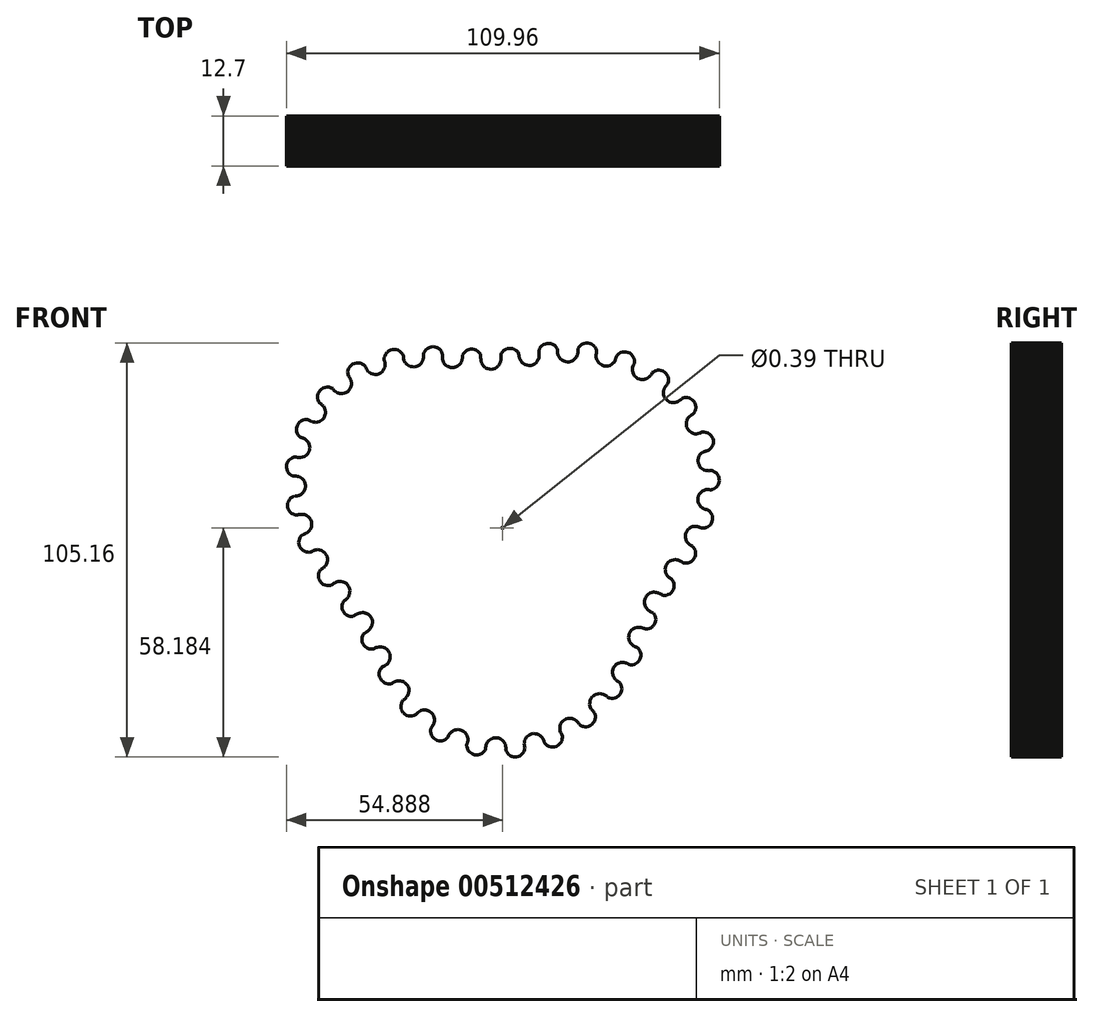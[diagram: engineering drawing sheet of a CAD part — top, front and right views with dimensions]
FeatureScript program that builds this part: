
annotation { "Feature Type Name" : "Feature", "Feature Type Description" : "" }
export const myFeature = defineFeature(function(context is Context, id is Id, definition is map)
    precondition{}
    {
        {
            var Q0;
            Q0=qCreatedBy(makeId("Front.planeOp"),FACE);
            var sketch = newSketch(context, id + "F0", { "sketchPlane" : qUnion([Q0])});
            skCircle(sketch, "E0", {"center": v(-0.1, 5.6) * mm, "radius": 0.2 * mm});
            skLineSegment(sketch, "E1", {"start": v(-7.26, -52) * mm, "end": v(-6.77, -52.07) * mm});
            skLineSegment(sketch, "E2", {"start": v(-6.77, -52.07) * mm, "end": v(-6.32, -52.04) * mm});
            skLineSegment(sketch, "E3", {"start": v(-6.32, -52.04) * mm, "end": v(-6.3, -52.04) * mm});
            skLineSegment(sketch, "E4", {"start": v(-6.3, -52.04) * mm, "end": v(-6.26, -52.04) * mm});
            skLineSegment(sketch, "E5", {"start": v(-6.26, -52.04) * mm, "end": v(-5.96, -51.96) * mm});
            skLineSegment(sketch, "E6", {"start": v(-5.96, -51.96) * mm, "end": v(-5.73, -51.88) * mm});
            skLineSegment(sketch, "E7", {"start": v(-5.73, -51.88) * mm, "end": v(-5.6, -51.82) * mm});
            skLineSegment(sketch, "E8", {"start": v(-5.6, -51.82) * mm, "end": v(-5.26, -51.62) * mm});
            skLineSegment(sketch, "E9", {"start": v(-5.26, -51.62) * mm, "end": v(-4.89, -51.3) * mm});
            skLineSegment(sketch, "E10", {"start": v(-4.89, -51.3) * mm, "end": v(-4.58, -50.9) * mm});
            skLineSegment(sketch, "E11", {"start": v(-4.58, -50.9) * mm, "end": v(-4.45, -50.63) * mm});
            skLineSegment(sketch, "E12", {"start": v(-4.45, -50.63) * mm, "end": v(-4.38, -50.48) * mm});
            skLineSegment(sketch, "E13", {"start": v(-4.38, -50.48) * mm, "end": v(-4.38, -50.3) * mm});
            skLineSegment(sketch, "E14", {"start": v(-4.38, -50.3) * mm, "end": v(-4.36, -50.15) * mm});
            skLineSegment(sketch, "E15", {"start": v(-4.36, -50.15) * mm, "end": v(-4.34, -49.93) * mm});
            skLineSegment(sketch, "E16", {"start": v(-4.34, -49.93) * mm, "end": v(-4.29, -49.71) * mm});
            skLineSegment(sketch, "E17", {"start": v(-4.29, -49.71) * mm, "end": v(-4.28, -49.67) * mm});
            skLineSegment(sketch, "E18", {"start": v(-4.28, -49.67) * mm, "end": v(-4.26, -49.6) * mm});
            skLineSegment(sketch, "E19", {"start": v(-4.26, -49.6) * mm, "end": v(-4.24, -49.52) * mm});
            skLineSegment(sketch, "E20", {"start": v(-4.24, -49.52) * mm, "end": v(-4.22, -49.45) * mm});
            skLineSegment(sketch, "E21", {"start": v(-4.22, -49.45) * mm, "end": v(-4.2, -49.4) * mm});
            skLineSegment(sketch, "E22", {"start": v(-4.2, -49.4) * mm, "end": v(-4.15, -49.25) * mm});
            skLineSegment(sketch, "E23", {"start": v(-4.15, -49.25) * mm, "end": v(-4.13, -49.2) * mm});
            skLineSegment(sketch, "E24", {"start": v(-4.13, -49.2) * mm, "end": v(-3.9, -48.77) * mm});
            skLineSegment(sketch, "E25", {"start": v(-3.9, -48.77) * mm, "end": v(-3.57, -48.4) * mm});
            skLineSegment(sketch, "E26", {"start": v(-3.57, -48.4) * mm, "end": v(-3.18, -48.1) * mm});
            skLineSegment(sketch, "E27", {"start": v(-3.18, -48.1) * mm, "end": v(-2.74, -47.87) * mm});
            skLineSegment(sketch, "E28", {"start": v(-2.74, -47.87) * mm, "end": v(-2.58, -47.82) * mm});
            skLineSegment(sketch, "E29", {"start": v(-2.58, -47.82) * mm, "end": v(-2.56, -47.81) * mm});
            skLineSegment(sketch, "E30", {"start": v(-2.56, -47.81) * mm, "end": v(-2.52, -47.8) * mm});
            skLineSegment(sketch, "E31", {"start": v(-2.52, -47.8) * mm, "end": v(-2.27, -47.73) * mm});
            skLineSegment(sketch, "E32", {"start": v(-2.27, -47.73) * mm, "end": v(-2.15, -47.72) * mm});
            skLineSegment(sketch, "E33", {"start": v(-2.15, -47.72) * mm, "end": v(-2.08, -47.7) * mm});
            skLineSegment(sketch, "E34", {"start": v(-2.08, -47.7) * mm, "end": v(-1.93, -47.7) * mm});
            skLineSegment(sketch, "E35", {"start": v(-1.93, -47.7) * mm, "end": v(-1.8, -47.7) * mm});
            skLineSegment(sketch, "E36", {"start": v(-1.8, -47.7) * mm, "end": v(-1.78, -47.7) * mm});
            skLineSegment(sketch, "E37", {"start": v(-1.78, -47.7) * mm, "end": v(-1.78, -47.7) * mm});
            skLineSegment(sketch, "E38", {"start": v(-1.78, -47.7) * mm, "end": v(-1.7, -47.7) * mm});
            skLineSegment(sketch, "E39", {"start": v(-1.7, -47.7) * mm, "end": v(-1.6, -47.7) * mm});
            skLineSegment(sketch, "E40", {"start": v(-1.6, -47.7) * mm, "end": v(-1.59, -47.7) * mm});
            skLineSegment(sketch, "E41", {"start": v(-1.59, -47.7) * mm, "end": v(-1.59, -47.7) * mm});
            skLineSegment(sketch, "E42", {"start": v(-1.59, -47.7) * mm, "end": v(-1.34, -47.74) * mm});
            skLineSegment(sketch, "E43", {"start": v(-1.34, -47.74) * mm, "end": v(-1.29, -47.75) * mm});
            skLineSegment(sketch, "E44", {"start": v(-1.29, -47.75) * mm, "end": v(-1.26, -47.76) * mm});
            skLineSegment(sketch, "E45", {"start": v(-1.26, -47.76) * mm, "end": v(-1.1, -47.79) * mm});
            skLineSegment(sketch, "E46", {"start": v(-1.1, -47.79) * mm, "end": v(-0.64, -47.97) * mm});
            skLineSegment(sketch, "E47", {"start": v(-0.64, -47.97) * mm, "end": v(-0.23, -48.24) * mm});
            skLineSegment(sketch, "E48", {"start": v(-0.23, -48.24) * mm, "end": v(0.13, -48.58) * mm});
            skLineSegment(sketch, "E49", {"start": v(0.13, -48.58) * mm, "end": v(0.41, -48.99) * mm});
            skLineSegment(sketch, "E50", {"start": v(0.41, -48.99) * mm, "end": v(0.6, -49.44) * mm});
            skLineSegment(sketch, "E51", {"start": v(0.6, -49.44) * mm, "end": v(0.64, -49.61) * mm});
            skLineSegment(sketch, "E52", {"start": v(0.64, -49.61) * mm, "end": v(0.67, -49.7) * mm});
            skLineSegment(sketch, "E53", {"start": v(0.67, -49.7) * mm, "end": v(0.7, -49.86) * mm});
            skLineSegment(sketch, "E54", {"start": v(0.7, -49.86) * mm, "end": v(0.71, -49.92) * mm});
            skLineSegment(sketch, "E55", {"start": v(0.71, -49.92) * mm, "end": v(0.71, -49.95) * mm});
            skLineSegment(sketch, "E56", {"start": v(0.71, -49.95) * mm, "end": v(0.75, -50.18) * mm});
            skLineSegment(sketch, "E57", {"start": v(0.75, -50.18) * mm, "end": v(0.74, -50.4) * mm});
            skLineSegment(sketch, "E58", {"start": v(0.74, -50.4) * mm, "end": v(0.75, -50.54) * mm});
            skLineSegment(sketch, "E59", {"start": v(0.75, -50.54) * mm, "end": v(0.74, -50.58) * mm});
            skLineSegment(sketch, "E60", {"start": v(0.74, -50.58) * mm, "end": v(0.73, -50.74) * mm});
            skLineSegment(sketch, "E61", {"start": v(0.73, -50.74) * mm, "end": v(0.76, -50.84) * mm});
            skLineSegment(sketch, "E62", {"start": v(0.76, -50.84) * mm, "end": v(0.78, -50.93) * mm});
            skLineSegment(sketch, "E63", {"start": v(0.78, -50.93) * mm, "end": v(0.88, -51.2) * mm});
            skLineSegment(sketch, "E64", {"start": v(0.88, -51.2) * mm, "end": v(1.14, -51.61) * mm});
            skLineSegment(sketch, "E65", {"start": v(1.14, -51.61) * mm, "end": v(1.48, -51.97) * mm});
            skLineSegment(sketch, "E66", {"start": v(1.48, -51.97) * mm, "end": v(1.86, -52.24) * mm});
            skLineSegment(sketch, "E67", {"start": v(1.86, -52.24) * mm, "end": v(1.9, -52.27) * mm});
            skLineSegment(sketch, "E68", {"start": v(1.9, -52.27) * mm, "end": v(2.2, -52.4) * mm});
            skLineSegment(sketch, "E69", {"start": v(2.2, -52.4) * mm, "end": v(2.4, -52.48) * mm});
            skLineSegment(sketch, "E70", {"start": v(2.4, -52.48) * mm, "end": v(2.57, -52.52) * mm});
            skLineSegment(sketch, "E71", {"start": v(2.57, -52.52) * mm, "end": v(2.68, -52.54) * mm});
            skLineSegment(sketch, "E72", {"start": v(2.68, -52.54) * mm, "end": v(2.93, -52.58) * mm});
            skLineSegment(sketch, "E73", {"start": v(2.93, -52.58) * mm, "end": v(2.94, -52.58) * mm});
            skLineSegment(sketch, "E74", {"start": v(2.94, -52.58) * mm, "end": v(2.94, -52.58) * mm});
            skLineSegment(sketch, "E75", {"start": v(2.94, -52.58) * mm, "end": v(3.43, -52.57) * mm});
            skLineSegment(sketch, "E76", {"start": v(3.43, -52.57) * mm, "end": v(3.43, -52.57) * mm});
            skLineSegment(sketch, "E77", {"start": v(3.43, -52.57) * mm, "end": v(3.91, -52.46) * mm});
            skLineSegment(sketch, "E78", {"start": v(3.91, -52.46) * mm, "end": v(4.36, -52.25) * mm});
            skLineSegment(sketch, "E79", {"start": v(4.36, -52.25) * mm, "end": v(4.76, -51.97) * mm});
            skLineSegment(sketch, "E80", {"start": v(4.76, -51.97) * mm, "end": v(5.1, -51.6) * mm});
            skLineSegment(sketch, "E81", {"start": v(5.1, -51.6) * mm, "end": v(5.36, -51.19) * mm});
            skLineSegment(sketch, "E82", {"start": v(5.36, -51.19) * mm, "end": v(5.52, -50.76) * mm});
            skLineSegment(sketch, "E83", {"start": v(5.52, -50.76) * mm, "end": v(5.54, -50.7) * mm});
            skLineSegment(sketch, "E84", {"start": v(5.54, -50.7) * mm, "end": v(5.54, -50.7) * mm});
            skLineSegment(sketch, "E85", {"start": v(5.54, -50.7) * mm, "end": v(5.56, -50.56) * mm});
            skLineSegment(sketch, "E86", {"start": v(5.56, -50.56) * mm, "end": v(5.6, -50.23) * mm});
            skLineSegment(sketch, "E87", {"start": v(5.6, -50.23) * mm, "end": v(5.5, -49.94) * mm});
            skLineSegment(sketch, "E88", {"start": v(5.5, -49.94) * mm, "end": v(5.49, -49.76) * mm});
            skLineSegment(sketch, "E89", {"start": v(5.49, -49.76) * mm, "end": v(5.45, -49.6) * mm});
            skLineSegment(sketch, "E90", {"start": v(5.45, -49.6) * mm, "end": v(5.43, -49.1) * mm});
            skLineSegment(sketch, "E91", {"start": v(5.43, -49.1) * mm, "end": v(5.45, -48.97) * mm});
            skLineSegment(sketch, "E92", {"start": v(5.45, -48.97) * mm, "end": v(5.45, -48.87) * mm});
            skLineSegment(sketch, "E93", {"start": v(5.45, -48.87) * mm, "end": v(5.5, -48.68) * mm});
            skLineSegment(sketch, "E94", {"start": v(5.5, -48.68) * mm, "end": v(5.5, -48.62) * mm});
            skLineSegment(sketch, "E95", {"start": v(5.5, -48.62) * mm, "end": v(5.51, -48.6) * mm});
            skLineSegment(sketch, "E96", {"start": v(5.51, -48.6) * mm, "end": v(5.56, -48.39) * mm});
            skLineSegment(sketch, "E97", {"start": v(5.56, -48.39) * mm, "end": v(5.76, -47.94) * mm});
            skLineSegment(sketch, "E98", {"start": v(5.76, -47.94) * mm, "end": v(6.04, -47.53) * mm});
            skLineSegment(sketch, "E99", {"start": v(6.04, -47.53) * mm, "end": v(6.4, -47.19) * mm});
            skLineSegment(sketch, "E100", {"start": v(6.4, -47.19) * mm, "end": v(6.81, -46.92) * mm});
            skLineSegment(sketch, "E101", {"start": v(6.81, -46.92) * mm, "end": v(7.27, -46.74) * mm});
            skLineSegment(sketch, "E102", {"start": v(7.27, -46.74) * mm, "end": v(7.27, -46.74) * mm});
            skLineSegment(sketch, "E103", {"start": v(7.27, -46.74) * mm, "end": v(7.76, -46.66) * mm});
            skLineSegment(sketch, "E104", {"start": v(7.76, -46.66) * mm, "end": v(8.25, -46.67) * mm});
            skLineSegment(sketch, "E105", {"start": v(8.25, -46.67) * mm, "end": v(8.73, -46.77) * mm});
            skLineSegment(sketch, "E106", {"start": v(8.73, -46.77) * mm, "end": v(8.87, -46.83) * mm});
            skLineSegment(sketch, "E107", {"start": v(8.87, -46.83) * mm, "end": v(8.92, -46.85) * mm});
            skLineSegment(sketch, "E108", {"start": v(8.92, -46.85) * mm, "end": v(9.03, -46.9) * mm});
            skLineSegment(sketch, "E109", {"start": v(9.03, -46.9) * mm, "end": v(9.19, -46.97) * mm});
            skLineSegment(sketch, "E110", {"start": v(9.19, -46.97) * mm, "end": v(9.25, -47.02) * mm});
            skLineSegment(sketch, "E111", {"start": v(9.25, -47.02) * mm, "end": v(9.36, -47.07) * mm});
            skLineSegment(sketch, "E112", {"start": v(9.36, -47.07) * mm, "end": v(9.56, -47.23) * mm});
            skLineSegment(sketch, "E113", {"start": v(9.56, -47.23) * mm, "end": v(9.6, -47.25) * mm});
            skLineSegment(sketch, "E114", {"start": v(9.6, -47.25) * mm, "end": v(9.6, -47.27) * mm});
            skLineSegment(sketch, "E115", {"start": v(9.6, -47.27) * mm, "end": v(9.75, -47.38) * mm});
            skLineSegment(sketch, "E116", {"start": v(9.75, -47.38) * mm, "end": v(10.07, -47.76) * mm});
            skLineSegment(sketch, "E117", {"start": v(10.07, -47.76) * mm, "end": v(10.12, -47.86) * mm});
            skLineSegment(sketch, "E118", {"start": v(10.12, -47.86) * mm, "end": v(10.2, -48) * mm});
            skLineSegment(sketch, "E119", {"start": v(10.2, -48) * mm, "end": v(10.2, -48.02) * mm});
            skLineSegment(sketch, "E120", {"start": v(10.2, -48.02) * mm, "end": v(10.22, -48.03) * mm});
            skLineSegment(sketch, "E121", {"start": v(10.22, -48.03) * mm, "end": v(10.3, -48.2) * mm});
            skLineSegment(sketch, "E122", {"start": v(10.3, -48.2) * mm, "end": v(10.33, -48.26) * mm});
            skLineSegment(sketch, "E123", {"start": v(10.33, -48.26) * mm, "end": v(10.33, -48.27) * mm});
            skLineSegment(sketch, "E124", {"start": v(10.33, -48.27) * mm, "end": v(10.42, -48.46) * mm});
            skLineSegment(sketch, "E125", {"start": v(10.42, -48.46) * mm, "end": v(10.49, -48.72) * mm});
            skLineSegment(sketch, "E126", {"start": v(10.49, -48.72) * mm, "end": v(10.53, -48.84) * mm});
            skLineSegment(sketch, "E127", {"start": v(10.53, -48.84) * mm, "end": v(10.55, -48.94) * mm});
            skLineSegment(sketch, "E128", {"start": v(10.55, -48.94) * mm, "end": v(10.58, -48.98) * mm});
            skLineSegment(sketch, "E129", {"start": v(10.58, -48.98) * mm, "end": v(10.8, -49.28) * mm});
            skLineSegment(sketch, "E130", {"start": v(10.8, -49.28) * mm, "end": v(11.16, -49.6) * mm});
            skLineSegment(sketch, "E131", {"start": v(11.16, -49.6) * mm, "end": v(11.18, -49.6) * mm});
            skLineSegment(sketch, "E132", {"start": v(11.18, -49.6) * mm, "end": v(11.45, -49.77) * mm});
            skLineSegment(sketch, "E133", {"start": v(11.45, -49.77) * mm, "end": v(11.68, -49.88) * mm});
            skLineSegment(sketch, "E134", {"start": v(11.68, -49.88) * mm, "end": v(11.76, -49.9) * mm});
            skLineSegment(sketch, "E135", {"start": v(11.76, -49.9) * mm, "end": v(12.18, -50.02) * mm});
            skLineSegment(sketch, "E136", {"start": v(12.18, -50.02) * mm, "end": v(12.67, -50.06) * mm});
            skLineSegment(sketch, "E137", {"start": v(12.67, -50.06) * mm, "end": v(13.16, -50) * mm});
            skLineSegment(sketch, "E138", {"start": v(13.16, -50) * mm, "end": v(13.63, -49.84) * mm});
            skLineSegment(sketch, "E139", {"start": v(13.63, -49.84) * mm, "end": v(13.63, -49.84) * mm});
            skLineSegment(sketch, "E140", {"start": v(13.63, -49.84) * mm, "end": v(14.06, -49.6) * mm});
            skLineSegment(sketch, "E141", {"start": v(14.06, -49.6) * mm, "end": v(14.43, -49.28) * mm});
            skLineSegment(sketch, "E142", {"start": v(14.43, -49.28) * mm, "end": v(14.74, -48.89) * mm});
            skLineSegment(sketch, "E143", {"start": v(14.74, -48.89) * mm, "end": v(14.96, -48.45) * mm});
            skLineSegment(sketch, "E144", {"start": v(14.96, -48.45) * mm, "end": v(15.09, -47.97) * mm});
            skLineSegment(sketch, "E145", {"start": v(15.09, -47.97) * mm, "end": v(15.1, -47.67) * mm});
            skLineSegment(sketch, "E146", {"start": v(15.1, -47.67) * mm, "end": v(15.11, -47.4) * mm});
            skLineSegment(sketch, "E147", {"start": v(15.11, -47.4) * mm, "end": v(15.03, -46.98) * mm});
            skLineSegment(sketch, "E148", {"start": v(15.03, -46.98) * mm, "end": v(14.85, -46.71) * mm});
            skLineSegment(sketch, "E149", {"start": v(14.85, -46.71) * mm, "end": v(14.78, -46.53) * mm});
            skLineSegment(sketch, "E150", {"start": v(14.78, -46.53) * mm, "end": v(14.7, -46.4) * mm});
            skLineSegment(sketch, "E151", {"start": v(14.7, -46.4) * mm, "end": v(14.53, -45.92) * mm});
            skLineSegment(sketch, "E152", {"start": v(14.53, -45.92) * mm, "end": v(14.5, -45.76) * mm});
            skLineSegment(sketch, "E153", {"start": v(14.5, -45.76) * mm, "end": v(14.49, -45.68) * mm});
            skLineSegment(sketch, "E154", {"start": v(14.49, -45.68) * mm, "end": v(14.48, -45.54) * mm});
            skLineSegment(sketch, "E155", {"start": v(14.48, -45.54) * mm, "end": v(14.46, -45.44) * mm});
            skLineSegment(sketch, "E156", {"start": v(14.46, -45.44) * mm, "end": v(14.47, -45.38) * mm});
            skLineSegment(sketch, "E157", {"start": v(14.47, -45.38) * mm, "end": v(14.45, -45.2) * mm});
            skLineSegment(sketch, "E158", {"start": v(14.45, -45.2) * mm, "end": v(14.52, -44.7) * mm});
            skLineSegment(sketch, "E159", {"start": v(14.52, -44.7) * mm, "end": v(14.67, -44.23) * mm});
            skLineSegment(sketch, "E160", {"start": v(14.67, -44.23) * mm, "end": v(14.92, -43.8) * mm});
            skLineSegment(sketch, "E161", {"start": v(14.92, -43.8) * mm, "end": v(15.24, -43.43) * mm});
            skLineSegment(sketch, "E162", {"start": v(15.24, -43.43) * mm, "end": v(15.63, -43.13) * mm});
            skLineSegment(sketch, "E163", {"start": v(15.63, -43.13) * mm, "end": v(15.63, -43.13) * mm});
            skLineSegment(sketch, "E164", {"start": v(15.63, -43.13) * mm, "end": v(16.07, -42.9) * mm});
            skLineSegment(sketch, "E165", {"start": v(16.07, -42.9) * mm, "end": v(16.55, -42.78) * mm});
            skLineSegment(sketch, "E166", {"start": v(16.55, -42.78) * mm, "end": v(17.04, -42.74) * mm});
            skLineSegment(sketch, "E167", {"start": v(17.04, -42.74) * mm, "end": v(17.53, -42.8) * mm});
            skLineSegment(sketch, "E168", {"start": v(17.53, -42.8) * mm, "end": v(17.67, -42.85) * mm});
            skLineSegment(sketch, "E169", {"start": v(17.67, -42.85) * mm, "end": v(17.74, -42.86) * mm});
            skLineSegment(sketch, "E170", {"start": v(17.74, -42.86) * mm, "end": v(17.88, -42.92) * mm});
            skLineSegment(sketch, "E171", {"start": v(17.88, -42.92) * mm, "end": v(18, -42.96) * mm});
            skLineSegment(sketch, "E172", {"start": v(18, -42.96) * mm, "end": v(18.05, -42.99) * mm});
            skLineSegment(sketch, "E173", {"start": v(18.05, -42.99) * mm, "end": v(18.2, -43.05) * mm});
            skLineSegment(sketch, "E174", {"start": v(18.2, -43.05) * mm, "end": v(18.6, -43.32) * mm});
            skLineSegment(sketch, "E175", {"start": v(18.6, -43.32) * mm, "end": v(18.96, -43.67) * mm});
            skLineSegment(sketch, "E176", {"start": v(18.96, -43.67) * mm, "end": v(19.02, -43.76) * mm});
            skLineSegment(sketch, "E177", {"start": v(19.02, -43.76) * mm, "end": v(19.16, -43.91) * mm});
            skLineSegment(sketch, "E178", {"start": v(19.16, -43.91) * mm, "end": v(19.31, -44.17) * mm});
            skLineSegment(sketch, "E179", {"start": v(19.31, -44.17) * mm, "end": v(19.39, -44.27) * mm});
            skLineSegment(sketch, "E180", {"start": v(19.39, -44.27) * mm, "end": v(19.4, -44.3) * mm});
            skLineSegment(sketch, "E181", {"start": v(19.4, -44.3) * mm, "end": v(19.45, -44.34) * mm});
            skLineSegment(sketch, "E182", {"start": v(19.45, -44.34) * mm, "end": v(19.73, -44.55) * mm});
            skLineSegment(sketch, "E183", {"start": v(19.73, -44.55) * mm, "end": v(20.18, -44.76) * mm});
            skLineSegment(sketch, "E184", {"start": v(20.18, -44.76) * mm, "end": v(20.32, -44.8) * mm});
            skLineSegment(sketch, "E185", {"start": v(20.32, -44.8) * mm, "end": v(20.6, -44.87) * mm});
            skLineSegment(sketch, "E186", {"start": v(20.6, -44.87) * mm, "end": v(20.69, -44.88) * mm});
            skLineSegment(sketch, "E187", {"start": v(20.69, -44.88) * mm, "end": v(20.9, -44.9) * mm});
            skLineSegment(sketch, "E188", {"start": v(20.9, -44.9) * mm, "end": v(20.95, -44.9) * mm});
            skLineSegment(sketch, "E189", {"start": v(20.95, -44.9) * mm, "end": v(21.1, -44.9) * mm});
            skLineSegment(sketch, "E190", {"start": v(21.1, -44.9) * mm, "end": v(21.25, -44.9) * mm});
            skLineSegment(sketch, "E191", {"start": v(21.25, -44.9) * mm, "end": v(21.28, -44.89) * mm});
            skLineSegment(sketch, "E192", {"start": v(21.28, -44.89) * mm, "end": v(21.3, -44.88) * mm});
            skLineSegment(sketch, "E193", {"start": v(21.3, -44.88) * mm, "end": v(21.75, -44.79) * mm});
            skLineSegment(sketch, "E194", {"start": v(21.75, -44.79) * mm, "end": v(22.2, -44.59) * mm});
            skLineSegment(sketch, "E195", {"start": v(22.2, -44.59) * mm, "end": v(22.6, -44.3) * mm});
            skLineSegment(sketch, "E196", {"start": v(22.6, -44.3) * mm, "end": v(22.6, -44.3) * mm});
            skLineSegment(sketch, "E197", {"start": v(22.6, -44.3) * mm, "end": v(22.95, -43.95) * mm});
            skLineSegment(sketch, "E198", {"start": v(22.95, -43.95) * mm, "end": v(23.22, -43.54) * mm});
            skLineSegment(sketch, "E199", {"start": v(23.22, -43.54) * mm, "end": v(23.4, -43.08) * mm});
            skLineSegment(sketch, "E200", {"start": v(23.4, -43.08) * mm, "end": v(23.49, -42.6) * mm});
            skLineSegment(sketch, "E201", {"start": v(23.49, -42.6) * mm, "end": v(23.48, -42.1) * mm});
            skLineSegment(sketch, "E202", {"start": v(23.48, -42.1) * mm, "end": v(23.4, -41.7) * mm});
            skLineSegment(sketch, "E203", {"start": v(23.4, -41.7) * mm, "end": v(23.35, -41.57) * mm});
            skLineSegment(sketch, "E204", {"start": v(23.35, -41.57) * mm, "end": v(23.32, -41.5) * mm});
            skLineSegment(sketch, "E205", {"start": v(23.32, -41.5) * mm, "end": v(23.26, -41.4) * mm});
            skLineSegment(sketch, "E206", {"start": v(23.26, -41.4) * mm, "end": v(23.17, -41.2) * mm});
            skLineSegment(sketch, "E207", {"start": v(23.17, -41.2) * mm, "end": v(22.96, -41.04) * mm});
            skLineSegment(sketch, "E208", {"start": v(22.96, -41.04) * mm, "end": v(22.87, -40.92) * mm});
            skLineSegment(sketch, "E209", {"start": v(22.87, -40.92) * mm, "end": v(22.75, -40.8) * mm});
            skLineSegment(sketch, "E210", {"start": v(22.75, -40.8) * mm, "end": v(22.58, -40.58) * mm});
            skLineSegment(sketch, "E211", {"start": v(22.58, -40.58) * mm, "end": v(22.57, -40.56) * mm});
            skLineSegment(sketch, "E212", {"start": v(22.57, -40.56) * mm, "end": v(22.54, -40.52) * mm});
            skLineSegment(sketch, "E213", {"start": v(22.54, -40.52) * mm, "end": v(22.46, -40.4) * mm});
            skLineSegment(sketch, "E214", {"start": v(22.46, -40.4) * mm, "end": v(22.43, -40.33) * mm});
            skLineSegment(sketch, "E215", {"start": v(22.43, -40.33) * mm, "end": v(22.3, -40.14) * mm});
            skLineSegment(sketch, "E216", {"start": v(22.3, -40.14) * mm, "end": v(22.13, -39.68) * mm});
            skLineSegment(sketch, "E217", {"start": v(22.13, -39.68) * mm, "end": v(22.05, -39.2) * mm});
            skLineSegment(sketch, "E218", {"start": v(22.05, -39.2) * mm, "end": v(22.07, -38.7) * mm});
            skLineSegment(sketch, "E219", {"start": v(22.07, -38.7) * mm, "end": v(22.18, -38.22) * mm});
            skLineSegment(sketch, "E220", {"start": v(22.18, -38.22) * mm, "end": v(22.39, -37.77) * mm});
            skLineSegment(sketch, "E221", {"start": v(22.39, -37.77) * mm, "end": v(22.68, -37.37) * mm});
            skLineSegment(sketch, "E222", {"start": v(22.68, -37.37) * mm, "end": v(22.68, -37.37) * mm});
            skLineSegment(sketch, "E223", {"start": v(22.68, -37.37) * mm, "end": v(22.79, -37.26) * mm});
            skLineSegment(sketch, "E224", {"start": v(22.79, -37.26) * mm, "end": v(22.83, -37.22) * mm});
            skLineSegment(sketch, "E225", {"start": v(22.83, -37.22) * mm, "end": v(22.83, -37.22) * mm});
            skLineSegment(sketch, "E226", {"start": v(22.83, -37.22) * mm, "end": v(22.9, -37.15) * mm});
            skLineSegment(sketch, "E227", {"start": v(22.9, -37.15) * mm, "end": v(23.04, -37.03) * mm});
            skLineSegment(sketch, "E228", {"start": v(23.04, -37.03) * mm, "end": v(23.12, -36.98) * mm});
            skLineSegment(sketch, "E229", {"start": v(23.12, -36.98) * mm, "end": v(23.2, -36.9) * mm});
            skLineSegment(sketch, "E230", {"start": v(23.2, -36.9) * mm, "end": v(23.4, -36.8) * mm});
            skLineSegment(sketch, "E231", {"start": v(23.4, -36.8) * mm, "end": v(23.46, -36.77) * mm});
            skLineSegment(sketch, "E232", {"start": v(23.46, -36.77) * mm, "end": v(23.49, -36.76) * mm});
            skLineSegment(sketch, "E233", {"start": v(23.49, -36.76) * mm, "end": v(23.65, -36.68) * mm});
            skLineSegment(sketch, "E234", {"start": v(23.65, -36.68) * mm, "end": v(24.12, -36.54) * mm});
            skLineSegment(sketch, "E235", {"start": v(24.12, -36.54) * mm, "end": v(24.6, -36.5) * mm});
            skLineSegment(sketch, "E236", {"start": v(24.6, -36.5) * mm, "end": v(25.1, -36.54) * mm});
            skLineSegment(sketch, "E237", {"start": v(25.1, -36.54) * mm, "end": v(25.57, -36.69) * mm});
            skLineSegment(sketch, "E238", {"start": v(25.57, -36.69) * mm, "end": v(25.8, -36.8) * mm});
            skLineSegment(sketch, "E239", {"start": v(25.8, -36.8) * mm, "end": v(25.84, -36.83) * mm});
            skLineSegment(sketch, "E240", {"start": v(25.84, -36.83) * mm, "end": v(25.92, -36.88) * mm});
            skLineSegment(sketch, "E241", {"start": v(25.92, -36.88) * mm, "end": v(26, -36.92) * mm});
            skLineSegment(sketch, "E242", {"start": v(26, -36.92) * mm, "end": v(26.02, -36.93) * mm});
            skLineSegment(sketch, "E243", {"start": v(26.02, -36.93) * mm, "end": v(26.04, -36.95) * mm});
            skLineSegment(sketch, "E244", {"start": v(26.04, -36.95) * mm, "end": v(26.26, -37.1) * mm});
            skLineSegment(sketch, "E245", {"start": v(26.26, -37.1) * mm, "end": v(26.4, -37.21) * mm});
            skLineSegment(sketch, "E246", {"start": v(26.4, -37.21) * mm, "end": v(26.45, -37.27) * mm});
            skLineSegment(sketch, "E247", {"start": v(26.45, -37.27) * mm, "end": v(26.58, -37.37) * mm});
            skLineSegment(sketch, "E248", {"start": v(26.58, -37.37) * mm, "end": v(26.65, -37.45) * mm});
            skLineSegment(sketch, "E249", {"start": v(26.65, -37.45) * mm, "end": v(26.68, -37.48) * mm});
            skLineSegment(sketch, "E250", {"start": v(26.68, -37.48) * mm, "end": v(26.9, -37.57) * mm});
            skLineSegment(sketch, "E251", {"start": v(26.9, -37.57) * mm, "end": v(27.06, -37.63) * mm});
            skLineSegment(sketch, "E252", {"start": v(27.06, -37.63) * mm, "end": v(27.54, -37.72) * mm});
            skLineSegment(sketch, "E253", {"start": v(27.54, -37.72) * mm, "end": v(28.04, -37.7) * mm});
            skLineSegment(sketch, "E254", {"start": v(28.04, -37.7) * mm, "end": v(28.52, -37.6) * mm});
            skLineSegment(sketch, "E255", {"start": v(28.52, -37.6) * mm, "end": v(28.9, -37.43) * mm});
            skLineSegment(sketch, "E256", {"start": v(28.9, -37.43) * mm, "end": v(29, -37.38) * mm});
            skLineSegment(sketch, "E257", {"start": v(29, -37.38) * mm, "end": v(29.16, -37.26) * mm});
            skLineSegment(sketch, "E258", {"start": v(29.16, -37.26) * mm, "end": v(29.2, -37.22) * mm});
            skLineSegment(sketch, "E259", {"start": v(29.2, -37.22) * mm, "end": v(29.42, -37.06) * mm});
            skLineSegment(sketch, "E260", {"start": v(29.42, -37.06) * mm, "end": v(29.5, -36.98) * mm});
            skLineSegment(sketch, "E261", {"start": v(29.5, -36.98) * mm, "end": v(29.76, -36.66) * mm});
            skLineSegment(sketch, "E262", {"start": v(29.76, -36.66) * mm, "end": v(29.76, -36.66) * mm});
            skLineSegment(sketch, "E263", {"start": v(29.76, -36.66) * mm, "end": v(30, -36.23) * mm});
            skLineSegment(sketch, "E264", {"start": v(30, -36.23) * mm, "end": v(30.16, -35.76) * mm});
            skLineSegment(sketch, "E265", {"start": v(30.16, -35.76) * mm, "end": v(30.21, -35.27) * mm});
            skLineSegment(sketch, "E266", {"start": v(30.21, -35.27) * mm, "end": v(30.17, -34.78) * mm});
            skLineSegment(sketch, "E267", {"start": v(30.17, -34.78) * mm, "end": v(30.04, -34.3) * mm});
            skLineSegment(sketch, "E268", {"start": v(30.04, -34.3) * mm, "end": v(29.88, -34) * mm});
            skLineSegment(sketch, "E269", {"start": v(29.88, -34) * mm, "end": v(29.78, -33.82) * mm});
            skLineSegment(sketch, "E270", {"start": v(29.78, -33.82) * mm, "end": v(29.77, -33.81) * mm});
            skLineSegment(sketch, "E271", {"start": v(29.77, -33.81) * mm, "end": v(29.56, -33.57) * mm});
            skLineSegment(sketch, "E272", {"start": v(29.56, -33.57) * mm, "end": v(29.35, -33.47) * mm});
            skLineSegment(sketch, "E273", {"start": v(29.35, -33.47) * mm, "end": v(29.22, -33.37) * mm});
            skLineSegment(sketch, "E274", {"start": v(29.22, -33.37) * mm, "end": v(29.05, -33.28) * mm});
            skLineSegment(sketch, "E275", {"start": v(29.05, -33.28) * mm, "end": v(28.89, -33.14) * mm});
            skLineSegment(sketch, "E276", {"start": v(28.89, -33.14) * mm, "end": v(28.84, -33.11) * mm});
            skLineSegment(sketch, "E277", {"start": v(28.84, -33.11) * mm, "end": v(28.74, -33.02) * mm});
            skLineSegment(sketch, "E278", {"start": v(28.74, -33.02) * mm, "end": v(28.67, -32.96) * mm});
            skLineSegment(sketch, "E279", {"start": v(28.67, -32.96) * mm, "end": v(28.65, -32.94) * mm});
            skLineSegment(sketch, "E280", {"start": v(28.65, -32.94) * mm, "end": v(28.48, -32.78) * mm});
            skLineSegment(sketch, "E281", {"start": v(28.48, -32.78) * mm, "end": v(28.19, -32.38) * mm});
            skLineSegment(sketch, "E282", {"start": v(28.19, -32.38) * mm, "end": v(28.13, -32.25) * mm});
            skLineSegment(sketch, "E283", {"start": v(28.13, -32.25) * mm, "end": v(28.1, -32.2) * mm});
            skLineSegment(sketch, "E284", {"start": v(28.1, -32.2) * mm, "end": v(28.06, -32.08) * mm});
            skLineSegment(sketch, "E285", {"start": v(28.06, -32.08) * mm, "end": v(27.98, -31.93) * mm});
            skLineSegment(sketch, "E286", {"start": v(27.98, -31.93) * mm, "end": v(27.97, -31.86) * mm});
            skLineSegment(sketch, "E287", {"start": v(27.97, -31.86) * mm, "end": v(27.92, -31.75) * mm});
            skLineSegment(sketch, "E288", {"start": v(27.92, -31.75) * mm, "end": v(27.84, -31.26) * mm});
            skLineSegment(sketch, "E289", {"start": v(27.84, -31.26) * mm, "end": v(27.85, -30.77) * mm});
            skLineSegment(sketch, "E290", {"start": v(27.85, -30.77) * mm, "end": v(27.95, -30.29) * mm});
            skLineSegment(sketch, "E291", {"start": v(27.95, -30.29) * mm, "end": v(28.15, -29.83) * mm});
            skLineSegment(sketch, "E292", {"start": v(28.15, -29.83) * mm, "end": v(28.15, -29.83) * mm});
            skLineSegment(sketch, "E293", {"start": v(28.15, -29.83) * mm, "end": v(28.43, -29.43) * mm});
            skLineSegment(sketch, "E294", {"start": v(28.43, -29.43) * mm, "end": v(28.79, -29.09) * mm});
            skLineSegment(sketch, "E295", {"start": v(28.79, -29.09) * mm, "end": v(29.2, -28.82) * mm});
            skLineSegment(sketch, "E296", {"start": v(29.2, -28.82) * mm, "end": v(29.67, -28.64) * mm});
            skLineSegment(sketch, "E297", {"start": v(29.67, -28.64) * mm, "end": v(29.82, -28.61) * mm});
            skLineSegment(sketch, "E298", {"start": v(29.82, -28.61) * mm, "end": v(29.85, -28.6) * mm});
            skLineSegment(sketch, "E299", {"start": v(29.85, -28.6) * mm, "end": v(29.96, -28.59) * mm});
            skLineSegment(sketch, "E300", {"start": v(29.96, -28.59) * mm, "end": v(30.15, -28.55) * mm});
            skLineSegment(sketch, "E301", {"start": v(30.15, -28.55) * mm, "end": v(30.23, -28.55) * mm});
            skLineSegment(sketch, "E302", {"start": v(30.23, -28.55) * mm, "end": v(30.34, -28.54) * mm});
            skLineSegment(sketch, "E303", {"start": v(30.34, -28.54) * mm, "end": v(30.64, -28.56) * mm});
            skLineSegment(sketch, "E304", {"start": v(30.64, -28.56) * mm, "end": v(30.64, -28.56) * mm});
            skLineSegment(sketch, "E305", {"start": v(30.64, -28.56) * mm, "end": v(30.65, -28.56) * mm});
            skLineSegment(sketch, "E306", {"start": v(30.65, -28.56) * mm, "end": v(30.84, -28.58) * mm});
            skLineSegment(sketch, "E307", {"start": v(30.84, -28.58) * mm, "end": v(31.07, -28.64) * mm});
            skLineSegment(sketch, "E308", {"start": v(31.07, -28.64) * mm, "end": v(31.1, -28.65) * mm});
            skLineSegment(sketch, "E309", {"start": v(31.1, -28.65) * mm, "end": v(31.14, -28.66) * mm});
            skLineSegment(sketch, "E310", {"start": v(31.14, -28.66) * mm, "end": v(31.31, -28.7) * mm});
            skLineSegment(sketch, "E311", {"start": v(31.31, -28.7) * mm, "end": v(31.37, -28.74) * mm});
            skLineSegment(sketch, "E312", {"start": v(31.37, -28.74) * mm, "end": v(31.56, -28.8) * mm});
            skLineSegment(sketch, "E313", {"start": v(31.56, -28.8) * mm, "end": v(31.64, -28.85) * mm});
            skLineSegment(sketch, "E314", {"start": v(31.64, -28.85) * mm, "end": v(31.73, -28.9) * mm});
            skLineSegment(sketch, "E315", {"start": v(31.73, -28.9) * mm, "end": v(31.86, -28.95) * mm});
            skLineSegment(sketch, "E316", {"start": v(31.86, -28.95) * mm, "end": v(32.1, -29.1) * mm});
            skLineSegment(sketch, "E317", {"start": v(32.1, -29.1) * mm, "end": v(32.38, -29.16) * mm});
            skLineSegment(sketch, "E318", {"start": v(32.38, -29.16) * mm, "end": v(32.6, -29.16) * mm});
            skLineSegment(sketch, "E319", {"start": v(32.6, -29.16) * mm, "end": v(32.94, -29.15) * mm});
            skLineSegment(sketch, "E320", {"start": v(32.94, -29.15) * mm, "end": v(33.42, -29.02) * mm});
            skLineSegment(sketch, "E321", {"start": v(33.42, -29.02) * mm, "end": v(33.86, -28.81) * mm});
            skLineSegment(sketch, "E322", {"start": v(33.86, -28.81) * mm, "end": v(34.26, -28.52) * mm});
            skLineSegment(sketch, "E323", {"start": v(34.26, -28.52) * mm, "end": v(34.59, -28.15) * mm});
            skLineSegment(sketch, "E324", {"start": v(34.59, -28.15) * mm, "end": v(34.84, -27.73) * mm});
            skLineSegment(sketch, "E325", {"start": v(34.84, -27.73) * mm, "end": v(34.84, -27.73) * mm});
            skLineSegment(sketch, "E326", {"start": v(34.84, -27.73) * mm, "end": v(35, -27.26) * mm});
            skLineSegment(sketch, "E327", {"start": v(35, -27.26) * mm, "end": v(35.06, -26.86) * mm});
            skLineSegment(sketch, "E328", {"start": v(35.06, -26.86) * mm, "end": v(35.07, -26.73) * mm});
            skLineSegment(sketch, "E329", {"start": v(35.07, -26.73) * mm, "end": v(35.06, -26.5) * mm});
            skLineSegment(sketch, "E330", {"start": v(35.06, -26.5) * mm, "end": v(35.03, -26.2) * mm});
            skLineSegment(sketch, "E331", {"start": v(35.03, -26.2) * mm, "end": v(35.01, -26.14) * mm});
            skLineSegment(sketch, "E332", {"start": v(35.01, -26.14) * mm, "end": v(34.87, -25.7) * mm});
            skLineSegment(sketch, "E333", {"start": v(34.87, -25.7) * mm, "end": v(34.64, -25.27) * mm});
            skLineSegment(sketch, "E334", {"start": v(34.64, -25.27) * mm, "end": v(34.32, -24.9) * mm});
            skLineSegment(sketch, "E335", {"start": v(34.32, -24.9) * mm, "end": v(34.23, -24.82) * mm});
            skLineSegment(sketch, "E336", {"start": v(34.23, -24.82) * mm, "end": v(34.08, -24.78) * mm});
            skLineSegment(sketch, "E337", {"start": v(34.08, -24.78) * mm, "end": v(33.84, -24.66) * mm});
            skLineSegment(sketch, "E338", {"start": v(33.84, -24.66) * mm, "end": v(33.67, -24.6) * mm});
            skLineSegment(sketch, "E339", {"start": v(33.67, -24.6) * mm, "end": v(33.47, -24.49) * mm});
            skLineSegment(sketch, "E340", {"start": v(33.47, -24.49) * mm, "end": v(33.37, -24.45) * mm});
            skLineSegment(sketch, "E341", {"start": v(33.37, -24.45) * mm, "end": v(32.96, -24.18) * mm});
            skLineSegment(sketch, "E342", {"start": v(32.96, -24.18) * mm, "end": v(32.87, -24.1) * mm});
            skLineSegment(sketch, "E343", {"start": v(32.87, -24.1) * mm, "end": v(32.77, -24.02) * mm});
            skLineSegment(sketch, "E344", {"start": v(32.77, -24.02) * mm, "end": v(32.44, -23.65) * mm});
            skLineSegment(sketch, "E345", {"start": v(32.44, -23.65) * mm, "end": v(32.19, -23.23) * mm});
            skLineSegment(sketch, "E346", {"start": v(32.19, -23.23) * mm, "end": v(32.02, -22.76) * mm});
            skLineSegment(sketch, "E347", {"start": v(32.02, -22.76) * mm, "end": v(31.95, -22.27) * mm});
            skLineSegment(sketch, "E348", {"start": v(31.95, -22.27) * mm, "end": v(31.98, -21.78) * mm});
            skLineSegment(sketch, "E349", {"start": v(31.98, -21.78) * mm, "end": v(32.01, -21.64) * mm});
            skLineSegment(sketch, "E350", {"start": v(32.01, -21.64) * mm, "end": v(32.02, -21.6) * mm});
            skLineSegment(sketch, "E351", {"start": v(32.02, -21.6) * mm, "end": v(32.05, -21.52) * mm});
            skLineSegment(sketch, "E352", {"start": v(32.05, -21.52) * mm, "end": v(32.1, -21.3) * mm});
            skLineSegment(sketch, "E353", {"start": v(32.1, -21.3) * mm, "end": v(32.1, -21.3) * mm});
            skLineSegment(sketch, "E354", {"start": v(32.1, -21.3) * mm, "end": v(32.14, -21.22) * mm});
            skLineSegment(sketch, "E355", {"start": v(32.14, -21.22) * mm, "end": v(32.17, -21.13) * mm});
            skLineSegment(sketch, "E356", {"start": v(32.17, -21.13) * mm, "end": v(32.17, -21.13) * mm});
            skLineSegment(sketch, "E357", {"start": v(32.17, -21.13) * mm, "end": v(32.27, -20.95) * mm});
            skLineSegment(sketch, "E358", {"start": v(32.27, -20.95) * mm, "end": v(32.31, -20.86) * mm});
            skLineSegment(sketch, "E359", {"start": v(32.31, -20.86) * mm, "end": v(32.34, -20.82) * mm});
            skLineSegment(sketch, "E360", {"start": v(32.34, -20.82) * mm, "end": v(32.4, -20.7) * mm});
            skLineSegment(sketch, "E361", {"start": v(32.4, -20.7) * mm, "end": v(32.73, -20.32) * mm});
            skLineSegment(sketch, "E362", {"start": v(32.73, -20.32) * mm, "end": v(33.11, -20.02) * mm});
            skLineSegment(sketch, "E363", {"start": v(33.11, -20.02) * mm, "end": v(33.55, -19.8) * mm});
            skLineSegment(sketch, "E364", {"start": v(33.55, -19.8) * mm, "end": v(34.02, -19.66) * mm});
            skLineSegment(sketch, "E365", {"start": v(34.02, -19.66) * mm, "end": v(34.51, -19.61) * mm});
            skLineSegment(sketch, "E366", {"start": v(34.51, -19.61) * mm, "end": v(34.65, -19.63) * mm});
            skLineSegment(sketch, "E367", {"start": v(34.65, -19.63) * mm, "end": v(34.76, -19.63) * mm});
            skLineSegment(sketch, "E368", {"start": v(34.76, -19.63) * mm, "end": v(35.24, -19.71) * mm});
            skLineSegment(sketch, "E369", {"start": v(35.24, -19.71) * mm, "end": v(35.36, -19.75) * mm});
            skLineSegment(sketch, "E370", {"start": v(35.36, -19.75) * mm, "end": v(35.56, -19.8) * mm});
            skLineSegment(sketch, "E371", {"start": v(35.56, -19.8) * mm, "end": v(35.76, -19.9) * mm});
            skLineSegment(sketch, "E372", {"start": v(35.76, -19.9) * mm, "end": v(35.95, -19.95) * mm});
            skLineSegment(sketch, "E373", {"start": v(35.95, -19.95) * mm, "end": v(35.98, -19.96) * mm});
            skLineSegment(sketch, "E374", {"start": v(35.98, -19.96) * mm, "end": v(36.2, -20.08) * mm});
            skLineSegment(sketch, "E375", {"start": v(36.2, -20.08) * mm, "end": v(36.28, -20.1) * mm});
            skLineSegment(sketch, "E376", {"start": v(36.28, -20.1) * mm, "end": v(36.72, -20.08) * mm});
            skLineSegment(sketch, "E377", {"start": v(36.72, -20.08) * mm, "end": v(37.2, -19.97) * mm});
            skLineSegment(sketch, "E378", {"start": v(37.2, -19.97) * mm, "end": v(37.6, -19.77) * mm});
            skLineSegment(sketch, "E379", {"start": v(37.6, -19.77) * mm, "end": v(37.65, -19.75) * mm});
            skLineSegment(sketch, "E380", {"start": v(37.65, -19.75) * mm, "end": v(37.91, -19.56) * mm});
            skLineSegment(sketch, "E381", {"start": v(37.91, -19.56) * mm, "end": v(38.08, -19.41) * mm});
            skLineSegment(sketch, "E382", {"start": v(38.08, -19.41) * mm, "end": v(38.19, -19.3) * mm});
            skLineSegment(sketch, "E383", {"start": v(38.19, -19.3) * mm, "end": v(38.43, -19) * mm});
            skLineSegment(sketch, "E384", {"start": v(38.43, -19) * mm, "end": v(38.66, -18.56) * mm});
            skLineSegment(sketch, "E385", {"start": v(38.66, -18.56) * mm, "end": v(38.66, -18.56) * mm});
            skLineSegment(sketch, "E386", {"start": v(38.66, -18.56) * mm, "end": v(38.8, -18.09) * mm});
            skLineSegment(sketch, "E387", {"start": v(38.8, -18.09) * mm, "end": v(38.84, -17.6) * mm});
            skLineSegment(sketch, "E388", {"start": v(38.84, -17.6) * mm, "end": v(38.79, -17.1) * mm});
            skLineSegment(sketch, "E389", {"start": v(38.79, -17.1) * mm, "end": v(38.64, -16.64) * mm});
            skLineSegment(sketch, "E390", {"start": v(38.64, -16.64) * mm, "end": v(38.4, -16.2) * mm});
            skLineSegment(sketch, "E391", {"start": v(38.4, -16.2) * mm, "end": v(38.27, -16.05) * mm});
            skLineSegment(sketch, "E392", {"start": v(38.27, -16.05) * mm, "end": v(38.14, -15.98) * mm});
            skLineSegment(sketch, "E393", {"start": v(38.14, -15.98) * mm, "end": v(38.14, -15.98) * mm});
            skLineSegment(sketch, "E394", {"start": v(38.14, -15.98) * mm, "end": v(38.06, -15.95) * mm});
            skLineSegment(sketch, "E395", {"start": v(38.06, -15.95) * mm, "end": v(37.76, -15.77) * mm});
            skLineSegment(sketch, "E396", {"start": v(37.76, -15.77) * mm, "end": v(37.63, -15.71) * mm});
            skLineSegment(sketch, "E397", {"start": v(37.63, -15.71) * mm, "end": v(37.4, -15.56) * mm});
            skLineSegment(sketch, "E398", {"start": v(37.4, -15.56) * mm, "end": v(37.29, -15.5) * mm});
            skLineSegment(sketch, "E399", {"start": v(37.29, -15.5) * mm, "end": v(37.1, -15.36) * mm});
            skLineSegment(sketch, "E400", {"start": v(37.1, -15.36) * mm, "end": v(37.03, -15.31) * mm});
            skLineSegment(sketch, "E401", {"start": v(37.03, -15.31) * mm, "end": v(36.67, -14.99) * mm});
            skLineSegment(sketch, "E402", {"start": v(36.67, -14.99) * mm, "end": v(36.6, -14.9) * mm});
            skLineSegment(sketch, "E403", {"start": v(36.6, -14.9) * mm, "end": v(36.55, -14.85) * mm});
            skLineSegment(sketch, "E404", {"start": v(36.55, -14.85) * mm, "end": v(36.4, -14.64) * mm});
            skLineSegment(sketch, "E405", {"start": v(36.4, -14.64) * mm, "end": v(36.37, -14.6) * mm});
            skLineSegment(sketch, "E406", {"start": v(36.37, -14.6) * mm, "end": v(36.36, -14.58) * mm});
            skLineSegment(sketch, "E407", {"start": v(36.36, -14.58) * mm, "end": v(36.27, -14.45) * mm});
            skLineSegment(sketch, "E408", {"start": v(36.27, -14.45) * mm, "end": v(36.08, -14) * mm});
            skLineSegment(sketch, "E409", {"start": v(36.08, -14) * mm, "end": v(35.98, -13.52) * mm});
            skLineSegment(sketch, "E410", {"start": v(35.98, -13.52) * mm, "end": v(35.97, -13.38) * mm});
            skLineSegment(sketch, "E411", {"start": v(35.97, -13.38) * mm, "end": v(35.97, -13.38) * mm});
            skLineSegment(sketch, "E412", {"start": v(35.97, -13.38) * mm, "end": v(35.97, -13.37) * mm});
            skLineSegment(sketch, "E413", {"start": v(35.97, -13.37) * mm, "end": v(35.97, -13.02) * mm});
            skLineSegment(sketch, "E414", {"start": v(35.97, -13.02) * mm, "end": v(35.99, -12.92) * mm});
            skLineSegment(sketch, "E415", {"start": v(35.99, -12.92) * mm, "end": v(36, -12.89) * mm});
            skLineSegment(sketch, "E416", {"start": v(36, -12.89) * mm, "end": v(36.01, -12.8) * mm});
            skLineSegment(sketch, "E417", {"start": v(36.01, -12.8) * mm, "end": v(36.06, -12.54) * mm});
            skLineSegment(sketch, "E418", {"start": v(36.06, -12.54) * mm, "end": v(36.09, -12.47) * mm});
            skLineSegment(sketch, "E419", {"start": v(36.09, -12.47) * mm, "end": v(36.1, -12.4) * mm});
            skLineSegment(sketch, "E420", {"start": v(36.1, -12.4) * mm, "end": v(36.18, -12.23) * mm});
            skLineSegment(sketch, "E421", {"start": v(36.18, -12.23) * mm, "end": v(36.24, -12.08) * mm});
            skLineSegment(sketch, "E422", {"start": v(36.24, -12.08) * mm, "end": v(36.24, -12.08) * mm});
            skLineSegment(sketch, "E423", {"start": v(36.24, -12.08) * mm, "end": v(36.27, -12.04) * mm});
            skLineSegment(sketch, "E424", {"start": v(36.27, -12.04) * mm, "end": v(36.3, -11.96) * mm});
            skLineSegment(sketch, "E425", {"start": v(36.3, -11.96) * mm, "end": v(36.3, -11.96) * mm});
            skLineSegment(sketch, "E426", {"start": v(36.3, -11.96) * mm, "end": v(36.48, -11.72) * mm});
            skLineSegment(sketch, "E427", {"start": v(36.48, -11.72) * mm, "end": v(36.51, -11.67) * mm});
            skLineSegment(sketch, "E428", {"start": v(36.51, -11.67) * mm, "end": v(36.52, -11.66) * mm});
            skLineSegment(sketch, "E429", {"start": v(36.52, -11.66) * mm, "end": v(36.6, -11.56) * mm});
            skLineSegment(sketch, "E430", {"start": v(36.6, -11.56) * mm, "end": v(36.95, -11.23) * mm});
            skLineSegment(sketch, "E431", {"start": v(36.95, -11.23) * mm, "end": v(37.37, -10.97) * mm});
            skLineSegment(sketch, "E432", {"start": v(37.37, -10.97) * mm, "end": v(37.83, -10.8) * mm});
            skLineSegment(sketch, "E433", {"start": v(37.83, -10.8) * mm, "end": v(38.31, -10.71) * mm});
            skLineSegment(sketch, "E434", {"start": v(38.31, -10.71) * mm, "end": v(38.44, -10.72) * mm});
            skLineSegment(sketch, "E435", {"start": v(38.44, -10.72) * mm, "end": v(38.48, -10.71) * mm});
            skLineSegment(sketch, "E436", {"start": v(38.48, -10.71) * mm, "end": v(38.61, -10.72) * mm});
            skLineSegment(sketch, "E437", {"start": v(38.61, -10.72) * mm, "end": v(38.8, -10.73) * mm});
            skLineSegment(sketch, "E438", {"start": v(38.8, -10.73) * mm, "end": v(38.86, -10.74) * mm});
            skLineSegment(sketch, "E439", {"start": v(38.86, -10.74) * mm, "end": v(38.97, -10.75) * mm});
            skLineSegment(sketch, "E440", {"start": v(38.97, -10.75) * mm, "end": v(39.15, -10.8) * mm});
            skLineSegment(sketch, "E441", {"start": v(39.15, -10.8) * mm, "end": v(39.19, -10.8) * mm});
            skLineSegment(sketch, "E442", {"start": v(39.19, -10.8) * mm, "end": v(39.32, -10.85) * mm});
            skLineSegment(sketch, "E443", {"start": v(39.32, -10.85) * mm, "end": v(39.45, -10.89) * mm});
            skLineSegment(sketch, "E444", {"start": v(39.45, -10.89) * mm, "end": v(39.49, -10.9) * mm});
            skLineSegment(sketch, "E445", {"start": v(39.49, -10.9) * mm, "end": v(39.66, -10.96) * mm});
            skLineSegment(sketch, "E446", {"start": v(39.66, -10.96) * mm, "end": v(39.73, -11) * mm});
            skLineSegment(sketch, "E447", {"start": v(39.73, -11) * mm, "end": v(40, -11.11) * mm});
            skLineSegment(sketch, "E448", {"start": v(40, -11.11) * mm, "end": v(40.07, -11.16) * mm});
            skLineSegment(sketch, "E449", {"start": v(40.07, -11.16) * mm, "end": v(40.41, -11.32) * mm});
            skLineSegment(sketch, "E450", {"start": v(40.41, -11.32) * mm, "end": v(40.46, -11.35) * mm});
            skLineSegment(sketch, "E451", {"start": v(40.46, -11.35) * mm, "end": v(40.47, -11.36) * mm});
            skLineSegment(sketch, "E452", {"start": v(40.47, -11.36) * mm, "end": v(40.77, -11.52) * mm});
            skLineSegment(sketch, "E453", {"start": v(40.77, -11.52) * mm, "end": v(40.8, -11.53) * mm});
            skLineSegment(sketch, "E454", {"start": v(40.8, -11.53) * mm, "end": v(40.97, -11.54) * mm});
            skLineSegment(sketch, "E455", {"start": v(40.97, -11.54) * mm, "end": v(41.11, -11.54) * mm});
            skLineSegment(sketch, "E456", {"start": v(41.11, -11.54) * mm, "end": v(41.5, -11.5) * mm});
            skLineSegment(sketch, "E457", {"start": v(41.5, -11.5) * mm, "end": v(41.97, -11.35) * mm});
            skLineSegment(sketch, "E458", {"start": v(41.97, -11.35) * mm, "end": v(42.4, -11.12) * mm});
            skLineSegment(sketch, "E459", {"start": v(42.4, -11.12) * mm, "end": v(42.78, -10.8) * mm});
            skLineSegment(sketch, "E460", {"start": v(42.78, -10.8) * mm, "end": v(43.1, -10.42) * mm});
            skLineSegment(sketch, "E461", {"start": v(43.1, -10.42) * mm, "end": v(43.1, -10.42) * mm});
            skLineSegment(sketch, "E462", {"start": v(43.1, -10.42) * mm, "end": v(43.32, -9.99) * mm});
            skLineSegment(sketch, "E463", {"start": v(43.32, -9.99) * mm, "end": v(43.47, -9.52) * mm});
            skLineSegment(sketch, "E464", {"start": v(43.47, -9.52) * mm, "end": v(43.51, -9.03) * mm});
            skLineSegment(sketch, "E465", {"start": v(43.51, -9.03) * mm, "end": v(43.46, -8.54) * mm});
            skLineSegment(sketch, "E466", {"start": v(43.46, -8.54) * mm, "end": v(43.34, -8.14) * mm});
            skLineSegment(sketch, "E467", {"start": v(43.34, -8.14) * mm, "end": v(43.3, -8.04) * mm});
            skLineSegment(sketch, "E468", {"start": v(43.3, -8.04) * mm, "end": v(43.2, -7.86) * mm});
            skLineSegment(sketch, "E469", {"start": v(43.2, -7.86) * mm, "end": v(43.02, -7.56) * mm});
            skLineSegment(sketch, "E470", {"start": v(43.02, -7.56) * mm, "end": v(42.97, -7.5) * mm});
            skLineSegment(sketch, "E471", {"start": v(42.97, -7.5) * mm, "end": v(42.9, -7.47) * mm});
            skLineSegment(sketch, "E472", {"start": v(42.9, -7.47) * mm, "end": v(42.79, -7.38) * mm});
            skLineSegment(sketch, "E473", {"start": v(42.79, -7.38) * mm, "end": v(42.53, -7.23) * mm});
            skLineSegment(sketch, "E474", {"start": v(42.53, -7.23) * mm, "end": v(42.43, -7.14) * mm});
            skLineSegment(sketch, "E475", {"start": v(42.43, -7.14) * mm, "end": v(42.25, -7.02) * mm});
            skLineSegment(sketch, "E476", {"start": v(42.25, -7.02) * mm, "end": v(42.13, -6.9) * mm});
            skLineSegment(sketch, "E477", {"start": v(42.13, -6.9) * mm, "end": v(42.05, -6.84) * mm});
            skLineSegment(sketch, "E478", {"start": v(42.05, -6.84) * mm, "end": v(41.73, -6.47) * mm});
            skLineSegment(sketch, "E479", {"start": v(41.73, -6.47) * mm, "end": v(41.63, -6.3) * mm});
            skLineSegment(sketch, "E480", {"start": v(41.63, -6.3) * mm, "end": v(41.63, -6.3) * mm});
            skLineSegment(sketch, "E481", {"start": v(41.63, -6.3) * mm, "end": v(41.48, -6.04) * mm});
            skLineSegment(sketch, "E482", {"start": v(41.48, -6.04) * mm, "end": v(41.43, -5.92) * mm});
            skLineSegment(sketch, "E483", {"start": v(41.43, -5.92) * mm, "end": v(41.42, -5.9) * mm});
            skLineSegment(sketch, "E484", {"start": v(41.42, -5.9) * mm, "end": v(41.4, -5.87) * mm});
            skLineSegment(sketch, "E485", {"start": v(41.4, -5.87) * mm, "end": v(41.37, -5.73) * mm});
            skLineSegment(sketch, "E486", {"start": v(41.37, -5.73) * mm, "end": v(41.32, -5.58) * mm});
            skLineSegment(sketch, "E487", {"start": v(41.32, -5.58) * mm, "end": v(41.3, -5.5) * mm});
            skLineSegment(sketch, "E488", {"start": v(41.3, -5.5) * mm, "end": v(41.27, -5.4) * mm});
            skLineSegment(sketch, "E489", {"start": v(41.27, -5.4) * mm, "end": v(41.25, -5.11) * mm});
            skLineSegment(sketch, "E490", {"start": v(41.25, -5.11) * mm, "end": v(41.25, -5.09) * mm});
            skLineSegment(sketch, "E491", {"start": v(41.25, -5.09) * mm, "end": v(41.25, -5.08) * mm});
            skLineSegment(sketch, "E492", {"start": v(41.25, -5.08) * mm, "end": v(41.23, -4.9) * mm});
            skLineSegment(sketch, "E493", {"start": v(41.23, -4.9) * mm, "end": v(41.3, -4.41) * mm});
            skLineSegment(sketch, "E494", {"start": v(41.3, -4.41) * mm, "end": v(41.44, -3.94) * mm});
            skLineSegment(sketch, "E495", {"start": v(41.44, -3.94) * mm, "end": v(41.69, -3.51) * mm});
            skLineSegment(sketch, "E496", {"start": v(41.69, -3.51) * mm, "end": v(41.69, -3.51) * mm});
            skLineSegment(sketch, "E497", {"start": v(41.69, -3.51) * mm, "end": v(42, -3.14) * mm});
            skLineSegment(sketch, "E498", {"start": v(42, -3.14) * mm, "end": v(42.4, -2.83) * mm});
            skLineSegment(sketch, "E499", {"start": v(42.4, -2.83) * mm, "end": v(42.83, -2.6) * mm});
            skLineSegment(sketch, "E500", {"start": v(42.83, -2.6) * mm, "end": v(43.3, -2.48) * mm});
            skLineSegment(sketch, "E501", {"start": v(43.3, -2.48) * mm, "end": v(43.8, -2.44) * mm});
            skLineSegment(sketch, "E502", {"start": v(43.8, -2.44) * mm, "end": v(43.97, -2.46) * mm});
            skLineSegment(sketch, "E503", {"start": v(43.97, -2.46) * mm, "end": v(44.01, -2.46) * mm});
            skLineSegment(sketch, "E504", {"start": v(44.01, -2.46) * mm, "end": v(44.1, -2.47) * mm});
            skLineSegment(sketch, "E505", {"start": v(44.1, -2.47) * mm, "end": v(44.29, -2.5) * mm});
            skLineSegment(sketch, "E506", {"start": v(44.29, -2.5) * mm, "end": v(44.36, -2.52) * mm});
            skLineSegment(sketch, "E507", {"start": v(44.36, -2.52) * mm, "end": v(44.5, -2.54) * mm});
            skLineSegment(sketch, "E508", {"start": v(44.5, -2.54) * mm, "end": v(44.96, -2.72) * mm});
            skLineSegment(sketch, "E509", {"start": v(44.96, -2.72) * mm, "end": v(45.05, -2.78) * mm});
            skLineSegment(sketch, "E510", {"start": v(45.05, -2.78) * mm, "end": v(45.23, -2.86) * mm});
            skLineSegment(sketch, "E511", {"start": v(45.23, -2.86) * mm, "end": v(45.39, -2.98) * mm});
            skLineSegment(sketch, "E512", {"start": v(45.39, -2.98) * mm, "end": v(45.57, -3.08) * mm});
            skLineSegment(sketch, "E513", {"start": v(45.57, -3.08) * mm, "end": v(45.6, -3.1) * mm});
            skLineSegment(sketch, "E514", {"start": v(45.6, -3.1) * mm, "end": v(45.72, -3.2) * mm});
            skLineSegment(sketch, "E515", {"start": v(45.72, -3.2) * mm, "end": v(45.8, -3.23) * mm});
            skLineSegment(sketch, "E516", {"start": v(45.8, -3.23) * mm, "end": v(45.98, -3.28) * mm});
            skLineSegment(sketch, "E517", {"start": v(45.98, -3.28) * mm, "end": v(46.01, -3.29) * mm});
            skLineSegment(sketch, "E518", {"start": v(46.01, -3.29) * mm, "end": v(46.03, -3.29) * mm});
            skLineSegment(sketch, "E519", {"start": v(46.03, -3.29) * mm, "end": v(46.49, -3.33) * mm});
            skLineSegment(sketch, "E520", {"start": v(46.49, -3.33) * mm, "end": v(46.98, -3.27) * mm});
            skLineSegment(sketch, "E521", {"start": v(46.98, -3.27) * mm, "end": v(47.45, -3.12) * mm});
            skLineSegment(sketch, "E522", {"start": v(47.45, -3.12) * mm, "end": v(47.88, -2.89) * mm});
            skLineSegment(sketch, "E523", {"start": v(47.88, -2.89) * mm, "end": v(48.26, -2.57) * mm});
            skLineSegment(sketch, "E524", {"start": v(48.26, -2.57) * mm, "end": v(48.56, -2.18) * mm});
            skLineSegment(sketch, "E525", {"start": v(48.56, -2.18) * mm, "end": v(48.57, -2.18) * mm});
            skLineSegment(sketch, "E526", {"start": v(48.57, -2.18) * mm, "end": v(48.8, -1.74) * mm});
            skLineSegment(sketch, "E527", {"start": v(48.8, -1.74) * mm, "end": v(48.9, -1.34) * mm});
            skLineSegment(sketch, "E528", {"start": v(48.9, -1.34) * mm, "end": v(48.93, -1.24) * mm});
            skLineSegment(sketch, "E529", {"start": v(48.93, -1.24) * mm, "end": v(48.96, -0.95) * mm});
            skLineSegment(sketch, "E530", {"start": v(48.96, -0.95) * mm, "end": v(48.96, -0.7) * mm});
            skLineSegment(sketch, "E531", {"start": v(48.96, -0.7) * mm, "end": v(48.95, -0.56) * mm});
            skLineSegment(sketch, "E532", {"start": v(48.95, -0.56) * mm, "end": v(48.88, -0.18) * mm});
            skLineSegment(sketch, "E533", {"start": v(48.88, -0.18) * mm, "end": v(48.88, -0.17) * mm});
            skLineSegment(sketch, "E534", {"start": v(48.88, -0.17) * mm, "end": v(48.7, 0.28) * mm});
            skLineSegment(sketch, "E535", {"start": v(48.7, 0.28) * mm, "end": v(48.44, 0.7) * mm});
            skLineSegment(sketch, "E536", {"start": v(48.44, 0.7) * mm, "end": v(48.22, 0.94) * mm});
            skLineSegment(sketch, "E537", {"start": v(48.22, 0.94) * mm, "end": v(48.13, 1.02) * mm});
            skLineSegment(sketch, "E538", {"start": v(48.13, 1.02) * mm, "end": v(47.76, 1.2) * mm});
            skLineSegment(sketch, "E539", {"start": v(47.76, 1.2) * mm, "end": v(47.66, 1.27) * mm});
            skLineSegment(sketch, "E540", {"start": v(47.66, 1.27) * mm, "end": v(47.52, 1.34) * mm});
            skLineSegment(sketch, "E541", {"start": v(47.52, 1.34) * mm, "end": v(47.39, 1.45) * mm});
            skLineSegment(sketch, "E542", {"start": v(47.39, 1.45) * mm, "end": v(47.36, 1.47) * mm});
            skLineSegment(sketch, "E543", {"start": v(47.36, 1.47) * mm, "end": v(47.3, 1.52) * mm});
            skLineSegment(sketch, "E544", {"start": v(47.3, 1.52) * mm, "end": v(47.14, 1.65) * mm});
            skLineSegment(sketch, "E545", {"start": v(47.14, 1.65) * mm, "end": v(47.1, 1.71) * mm});
            skLineSegment(sketch, "E546", {"start": v(47.1, 1.71) * mm, "end": v(47, 1.8) * mm});
            skLineSegment(sketch, "E547", {"start": v(47, 1.8) * mm, "end": v(46.7, 2.2) * mm});
            skLineSegment(sketch, "E548", {"start": v(46.7, 2.2) * mm, "end": v(46.5, 2.64) * mm});
            skLineSegment(sketch, "E549", {"start": v(46.5, 2.64) * mm, "end": v(46.37, 3.12) * mm});
            skLineSegment(sketch, "E550", {"start": v(46.37, 3.12) * mm, "end": v(46.35, 3.62) * mm});
            skLineSegment(sketch, "E551", {"start": v(46.35, 3.62) * mm, "end": v(46.42, 4.1) * mm});
            skLineSegment(sketch, "E552", {"start": v(46.42, 4.1) * mm, "end": v(46.6, 4.57) * mm});
            skLineSegment(sketch, "E553", {"start": v(46.6, 4.57) * mm, "end": v(46.6, 4.57) * mm});
            skLineSegment(sketch, "E554", {"start": v(46.6, 4.57) * mm, "end": v(46.66, 4.69) * mm});
            skLineSegment(sketch, "E555", {"start": v(46.66, 4.69) * mm, "end": v(46.67, 4.7) * mm});
            skLineSegment(sketch, "E556", {"start": v(46.67, 4.7) * mm, "end": v(46.67, 4.7) * mm});
            skLineSegment(sketch, "E557", {"start": v(46.67, 4.7) * mm, "end": v(46.7, 4.75) * mm});
            skLineSegment(sketch, "E558", {"start": v(46.7, 4.75) * mm, "end": v(46.85, 5) * mm});
            skLineSegment(sketch, "E559", {"start": v(46.85, 5) * mm, "end": v(46.92, 5.07) * mm});
            skLineSegment(sketch, "E560", {"start": v(46.92, 5.07) * mm, "end": v(46.95, 5.12) * mm});
            skLineSegment(sketch, "E561", {"start": v(46.95, 5.12) * mm, "end": v(47.05, 5.22) * mm});
            skLineSegment(sketch, "E562", {"start": v(47.05, 5.22) * mm, "end": v(47.18, 5.36) * mm});
            skLineSegment(sketch, "E563", {"start": v(47.18, 5.36) * mm, "end": v(47.23, 5.4) * mm});
            skLineSegment(sketch, "E564", {"start": v(47.23, 5.4) * mm, "end": v(47.3, 5.46) * mm});
            skLineSegment(sketch, "E565", {"start": v(47.3, 5.46) * mm, "end": v(47.5, 5.6) * mm});
            skLineSegment(sketch, "E566", {"start": v(47.5, 5.6) * mm, "end": v(47.57, 5.65) * mm});
            skLineSegment(sketch, "E567", {"start": v(47.57, 5.65) * mm, "end": v(47.6, 5.67) * mm});
            skLineSegment(sketch, "E568", {"start": v(47.6, 5.67) * mm, "end": v(47.71, 5.73) * mm});
            skLineSegment(sketch, "E569", {"start": v(47.71, 5.73) * mm, "end": v(48.17, 5.92) * mm});
            skLineSegment(sketch, "E570", {"start": v(48.17, 5.92) * mm, "end": v(48.65, 6.01) * mm});
            skLineSegment(sketch, "E571", {"start": v(48.65, 6.01) * mm, "end": v(49.15, 6.01) * mm});
            skLineSegment(sketch, "E572", {"start": v(49.15, 6.01) * mm, "end": v(49.33, 5.97) * mm});
            skLineSegment(sketch, "E573", {"start": v(49.33, 5.97) * mm, "end": v(49.37, 5.97) * mm});
            skLineSegment(sketch, "E574", {"start": v(49.37, 5.97) * mm, "end": v(49.48, 5.94) * mm});
            skLineSegment(sketch, "E575", {"start": v(49.48, 5.94) * mm, "end": v(49.63, 5.91) * mm});
            skLineSegment(sketch, "E576", {"start": v(49.63, 5.91) * mm, "end": v(49.68, 5.89) * mm});
            skLineSegment(sketch, "E577", {"start": v(49.68, 5.89) * mm, "end": v(49.85, 5.84) * mm});
            skLineSegment(sketch, "E578", {"start": v(49.85, 5.84) * mm, "end": v(50.03, 5.76) * mm});
            skLineSegment(sketch, "E579", {"start": v(50.03, 5.76) * mm, "end": v(50.14, 5.72) * mm});
            skLineSegment(sketch, "E580", {"start": v(50.14, 5.72) * mm, "end": v(50.37, 5.6) * mm});
            skLineSegment(sketch, "E581", {"start": v(50.37, 5.6) * mm, "end": v(50.42, 5.59) * mm});
            skLineSegment(sketch, "E582", {"start": v(50.42, 5.59) * mm, "end": v(50.84, 5.55) * mm});
            skLineSegment(sketch, "E583", {"start": v(50.84, 5.55) * mm, "end": v(51.31, 5.6) * mm});
            skLineSegment(sketch, "E584", {"start": v(51.31, 5.6) * mm, "end": v(51.33, 5.6) * mm});
            skLineSegment(sketch, "E585", {"start": v(51.33, 5.6) * mm, "end": v(51.35, 5.6) * mm});
            skLineSegment(sketch, "E586", {"start": v(51.35, 5.6) * mm, "end": v(51.4, 5.62) * mm});
            skLineSegment(sketch, "E587", {"start": v(51.4, 5.62) * mm, "end": v(51.65, 5.7) * mm});
            skLineSegment(sketch, "E588", {"start": v(51.65, 5.7) * mm, "end": v(51.83, 5.76) * mm});
            skLineSegment(sketch, "E589", {"start": v(51.83, 5.76) * mm, "end": v(51.89, 5.79) * mm});
            skLineSegment(sketch, "E590", {"start": v(51.89, 5.79) * mm, "end": v(51.97, 5.83) * mm});
            skLineSegment(sketch, "E591", {"start": v(51.97, 5.83) * mm, "end": v(52.34, 6.06) * mm});
            skLineSegment(sketch, "E592", {"start": v(52.34, 6.06) * mm, "end": v(52.7, 6.4) * mm});
            skLineSegment(sketch, "E593", {"start": v(52.7, 6.4) * mm, "end": v(52.98, 6.8) * mm});
            skLineSegment(sketch, "E594", {"start": v(52.98, 6.8) * mm, "end": v(53.18, 7.26) * mm});
            skLineSegment(sketch, "E595", {"start": v(53.18, 7.26) * mm, "end": v(53.18, 7.26) * mm});
            skLineSegment(sketch, "E596", {"start": v(53.18, 7.26) * mm, "end": v(53.29, 7.74) * mm});
            skLineSegment(sketch, "E597", {"start": v(53.29, 7.74) * mm, "end": v(53.3, 8.23) * mm});
            skLineSegment(sketch, "E598", {"start": v(53.3, 8.23) * mm, "end": v(53.22, 8.72) * mm});
            skLineSegment(sketch, "E599", {"start": v(53.22, 8.72) * mm, "end": v(53.04, 9.18) * mm});
            skLineSegment(sketch, "E600", {"start": v(53.04, 9.18) * mm, "end": v(52.78, 9.6) * mm});
            skLineSegment(sketch, "E601", {"start": v(52.78, 9.6) * mm, "end": v(52.44, 9.95) * mm});
            skLineSegment(sketch, "E602", {"start": v(52.44, 9.95) * mm, "end": v(52.43, 9.96) * mm});
            skLineSegment(sketch, "E603", {"start": v(52.43, 9.96) * mm, "end": v(52.26, 10.08) * mm});
            skLineSegment(sketch, "E604", {"start": v(52.26, 10.08) * mm, "end": v(51.97, 10.26) * mm});
            skLineSegment(sketch, "E605", {"start": v(51.97, 10.26) * mm, "end": v(51.86, 10.27) * mm});
            skLineSegment(sketch, "E606", {"start": v(51.86, 10.27) * mm, "end": v(51.75, 10.3) * mm});
            skLineSegment(sketch, "E607", {"start": v(51.75, 10.3) * mm, "end": v(51.47, 10.35) * mm});
            skLineSegment(sketch, "E608", {"start": v(51.47, 10.35) * mm, "end": v(51.26, 10.43) * mm});
            skLineSegment(sketch, "E609", {"start": v(51.26, 10.43) * mm, "end": v(51.2, 10.44) * mm});
            skLineSegment(sketch, "E610", {"start": v(51.2, 10.44) * mm, "end": v(51.1, 10.5) * mm});
            skLineSegment(sketch, "E611", {"start": v(51.1, 10.5) * mm, "end": v(51.01, 10.53) * mm});
            skLineSegment(sketch, "E612", {"start": v(51.01, 10.53) * mm, "end": v(50.97, 10.55) * mm});
            skLineSegment(sketch, "E613", {"start": v(50.97, 10.55) * mm, "end": v(50.76, 10.65) * mm});
            skLineSegment(sketch, "E614", {"start": v(50.76, 10.65) * mm, "end": v(50.36, 10.94) * mm});
            skLineSegment(sketch, "E615", {"start": v(50.36, 10.94) * mm, "end": v(50.02, 11.3) * mm});
            skLineSegment(sketch, "E616", {"start": v(50.02, 11.3) * mm, "end": v(49.77, 11.72) * mm});
            skLineSegment(sketch, "E617", {"start": v(49.77, 11.72) * mm, "end": v(49.6, 12.19) * mm});
            skLineSegment(sketch, "E618", {"start": v(49.6, 12.19) * mm, "end": v(49.52, 12.67) * mm});
            skLineSegment(sketch, "E619", {"start": v(49.52, 12.67) * mm, "end": v(49.53, 12.85) * mm});
            skLineSegment(sketch, "E620", {"start": v(49.53, 12.85) * mm, "end": v(49.52, 12.87) * mm});
            skLineSegment(sketch, "E621", {"start": v(49.52, 12.87) * mm, "end": v(49.53, 12.92) * mm});
            skLineSegment(sketch, "E622", {"start": v(49.53, 12.92) * mm, "end": v(49.53, 13.04) * mm});
            skLineSegment(sketch, "E623", {"start": v(49.53, 13.04) * mm, "end": v(49.54, 13.17) * mm});
            skLineSegment(sketch, "E624", {"start": v(49.54, 13.17) * mm, "end": v(49.54, 13.17) * mm});
            skLineSegment(sketch, "E625", {"start": v(49.54, 13.17) * mm, "end": v(49.57, 13.3) * mm});
            skLineSegment(sketch, "E626", {"start": v(49.57, 13.3) * mm, "end": v(49.58, 13.37) * mm});
            skLineSegment(sketch, "E627", {"start": v(49.58, 13.37) * mm, "end": v(49.58, 13.37) * mm});
            skLineSegment(sketch, "E628", {"start": v(49.58, 13.37) * mm, "end": v(49.62, 13.5) * mm});
            skLineSegment(sketch, "E629", {"start": v(49.62, 13.5) * mm, "end": v(49.65, 13.65) * mm});
            skLineSegment(sketch, "E630", {"start": v(49.65, 13.65) * mm, "end": v(49.69, 13.72) * mm});
            skLineSegment(sketch, "E631", {"start": v(49.69, 13.72) * mm, "end": v(49.72, 13.84) * mm});
            skLineSegment(sketch, "E632", {"start": v(49.72, 13.84) * mm, "end": v(49.84, 14.04) * mm});
            skLineSegment(sketch, "E633", {"start": v(49.84, 14.04) * mm, "end": v(49.86, 14.1) * mm});
            skLineSegment(sketch, "E634", {"start": v(49.86, 14.1) * mm, "end": v(49.88, 14.12) * mm});
            skLineSegment(sketch, "E635", {"start": v(49.88, 14.12) * mm, "end": v(49.96, 14.27) * mm});
            skLineSegment(sketch, "E636", {"start": v(49.96, 14.27) * mm, "end": v(50.28, 14.65) * mm});
            skLineSegment(sketch, "E637", {"start": v(50.28, 14.65) * mm, "end": v(50.66, 14.96) * mm});
            skLineSegment(sketch, "E638", {"start": v(50.66, 14.96) * mm, "end": v(51.1, 15.19) * mm});
            skLineSegment(sketch, "E639", {"start": v(51.1, 15.19) * mm, "end": v(51.57, 15.33) * mm});
            skLineSegment(sketch, "E640", {"start": v(51.57, 15.33) * mm, "end": v(51.85, 15.35) * mm});
            skLineSegment(sketch, "E641", {"start": v(51.85, 15.35) * mm, "end": v(51.87, 15.36) * mm});
            skLineSegment(sketch, "E642", {"start": v(51.87, 15.36) * mm, "end": v(51.9, 15.36) * mm});
            skLineSegment(sketch, "E643", {"start": v(51.9, 15.36) * mm, "end": v(52.06, 15.37) * mm});
            skLineSegment(sketch, "E644", {"start": v(52.06, 15.37) * mm, "end": v(52.15, 15.36) * mm});
            skLineSegment(sketch, "E645", {"start": v(52.15, 15.36) * mm, "end": v(52.26, 15.36) * mm});
            skLineSegment(sketch, "E646", {"start": v(52.26, 15.36) * mm, "end": v(52.36, 15.37) * mm});
            skLineSegment(sketch, "E647", {"start": v(52.36, 15.37) * mm, "end": v(52.7, 15.3) * mm});
            skLineSegment(sketch, "E648", {"start": v(52.7, 15.3) * mm, "end": v(52.78, 15.3) * mm});
            skLineSegment(sketch, "E649", {"start": v(52.78, 15.3) * mm, "end": v(52.84, 15.3) * mm});
            skLineSegment(sketch, "E650", {"start": v(52.84, 15.3) * mm, "end": v(53.1, 15.34) * mm});
            skLineSegment(sketch, "E651", {"start": v(53.1, 15.34) * mm, "end": v(53.35, 15.4) * mm});
            skLineSegment(sketch, "E652", {"start": v(53.35, 15.4) * mm, "end": v(53.8, 15.63) * mm});
            skLineSegment(sketch, "E653", {"start": v(53.8, 15.63) * mm, "end": v(54.19, 15.93) * mm});
            skLineSegment(sketch, "E654", {"start": v(54.19, 15.93) * mm, "end": v(54.51, 16.3) * mm});
            skLineSegment(sketch, "E655", {"start": v(54.51, 16.3) * mm, "end": v(54.76, 16.72) * mm});
            skLineSegment(sketch, "E656", {"start": v(54.76, 16.72) * mm, "end": v(54.92, 17.2) * mm});
            skLineSegment(sketch, "E657", {"start": v(54.92, 17.2) * mm, "end": v(54.98, 17.66) * mm});
            skLineSegment(sketch, "E658", {"start": v(54.98, 17.66) * mm, "end": v(54.98, 17.7) * mm});
            skLineSegment(sketch, "E659", {"start": v(54.98, 17.7) * mm, "end": v(54.96, 18.06) * mm});
            skLineSegment(sketch, "E660", {"start": v(54.96, 18.06) * mm, "end": v(54.94, 18.23) * mm});
            skLineSegment(sketch, "E661", {"start": v(54.94, 18.23) * mm, "end": v(54.88, 18.44) * mm});
            skLineSegment(sketch, "E662", {"start": v(54.88, 18.44) * mm, "end": v(54.78, 18.75) * mm});
            skLineSegment(sketch, "E663", {"start": v(54.78, 18.75) * mm, "end": v(54.75, 18.81) * mm});
            skLineSegment(sketch, "E664", {"start": v(54.75, 18.81) * mm, "end": v(54.53, 19.2) * mm});
            skLineSegment(sketch, "E665", {"start": v(54.53, 19.2) * mm, "end": v(54.2, 19.57) * mm});
            skLineSegment(sketch, "E666", {"start": v(54.2, 19.57) * mm, "end": v(53.81, 19.87) * mm});
            skLineSegment(sketch, "E667", {"start": v(53.81, 19.87) * mm, "end": v(53.37, 20.1) * mm});
            skLineSegment(sketch, "E668", {"start": v(53.37, 20.1) * mm, "end": v(53.07, 20.17) * mm});
            skLineSegment(sketch, "E669", {"start": v(53.07, 20.17) * mm, "end": v(52.88, 20.21) * mm});
            skLineSegment(sketch, "E670", {"start": v(52.88, 20.21) * mm, "end": v(52.74, 20.18) * mm});
            skLineSegment(sketch, "E671", {"start": v(52.74, 20.18) * mm, "end": v(52.67, 20.18) * mm});
            skLineSegment(sketch, "E672", {"start": v(52.67, 20.18) * mm, "end": v(52.6, 20.18) * mm});
            skLineSegment(sketch, "E673", {"start": v(52.6, 20.18) * mm, "end": v(52.37, 20.14) * mm});
            skLineSegment(sketch, "E674", {"start": v(52.37, 20.14) * mm, "end": v(52.15, 20.15) * mm});
            skLineSegment(sketch, "E675", {"start": v(52.15, 20.15) * mm, "end": v(52.1, 20.14) * mm});
            skLineSegment(sketch, "E676", {"start": v(52.1, 20.14) * mm, "end": v(51.98, 20.16) * mm});
            skLineSegment(sketch, "E677", {"start": v(51.98, 20.16) * mm, "end": v(51.88, 20.16) * mm});
            skLineSegment(sketch, "E678", {"start": v(51.88, 20.16) * mm, "end": v(51.83, 20.17) * mm});
            skLineSegment(sketch, "E679", {"start": v(51.83, 20.17) * mm, "end": v(51.6, 20.2) * mm});
            skLineSegment(sketch, "E680", {"start": v(51.6, 20.2) * mm, "end": v(51.13, 20.34) * mm});
            skLineSegment(sketch, "E681", {"start": v(51.13, 20.34) * mm, "end": v(50.7, 20.58) * mm});
            skLineSegment(sketch, "E682", {"start": v(50.7, 20.58) * mm, "end": v(50.32, 20.9) * mm});
            skLineSegment(sketch, "E683", {"start": v(50.32, 20.9) * mm, "end": v(50.01, 21.28) * mm});
            skLineSegment(sketch, "E684", {"start": v(50.01, 21.28) * mm, "end": v(49.94, 21.42) * mm});
            skLineSegment(sketch, "E685", {"start": v(49.94, 21.42) * mm, "end": v(49.92, 21.45) * mm});
            skLineSegment(sketch, "E686", {"start": v(49.92, 21.45) * mm, "end": v(49.89, 21.52) * mm});
            skLineSegment(sketch, "E687", {"start": v(49.89, 21.52) * mm, "end": v(49.78, 21.72) * mm});
            skLineSegment(sketch, "E688", {"start": v(49.78, 21.72) * mm, "end": v(49.75, 21.82) * mm});
            skLineSegment(sketch, "E689", {"start": v(49.75, 21.82) * mm, "end": v(49.72, 21.9) * mm});
            skLineSegment(sketch, "E690", {"start": v(49.72, 21.9) * mm, "end": v(49.68, 22.08) * mm});
            skLineSegment(sketch, "E691", {"start": v(49.68, 22.08) * mm, "end": v(49.65, 22.2) * mm});
            skLineSegment(sketch, "E692", {"start": v(49.65, 22.2) * mm, "end": v(49.65, 22.2) * mm});
            skLineSegment(sketch, "E693", {"start": v(49.65, 22.2) * mm, "end": v(49.64, 22.25) * mm});
            skLineSegment(sketch, "E694", {"start": v(49.64, 22.25) * mm, "end": v(49.61, 22.38) * mm});
            skLineSegment(sketch, "E695", {"start": v(49.61, 22.38) * mm, "end": v(49.61, 22.38) * mm});
            skLineSegment(sketch, "E696", {"start": v(49.61, 22.38) * mm, "end": v(49.6, 22.66) * mm});
            skLineSegment(sketch, "E697", {"start": v(49.6, 22.66) * mm, "end": v(49.6, 22.69) * mm});
            skLineSegment(sketch, "E698", {"start": v(49.6, 22.69) * mm, "end": v(49.6, 22.7) * mm});
            skLineSegment(sketch, "E699", {"start": v(49.6, 22.7) * mm, "end": v(49.6, 22.88) * mm});
            skLineSegment(sketch, "E700", {"start": v(49.6, 22.88) * mm, "end": v(49.68, 23.36) * mm});
            skLineSegment(sketch, "E701", {"start": v(49.68, 23.36) * mm, "end": v(49.86, 23.82) * mm});
            skLineSegment(sketch, "E702", {"start": v(49.86, 23.82) * mm, "end": v(50.12, 24.24) * mm});
            skLineSegment(sketch, "E703", {"start": v(50.12, 24.24) * mm, "end": v(50.46, 24.6) * mm});
            skLineSegment(sketch, "E704", {"start": v(50.46, 24.6) * mm, "end": v(50.87, 24.88) * mm});
            skLineSegment(sketch, "E705", {"start": v(50.87, 24.88) * mm, "end": v(51.05, 24.96) * mm});
            skLineSegment(sketch, "E706", {"start": v(51.05, 24.96) * mm, "end": v(51.1, 25) * mm});
            skLineSegment(sketch, "E707", {"start": v(51.1, 25) * mm, "end": v(51.24, 25.05) * mm});
            skLineSegment(sketch, "E708", {"start": v(51.24, 25.05) * mm, "end": v(51.32, 25.08) * mm});
            skLineSegment(sketch, "E709", {"start": v(51.32, 25.08) * mm, "end": v(51.36, 25.1) * mm});
            skLineSegment(sketch, "E710", {"start": v(51.36, 25.1) * mm, "end": v(51.57, 25.17) * mm});
            skLineSegment(sketch, "E711", {"start": v(51.57, 25.17) * mm, "end": v(51.81, 25.2) * mm});
            skLineSegment(sketch, "E712", {"start": v(51.81, 25.2) * mm, "end": v(51.94, 25.25) * mm});
            skLineSegment(sketch, "E713", {"start": v(51.94, 25.25) * mm, "end": v(52.1, 25.26) * mm});
            skLineSegment(sketch, "E714", {"start": v(52.1, 25.26) * mm, "end": v(52.3, 25.37) * mm});
            skLineSegment(sketch, "E715", {"start": v(52.3, 25.37) * mm, "end": v(52.54, 25.52) * mm});
            skLineSegment(sketch, "E716", {"start": v(52.54, 25.52) * mm, "end": v(52.9, 25.86) * mm});
            skLineSegment(sketch, "E717", {"start": v(52.9, 25.86) * mm, "end": v(53.18, 26.27) * mm});
            skLineSegment(sketch, "E718", {"start": v(53.18, 26.27) * mm, "end": v(53.37, 26.72) * mm});
            skLineSegment(sketch, "E719", {"start": v(53.37, 26.72) * mm, "end": v(53.47, 27.17) * mm});
            skLineSegment(sketch, "E720", {"start": v(53.47, 27.17) * mm, "end": v(53.48, 27.22) * mm});
            skLineSegment(sketch, "E721", {"start": v(53.48, 27.22) * mm, "end": v(53.49, 27.57) * mm});
            skLineSegment(sketch, "E722", {"start": v(53.49, 27.57) * mm, "end": v(53.48, 27.76) * mm});
            skLineSegment(sketch, "E723", {"start": v(53.48, 27.76) * mm, "end": v(53.44, 27.96) * mm});
            skLineSegment(sketch, "E724", {"start": v(53.44, 27.96) * mm, "end": v(53.36, 28.29) * mm});
            skLineSegment(sketch, "E725", {"start": v(53.36, 28.29) * mm, "end": v(53.34, 28.34) * mm});
            skLineSegment(sketch, "E726", {"start": v(53.34, 28.34) * mm, "end": v(53.15, 28.75) * mm});
            skLineSegment(sketch, "E727", {"start": v(53.15, 28.75) * mm, "end": v(52.85, 29.15) * mm});
            skLineSegment(sketch, "E728", {"start": v(52.85, 29.15) * mm, "end": v(52.49, 29.48) * mm});
            skLineSegment(sketch, "E729", {"start": v(52.49, 29.48) * mm, "end": v(52.07, 29.74) * mm});
            skLineSegment(sketch, "E730", {"start": v(52.07, 29.74) * mm, "end": v(51.6, 29.9) * mm});
            skLineSegment(sketch, "E731", {"start": v(51.6, 29.9) * mm, "end": v(51.12, 29.98) * mm});
            skLineSegment(sketch, "E732", {"start": v(51.12, 29.98) * mm, "end": v(50.9, 29.97) * mm});
            skLineSegment(sketch, "E733", {"start": v(50.9, 29.97) * mm, "end": v(50.6, 29.94) * mm});
            skLineSegment(sketch, "E734", {"start": v(50.6, 29.94) * mm, "end": v(50.37, 29.8) * mm});
            skLineSegment(sketch, "E735", {"start": v(50.37, 29.8) * mm, "end": v(50.3, 29.78) * mm});
            skLineSegment(sketch, "E736", {"start": v(50.3, 29.78) * mm, "end": v(50.21, 29.75) * mm});
            skLineSegment(sketch, "E737", {"start": v(50.21, 29.75) * mm, "end": v(50.05, 29.67) * mm});
            skLineSegment(sketch, "E738", {"start": v(50.05, 29.67) * mm, "end": v(49.58, 29.55) * mm});
            skLineSegment(sketch, "E739", {"start": v(49.58, 29.55) * mm, "end": v(49.56, 29.55) * mm});
            skLineSegment(sketch, "E740", {"start": v(49.56, 29.55) * mm, "end": v(49.45, 29.54) * mm});
            skLineSegment(sketch, "E741", {"start": v(49.45, 29.54) * mm, "end": v(49.34, 29.52) * mm});
            skLineSegment(sketch, "E742", {"start": v(49.34, 29.52) * mm, "end": v(49.1, 29.52) * mm});
            skLineSegment(sketch, "E743", {"start": v(49.1, 29.52) * mm, "end": v(49.09, 29.52) * mm});
            skLineSegment(sketch, "E744", {"start": v(49.09, 29.52) * mm, "end": v(49.08, 29.52) * mm});
            skLineSegment(sketch, "E745", {"start": v(49.08, 29.52) * mm, "end": v(48.84, 29.52) * mm});
            skLineSegment(sketch, "E746", {"start": v(48.84, 29.52) * mm, "end": v(48.36, 29.62) * mm});
            skLineSegment(sketch, "E747", {"start": v(48.36, 29.62) * mm, "end": v(47.9, 29.8) * mm});
            skLineSegment(sketch, "E748", {"start": v(47.9, 29.8) * mm, "end": v(47.5, 30.08) * mm});
            skLineSegment(sketch, "E749", {"start": v(47.5, 30.08) * mm, "end": v(47.15, 30.43) * mm});
            skLineSegment(sketch, "E750", {"start": v(47.15, 30.43) * mm, "end": v(46.87, 30.84) * mm});
            skLineSegment(sketch, "E751", {"start": v(46.87, 30.84) * mm, "end": v(46.87, 30.84) * mm});
            skLineSegment(sketch, "E752", {"start": v(46.87, 30.84) * mm, "end": v(46.68, 31.3) * mm});
            skLineSegment(sketch, "E753", {"start": v(46.68, 31.3) * mm, "end": v(46.59, 31.78) * mm});
            skLineSegment(sketch, "E754", {"start": v(46.59, 31.78) * mm, "end": v(46.59, 31.94) * mm});
            skLineSegment(sketch, "E755", {"start": v(46.59, 31.94) * mm, "end": v(46.58, 31.98) * mm});
            skLineSegment(sketch, "E756", {"start": v(46.58, 31.98) * mm, "end": v(46.59, 32.06) * mm});
            skLineSegment(sketch, "E757", {"start": v(46.59, 32.06) * mm, "end": v(46.59, 32.27) * mm});
            skLineSegment(sketch, "E758", {"start": v(46.59, 32.27) * mm, "end": v(46.6, 32.38) * mm});
            skLineSegment(sketch, "E759", {"start": v(46.6, 32.38) * mm, "end": v(46.61, 32.47) * mm});
            skLineSegment(sketch, "E760", {"start": v(46.61, 32.47) * mm, "end": v(46.67, 32.66) * mm});
            skLineSegment(sketch, "E761", {"start": v(46.67, 32.66) * mm, "end": v(46.69, 32.76) * mm});
            skLineSegment(sketch, "E762", {"start": v(46.69, 32.76) * mm, "end": v(46.7, 32.8) * mm});
            skLineSegment(sketch, "E763", {"start": v(46.7, 32.8) * mm, "end": v(46.74, 32.95) * mm});
            skLineSegment(sketch, "E764", {"start": v(46.74, 32.95) * mm, "end": v(46.96, 33.4) * mm});
            skLineSegment(sketch, "E765", {"start": v(46.96, 33.4) * mm, "end": v(47.26, 33.78) * mm});
            skLineSegment(sketch, "E766", {"start": v(47.26, 33.78) * mm, "end": v(47.46, 33.96) * mm});
            skLineSegment(sketch, "E767", {"start": v(47.46, 33.96) * mm, "end": v(47.47, 33.97) * mm});
            skLineSegment(sketch, "E768", {"start": v(47.47, 33.97) * mm, "end": v(47.5, 34) * mm});
            skLineSegment(sketch, "E769", {"start": v(47.5, 34) * mm, "end": v(47.63, 34.1) * mm});
            skLineSegment(sketch, "E770", {"start": v(47.63, 34.1) * mm, "end": v(47.7, 34.15) * mm});
            skLineSegment(sketch, "E771", {"start": v(47.7, 34.15) * mm, "end": v(47.8, 34.23) * mm});
            skLineSegment(sketch, "E772", {"start": v(47.8, 34.23) * mm, "end": v(47.86, 34.27) * mm});
            skLineSegment(sketch, "E773", {"start": v(47.86, 34.27) * mm, "end": v(48.1, 34.39) * mm});
            skLineSegment(sketch, "E774", {"start": v(48.1, 34.39) * mm, "end": v(48.2, 34.46) * mm});
            skLineSegment(sketch, "E775", {"start": v(48.2, 34.46) * mm, "end": v(48.3, 34.5) * mm});
            skLineSegment(sketch, "E776", {"start": v(48.3, 34.5) * mm, "end": v(48.35, 34.55) * mm});
            skLineSegment(sketch, "E777", {"start": v(48.35, 34.55) * mm, "end": v(48.57, 34.81) * mm});
            skLineSegment(sketch, "E778", {"start": v(48.57, 34.81) * mm, "end": v(48.6, 34.84) * mm});
            skLineSegment(sketch, "E779", {"start": v(48.6, 34.84) * mm, "end": v(48.82, 35.25) * mm});
            skLineSegment(sketch, "E780", {"start": v(48.82, 35.25) * mm, "end": v(48.84, 35.29) * mm});
            skLineSegment(sketch, "E781", {"start": v(48.84, 35.29) * mm, "end": v(48.93, 35.57) * mm});
            skLineSegment(sketch, "E782", {"start": v(48.93, 35.57) * mm, "end": v(48.97, 35.72) * mm});
            skLineSegment(sketch, "E783", {"start": v(48.97, 35.72) * mm, "end": v(49, 35.83) * mm});
            skLineSegment(sketch, "E784", {"start": v(49, 35.83) * mm, "end": v(49, 35.86) * mm});
            skLineSegment(sketch, "E785", {"start": v(49, 35.86) * mm, "end": v(49, 35.9) * mm});
            skLineSegment(sketch, "E786", {"start": v(49, 35.9) * mm, "end": v(49.02, 36.34) * mm});
            skLineSegment(sketch, "E787", {"start": v(49.02, 36.34) * mm, "end": v(48.95, 36.83) * mm});
            skLineSegment(sketch, "E788", {"start": v(48.95, 36.83) * mm, "end": v(48.79, 37.3) * mm});
            skLineSegment(sketch, "E789", {"start": v(48.79, 37.3) * mm, "end": v(48.53, 37.72) * mm});
            skLineSegment(sketch, "E790", {"start": v(48.53, 37.72) * mm, "end": v(48.53, 37.72) * mm});
            skLineSegment(sketch, "E791", {"start": v(48.53, 37.72) * mm, "end": v(48.2, 38.09) * mm});
            skLineSegment(sketch, "E792", {"start": v(48.2, 38.09) * mm, "end": v(47.8, 38.38) * mm});
            skLineSegment(sketch, "E793", {"start": v(47.8, 38.38) * mm, "end": v(47.36, 38.6) * mm});
            skLineSegment(sketch, "E794", {"start": v(47.36, 38.6) * mm, "end": v(46.88, 38.71) * mm});
            skLineSegment(sketch, "E795", {"start": v(46.88, 38.71) * mm, "end": v(46.4, 38.74) * mm});
            skLineSegment(sketch, "E796", {"start": v(46.4, 38.74) * mm, "end": v(46.39, 38.74) * mm});
            skLineSegment(sketch, "E797", {"start": v(46.39, 38.74) * mm, "end": v(46.24, 38.72) * mm});
            skLineSegment(sketch, "E798", {"start": v(46.24, 38.72) * mm, "end": v(46.12, 38.7) * mm});
            skLineSegment(sketch, "E799", {"start": v(46.12, 38.7) * mm, "end": v(45.82, 38.63) * mm});
            skLineSegment(sketch, "E800", {"start": v(45.82, 38.63) * mm, "end": v(45.45, 38.48) * mm});
            skLineSegment(sketch, "E801", {"start": v(45.45, 38.48) * mm, "end": v(45.44, 38.46) * mm});
            skLineSegment(sketch, "E802", {"start": v(45.44, 38.46) * mm, "end": v(45.34, 38.38) * mm});
            skLineSegment(sketch, "E803", {"start": v(45.34, 38.38) * mm, "end": v(45.14, 38.17) * mm});
            skLineSegment(sketch, "E804", {"start": v(45.14, 38.17) * mm, "end": v(44.97, 38.05) * mm});
            skLineSegment(sketch, "E805", {"start": v(44.97, 38.05) * mm, "end": v(44.89, 37.97) * mm});
            skLineSegment(sketch, "E806", {"start": v(44.89, 37.97) * mm, "end": v(44.47, 37.72) * mm});
            skLineSegment(sketch, "E807", {"start": v(44.47, 37.72) * mm, "end": v(44.27, 37.64) * mm});
            skLineSegment(sketch, "E808", {"start": v(44.27, 37.64) * mm, "end": v(44.26, 37.64) * mm});
            skLineSegment(sketch, "E809", {"start": v(44.26, 37.64) * mm, "end": v(44.25, 37.64) * mm});
            skLineSegment(sketch, "E810", {"start": v(44.25, 37.64) * mm, "end": v(44, 37.54) * mm});
            skLineSegment(sketch, "E811", {"start": v(44, 37.54) * mm, "end": v(43.88, 37.52) * mm});
            skLineSegment(sketch, "E812", {"start": v(43.88, 37.52) * mm, "end": v(43.8, 37.5) * mm});
            skLineSegment(sketch, "E813", {"start": v(43.8, 37.5) * mm, "end": v(43.76, 37.5) * mm});
            skLineSegment(sketch, "E814", {"start": v(43.76, 37.5) * mm, "end": v(43.6, 37.48) * mm});
            skLineSegment(sketch, "E815", {"start": v(43.6, 37.48) * mm, "end": v(43.52, 37.47) * mm});
            skLineSegment(sketch, "E816", {"start": v(43.52, 37.47) * mm, "end": v(43.48, 37.47) * mm});
            skLineSegment(sketch, "E817", {"start": v(43.48, 37.47) * mm, "end": v(43.3, 37.45) * mm});
            skLineSegment(sketch, "E818", {"start": v(43.3, 37.45) * mm, "end": v(42.8, 37.5) * mm});
            skLineSegment(sketch, "E819", {"start": v(42.8, 37.5) * mm, "end": v(42.34, 37.65) * mm});
            skLineSegment(sketch, "E820", {"start": v(42.34, 37.65) * mm, "end": v(41.9, 37.88) * mm});
            skLineSegment(sketch, "E821", {"start": v(41.9, 37.88) * mm, "end": v(41.52, 38.2) * mm});
            skLineSegment(sketch, "E822", {"start": v(41.52, 38.2) * mm, "end": v(41.52, 38.2) * mm});
            skLineSegment(sketch, "E823", {"start": v(41.52, 38.2) * mm, "end": v(41.2, 38.58) * mm});
            skLineSegment(sketch, "E824", {"start": v(41.2, 38.58) * mm, "end": v(40.98, 39.01) * mm});
            skLineSegment(sketch, "E825", {"start": v(40.98, 39.01) * mm, "end": v(40.84, 39.49) * mm});
            skLineSegment(sketch, "E826", {"start": v(40.84, 39.49) * mm, "end": v(40.79, 39.98) * mm});
            skLineSegment(sketch, "E827", {"start": v(40.79, 39.98) * mm, "end": v(40.84, 40.47) * mm});
            skLineSegment(sketch, "E828", {"start": v(40.84, 40.47) * mm, "end": v(40.88, 40.6) * mm});
            skLineSegment(sketch, "E829", {"start": v(40.88, 40.6) * mm, "end": v(40.9, 40.69) * mm});
            skLineSegment(sketch, "E830", {"start": v(40.9, 40.69) * mm, "end": v(40.96, 40.87) * mm});
            skLineSegment(sketch, "E831", {"start": v(40.96, 40.87) * mm, "end": v(40.98, 40.94) * mm});
            skLineSegment(sketch, "E832", {"start": v(40.98, 40.94) * mm, "end": v(41, 40.97) * mm});
            skLineSegment(sketch, "E833", {"start": v(41, 40.97) * mm, "end": v(41.07, 41.15) * mm});
            skLineSegment(sketch, "E834", {"start": v(41.07, 41.15) * mm, "end": v(41.33, 41.57) * mm});
            skLineSegment(sketch, "E835", {"start": v(41.33, 41.57) * mm, "end": v(41.42, 41.66) * mm});
            skLineSegment(sketch, "E836", {"start": v(41.42, 41.66) * mm, "end": v(41.53, 41.82) * mm});
            skLineSegment(sketch, "E837", {"start": v(41.53, 41.82) * mm, "end": v(41.75, 42.03) * mm});
            skLineSegment(sketch, "E838", {"start": v(41.75, 42.03) * mm, "end": v(41.82, 42.11) * mm});
            skLineSegment(sketch, "E839", {"start": v(41.82, 42.11) * mm, "end": v(41.82, 42.11) * mm});
            skLineSegment(sketch, "E840", {"start": v(41.82, 42.11) * mm, "end": v(41.98, 42.48) * mm});
            skLineSegment(sketch, "E841", {"start": v(41.98, 42.48) * mm, "end": v(42.04, 42.76) * mm});
            skLineSegment(sketch, "E842", {"start": v(42.04, 42.76) * mm, "end": v(42.08, 43) * mm});
            skLineSegment(sketch, "E843", {"start": v(42.08, 43) * mm, "end": v(42.09, 43.04) * mm});
            skLineSegment(sketch, "E844", {"start": v(42.09, 43.04) * mm, "end": v(42.07, 43.54) * mm});
            skLineSegment(sketch, "E845", {"start": v(42.07, 43.54) * mm, "end": v(41.95, 44.02) * mm});
            skLineSegment(sketch, "E846", {"start": v(41.95, 44.02) * mm, "end": v(41.74, 44.46) * mm});
            skLineSegment(sketch, "E847", {"start": v(41.74, 44.46) * mm, "end": v(41.45, 44.86) * mm});
            skLineSegment(sketch, "E848", {"start": v(41.45, 44.86) * mm, "end": v(41.09, 45.2) * mm});
            skLineSegment(sketch, "E849", {"start": v(41.09, 45.2) * mm, "end": v(41.09, 45.2) * mm});
            skLineSegment(sketch, "E850", {"start": v(41.09, 45.2) * mm, "end": v(40.67, 45.45) * mm});
            skLineSegment(sketch, "E851", {"start": v(40.67, 45.45) * mm, "end": v(40.2, 45.62) * mm});
            skLineSegment(sketch, "E852", {"start": v(40.2, 45.62) * mm, "end": v(39.72, 45.7) * mm});
            skLineSegment(sketch, "E853", {"start": v(39.72, 45.7) * mm, "end": v(39.29, 45.68) * mm});
            skLineSegment(sketch, "E854", {"start": v(39.29, 45.68) * mm, "end": v(39.24, 45.68) * mm});
            skLineSegment(sketch, "E855", {"start": v(39.24, 45.68) * mm, "end": v(39.2, 45.67) * mm});
            skLineSegment(sketch, "E856", {"start": v(39.2, 45.67) * mm, "end": v(39.04, 45.63) * mm});
            skLineSegment(sketch, "E857", {"start": v(39.04, 45.63) * mm, "end": v(38.96, 45.61) * mm});
            skLineSegment(sketch, "E858", {"start": v(38.96, 45.61) * mm, "end": v(38.64, 45.51) * mm});
            skLineSegment(sketch, "E859", {"start": v(38.64, 45.51) * mm, "end": v(38.21, 45.28) * mm});
            skLineSegment(sketch, "E860", {"start": v(38.21, 45.28) * mm, "end": v(37.93, 45.05) * mm});
            skLineSegment(sketch, "E861", {"start": v(37.93, 45.05) * mm, "end": v(37.92, 45.04) * mm});
            skLineSegment(sketch, "E862", {"start": v(37.92, 45.04) * mm, "end": v(37.9, 45) * mm});
            skLineSegment(sketch, "E863", {"start": v(37.9, 45) * mm, "end": v(37.83, 44.88) * mm});
            skLineSegment(sketch, "E864", {"start": v(37.83, 44.88) * mm, "end": v(37.7, 44.62) * mm});
            skLineSegment(sketch, "E865", {"start": v(37.7, 44.62) * mm, "end": v(37.61, 44.51) * mm});
            skLineSegment(sketch, "E866", {"start": v(37.61, 44.51) * mm, "end": v(37.55, 44.44) * mm});
            skLineSegment(sketch, "E867", {"start": v(37.55, 44.44) * mm, "end": v(37.5, 44.35) * mm});
            skLineSegment(sketch, "E868", {"start": v(37.5, 44.35) * mm, "end": v(37.17, 43.98) * mm});
            skLineSegment(sketch, "E869", {"start": v(37.17, 43.98) * mm, "end": v(36.78, 43.69) * mm});
            skLineSegment(sketch, "E870", {"start": v(36.78, 43.69) * mm, "end": v(36.74, 43.67) * mm});
            skLineSegment(sketch, "E871", {"start": v(36.74, 43.67) * mm, "end": v(36.62, 43.61) * mm});
            skLineSegment(sketch, "E872", {"start": v(36.62, 43.61) * mm, "end": v(36.58, 43.58) * mm});
            skLineSegment(sketch, "E873", {"start": v(36.58, 43.58) * mm, "end": v(36.48, 43.55) * mm});
            skLineSegment(sketch, "E874", {"start": v(36.48, 43.55) * mm, "end": v(36.33, 43.47) * mm});
            skLineSegment(sketch, "E875", {"start": v(36.33, 43.47) * mm, "end": v(36.25, 43.45) * mm});
            skLineSegment(sketch, "E876", {"start": v(36.25, 43.45) * mm, "end": v(36.12, 43.4) * mm});
            skLineSegment(sketch, "E877", {"start": v(36.12, 43.4) * mm, "end": v(35.85, 43.35) * mm});
            skLineSegment(sketch, "E878", {"start": v(35.85, 43.35) * mm, "end": v(35.85, 43.35) * mm});
            skLineSegment(sketch, "E879", {"start": v(35.85, 43.35) * mm, "end": v(35.64, 43.3) * mm});
            skLineSegment(sketch, "E880", {"start": v(35.64, 43.3) * mm, "end": v(35.14, 43.32) * mm});
            skLineSegment(sketch, "E881", {"start": v(35.14, 43.32) * mm, "end": v(34.66, 43.42) * mm});
            skLineSegment(sketch, "E882", {"start": v(34.66, 43.42) * mm, "end": v(34.2, 43.61) * mm});
            skLineSegment(sketch, "E883", {"start": v(34.2, 43.61) * mm, "end": v(34.2, 43.61) * mm});
            skLineSegment(sketch, "E884", {"start": v(34.2, 43.61) * mm, "end": v(33.8, 43.89) * mm});
            skLineSegment(sketch, "E885", {"start": v(33.8, 43.89) * mm, "end": v(33.45, 44.24) * mm});
            skLineSegment(sketch, "E886", {"start": v(33.45, 44.24) * mm, "end": v(33.18, 44.66) * mm});
            skLineSegment(sketch, "E887", {"start": v(33.18, 44.66) * mm, "end": v(33, 45.11) * mm});
            skLineSegment(sketch, "E888", {"start": v(33, 45.11) * mm, "end": v(32.9, 45.6) * mm});
            skLineSegment(sketch, "E889", {"start": v(32.9, 45.6) * mm, "end": v(32.9, 45.78) * mm});
            skLineSegment(sketch, "E890", {"start": v(32.9, 45.78) * mm, "end": v(32.9, 45.84) * mm});
            skLineSegment(sketch, "E891", {"start": v(32.9, 45.84) * mm, "end": v(32.91, 45.96) * mm});
            skLineSegment(sketch, "E892", {"start": v(32.91, 45.96) * mm, "end": v(32.91, 46.1) * mm});
            skLineSegment(sketch, "E893", {"start": v(32.91, 46.1) * mm, "end": v(32.93, 46.16) * mm});
            skLineSegment(sketch, "E894", {"start": v(32.93, 46.16) * mm, "end": v(32.94, 46.33) * mm});
            skLineSegment(sketch, "E895", {"start": v(32.94, 46.33) * mm, "end": v(33.07, 46.8) * mm});
            skLineSegment(sketch, "E896", {"start": v(33.07, 46.8) * mm, "end": v(33.14, 46.94) * mm});
            skLineSegment(sketch, "E897", {"start": v(33.14, 46.94) * mm, "end": v(33.2, 47.13) * mm});
            skLineSegment(sketch, "E898", {"start": v(33.2, 47.13) * mm, "end": v(33.37, 47.41) * mm});
            skLineSegment(sketch, "E899", {"start": v(33.37, 47.41) * mm, "end": v(33.38, 47.44) * mm});
            skLineSegment(sketch, "E900", {"start": v(33.38, 47.44) * mm, "end": v(33.44, 47.84) * mm});
            skLineSegment(sketch, "E901", {"start": v(33.44, 47.84) * mm, "end": v(33.41, 48.2) * mm});
            skLineSegment(sketch, "E902", {"start": v(33.41, 48.2) * mm, "end": v(33.4, 48.29) * mm});
            skLineSegment(sketch, "E903", {"start": v(33.4, 48.29) * mm, "end": v(33.39, 48.39) * mm});
            skLineSegment(sketch, "E904", {"start": v(33.39, 48.39) * mm, "end": v(33.36, 48.48) * mm});
            skLineSegment(sketch, "E905", {"start": v(33.36, 48.48) * mm, "end": v(33.27, 48.74) * mm});
            skLineSegment(sketch, "E906", {"start": v(33.27, 48.74) * mm, "end": v(33.22, 48.89) * mm});
            skLineSegment(sketch, "E907", {"start": v(33.22, 48.89) * mm, "end": v(32.98, 49.32) * mm});
            skLineSegment(sketch, "E908", {"start": v(32.98, 49.32) * mm, "end": v(32.65, 49.69) * mm});
            skLineSegment(sketch, "E909", {"start": v(32.65, 49.69) * mm, "end": v(32.26, 49.99) * mm});
            skLineSegment(sketch, "E910", {"start": v(32.26, 49.99) * mm, "end": v(31.81, 50.2) * mm});
            skLineSegment(sketch, "E911", {"start": v(31.81, 50.2) * mm, "end": v(31.81, 50.2) * mm});
            skLineSegment(sketch, "E912", {"start": v(31.81, 50.2) * mm, "end": v(31.34, 50.33) * mm});
            skLineSegment(sketch, "E913", {"start": v(31.34, 50.33) * mm, "end": v(30.84, 50.36) * mm});
            skLineSegment(sketch, "E914", {"start": v(30.84, 50.36) * mm, "end": v(30.36, 50.3) * mm});
            skLineSegment(sketch, "E915", {"start": v(30.36, 50.3) * mm, "end": v(29.89, 50.14) * mm});
            skLineSegment(sketch, "E916", {"start": v(29.89, 50.14) * mm, "end": v(29.56, 49.95) * mm});
            skLineSegment(sketch, "E917", {"start": v(29.56, 49.95) * mm, "end": v(29.42, 49.85) * mm});
            skLineSegment(sketch, "E918", {"start": v(29.42, 49.85) * mm, "end": v(29.33, 49.77) * mm});
            skLineSegment(sketch, "E919", {"start": v(29.33, 49.77) * mm, "end": v(29.32, 49.77) * mm});
            skLineSegment(sketch, "E920", {"start": v(29.32, 49.77) * mm, "end": v(29.03, 49.48) * mm});
            skLineSegment(sketch, "E921", {"start": v(29.03, 49.48) * mm, "end": v(29.01, 49.44) * mm});
            skLineSegment(sketch, "E922", {"start": v(29.01, 49.44) * mm, "end": v(28.85, 49.2) * mm});
            skLineSegment(sketch, "E923", {"start": v(28.85, 49.2) * mm, "end": v(28.84, 49.13) * mm});
            skLineSegment(sketch, "E924", {"start": v(28.84, 49.13) * mm, "end": v(28.81, 49.05) * mm});
            skLineSegment(sketch, "E925", {"start": v(28.81, 49.05) * mm, "end": v(28.8, 49) * mm});
            skLineSegment(sketch, "E926", {"start": v(28.8, 49) * mm, "end": v(28.75, 48.77) * mm});
            skLineSegment(sketch, "E927", {"start": v(28.75, 48.77) * mm, "end": v(28.69, 48.61) * mm});
            skLineSegment(sketch, "E928", {"start": v(28.69, 48.61) * mm, "end": v(28.66, 48.5) * mm});
            skLineSegment(sketch, "E929", {"start": v(28.66, 48.5) * mm, "end": v(28.45, 48.05) * mm});
            skLineSegment(sketch, "E930", {"start": v(28.45, 48.05) * mm, "end": v(28.35, 47.91) * mm});
            skLineSegment(sketch, "E931", {"start": v(28.35, 47.91) * mm, "end": v(28.3, 47.83) * mm});
            skLineSegment(sketch, "E932", {"start": v(28.3, 47.83) * mm, "end": v(28.18, 47.69) * mm});
            skLineSegment(sketch, "E933", {"start": v(28.18, 47.69) * mm, "end": v(28.16, 47.66) * mm});
            skLineSegment(sketch, "E934", {"start": v(28.16, 47.66) * mm, "end": v(28.14, 47.64) * mm});
            skLineSegment(sketch, "E935", {"start": v(28.14, 47.64) * mm, "end": v(27.98, 47.45) * mm});
            skLineSegment(sketch, "E936", {"start": v(27.98, 47.45) * mm, "end": v(27.6, 47.15) * mm});
            skLineSegment(sketch, "E937", {"start": v(27.6, 47.15) * mm, "end": v(27.15, 46.92) * mm});
            skLineSegment(sketch, "E938", {"start": v(27.15, 46.92) * mm, "end": v(26.68, 46.79) * mm});
            skLineSegment(sketch, "E939", {"start": v(26.68, 46.79) * mm, "end": v(26.18, 46.75) * mm});
            skLineSegment(sketch, "E940", {"start": v(26.18, 46.75) * mm, "end": v(25.7, 46.8) * mm});
            skLineSegment(sketch, "E941", {"start": v(25.7, 46.8) * mm, "end": v(25.7, 46.8) * mm});
            skLineSegment(sketch, "E942", {"start": v(25.7, 46.8) * mm, "end": v(25.22, 46.96) * mm});
            skLineSegment(sketch, "E943", {"start": v(25.22, 46.96) * mm, "end": v(24.8, 47.2) * mm});
            skLineSegment(sketch, "E944", {"start": v(24.8, 47.2) * mm, "end": v(24.42, 47.52) * mm});
            skLineSegment(sketch, "E945", {"start": v(24.42, 47.52) * mm, "end": v(24.3, 47.66) * mm});
            skLineSegment(sketch, "E946", {"start": v(24.3, 47.66) * mm, "end": v(24.28, 47.69) * mm});
            skLineSegment(sketch, "E947", {"start": v(24.28, 47.69) * mm, "end": v(24.27, 47.7) * mm});
            skLineSegment(sketch, "E948", {"start": v(24.27, 47.7) * mm, "end": v(24.23, 47.76) * mm});
            skLineSegment(sketch, "E949", {"start": v(24.23, 47.76) * mm, "end": v(24.13, 47.88) * mm});
            skLineSegment(sketch, "E950", {"start": v(24.13, 47.88) * mm, "end": v(24.11, 47.9) * mm});
            skLineSegment(sketch, "E951", {"start": v(24.11, 47.9) * mm, "end": v(24.07, 48) * mm});
            skLineSegment(sketch, "E952", {"start": v(24.07, 48) * mm, "end": v(24, 48.1) * mm});
            skLineSegment(sketch, "E953", {"start": v(24, 48.1) * mm, "end": v(23.9, 48.32) * mm});
            skLineSegment(sketch, "E954", {"start": v(23.9, 48.32) * mm, "end": v(23.89, 48.34) * mm});
            skLineSegment(sketch, "E955", {"start": v(23.89, 48.34) * mm, "end": v(23.88, 48.36) * mm});
            skLineSegment(sketch, "E956", {"start": v(23.88, 48.36) * mm, "end": v(23.82, 48.51) * mm});
            skLineSegment(sketch, "E957", {"start": v(23.82, 48.51) * mm, "end": v(23.8, 48.55) * mm});
            skLineSegment(sketch, "E958", {"start": v(23.8, 48.55) * mm, "end": v(23.7, 49.04) * mm});
            skLineSegment(sketch, "E959", {"start": v(23.7, 49.04) * mm, "end": v(23.7, 49.53) * mm});
            skLineSegment(sketch, "E960", {"start": v(23.7, 49.53) * mm, "end": v(23.71, 49.62) * mm});
            skLineSegment(sketch, "E961", {"start": v(23.71, 49.62) * mm, "end": v(23.72, 49.7) * mm});
            skLineSegment(sketch, "E962", {"start": v(23.72, 49.7) * mm, "end": v(23.73, 49.87) * mm});
            skLineSegment(sketch, "E963", {"start": v(23.73, 49.87) * mm, "end": v(23.8, 50.16) * mm});
            skLineSegment(sketch, "E964", {"start": v(23.8, 50.16) * mm, "end": v(23.82, 50.3) * mm});
            skLineSegment(sketch, "E965", {"start": v(23.82, 50.3) * mm, "end": v(23.84, 50.36) * mm});
            skLineSegment(sketch, "E966", {"start": v(23.84, 50.36) * mm, "end": v(23.83, 50.46) * mm});
            skLineSegment(sketch, "E967", {"start": v(23.83, 50.46) * mm, "end": v(23.8, 50.62) * mm});
            skLineSegment(sketch, "E968", {"start": v(23.8, 50.62) * mm, "end": v(23.8, 50.7) * mm});
            skLineSegment(sketch, "E969", {"start": v(23.8, 50.7) * mm, "end": v(23.63, 51.17) * mm});
            skLineSegment(sketch, "E970", {"start": v(23.63, 51.17) * mm, "end": v(23.46, 51.47) * mm});
            skLineSegment(sketch, "E971", {"start": v(23.46, 51.47) * mm, "end": v(23.42, 51.53) * mm});
            skLineSegment(sketch, "E972", {"start": v(23.42, 51.53) * mm, "end": v(23.35, 51.64) * mm});
            skLineSegment(sketch, "E973", {"start": v(23.35, 51.64) * mm, "end": v(23.3, 51.7) * mm});
            skLineSegment(sketch, "E974", {"start": v(23.3, 51.7) * mm, "end": v(23.27, 51.72) * mm});
            skLineSegment(sketch, "E975", {"start": v(23.27, 51.72) * mm, "end": v(22.98, 52.01) * mm});
            skLineSegment(sketch, "E976", {"start": v(22.98, 52.01) * mm, "end": v(22.57, 52.3) * mm});
            skLineSegment(sketch, "E977", {"start": v(22.57, 52.3) * mm, "end": v(22.12, 52.48) * mm});
            skLineSegment(sketch, "E978", {"start": v(22.12, 52.48) * mm, "end": v(21.63, 52.58) * mm});
            skLineSegment(sketch, "E979", {"start": v(21.63, 52.58) * mm, "end": v(21.63, 52.58) * mm});
            skLineSegment(sketch, "E980", {"start": v(21.63, 52.58) * mm, "end": v(21.14, 52.58) * mm});
            skLineSegment(sketch, "E981", {"start": v(21.14, 52.58) * mm, "end": v(20.65, 52.49) * mm});
            skLineSegment(sketch, "E982", {"start": v(20.65, 52.49) * mm, "end": v(20.2, 52.3) * mm});
            skLineSegment(sketch, "E983", {"start": v(20.2, 52.3) * mm, "end": v(20.02, 52.18) * mm});
            skLineSegment(sketch, "E984", {"start": v(20.02, 52.18) * mm, "end": v(19.8, 52.03) * mm});
            skLineSegment(sketch, "E985", {"start": v(19.8, 52.03) * mm, "end": v(19.78, 52.02) * mm});
            skLineSegment(sketch, "E986", {"start": v(19.78, 52.02) * mm, "end": v(19.58, 51.82) * mm});
            skLineSegment(sketch, "E987", {"start": v(19.58, 51.82) * mm, "end": v(19.4, 51.62) * mm});
            skLineSegment(sketch, "E988", {"start": v(19.4, 51.62) * mm, "end": v(19.38, 51.6) * mm});
            skLineSegment(sketch, "E989", {"start": v(19.38, 51.6) * mm, "end": v(19.14, 51.19) * mm});
            skLineSegment(sketch, "E990", {"start": v(19.14, 51.19) * mm, "end": v(19.05, 50.94) * mm});
            skLineSegment(sketch, "E991", {"start": v(19.05, 50.94) * mm, "end": v(19.05, 50.93) * mm});
            skLineSegment(sketch, "E992", {"start": v(19.05, 50.93) * mm, "end": v(19.05, 50.92) * mm});
            skLineSegment(sketch, "E993", {"start": v(19.05, 50.92) * mm, "end": v(19.04, 50.75) * mm});
            skLineSegment(sketch, "E994", {"start": v(19.04, 50.75) * mm, "end": v(19.05, 50.5) * mm});
            skLineSegment(sketch, "E995", {"start": v(19.05, 50.5) * mm, "end": v(19.03, 50.34) * mm});
            skLineSegment(sketch, "E996", {"start": v(19.03, 50.34) * mm, "end": v(19.02, 50.3) * mm});
            skLineSegment(sketch, "E997", {"start": v(19.02, 50.3) * mm, "end": v(19.03, 50.18) * mm});
            skLineSegment(sketch, "E998", {"start": v(19.03, 50.18) * mm, "end": v(18.93, 49.7) * mm});
            skLineSegment(sketch, "E999", {"start": v(18.93, 49.7) * mm, "end": v(18.9, 49.6) * mm});
            skLineSegment(sketch, "E1000", {"start": v(18.9, 49.6) * mm, "end": v(18.86, 49.46) * mm});
            skLineSegment(sketch, "E1001", {"start": v(18.86, 49.46) * mm, "end": v(18.65, 49.01) * mm});
            skLineSegment(sketch, "E1002", {"start": v(18.65, 49.01) * mm, "end": v(18.35, 48.62) * mm});
            skLineSegment(sketch, "E1003", {"start": v(18.35, 48.62) * mm, "end": v(17.99, 48.29) * mm});
            skLineSegment(sketch, "E1004", {"start": v(17.99, 48.29) * mm, "end": v(17.85, 48.2) * mm});
            skLineSegment(sketch, "E1005", {"start": v(17.85, 48.2) * mm, "end": v(17.84, 48.2) * mm});
            skLineSegment(sketch, "E1006", {"start": v(17.84, 48.2) * mm, "end": v(17.82, 48.19) * mm});
            skLineSegment(sketch, "E1007", {"start": v(17.82, 48.19) * mm, "end": v(17.56, 48.03) * mm});
            skLineSegment(sketch, "E1008", {"start": v(17.56, 48.03) * mm, "end": v(17.46, 48) * mm});
            skLineSegment(sketch, "E1009", {"start": v(17.46, 48) * mm, "end": v(17.4, 47.97) * mm});
            skLineSegment(sketch, "E1010", {"start": v(17.4, 47.97) * mm, "end": v(17.26, 47.92) * mm});
            skLineSegment(sketch, "E1011", {"start": v(17.26, 47.92) * mm, "end": v(17.1, 47.87) * mm});
            skLineSegment(sketch, "E1012", {"start": v(17.1, 47.87) * mm, "end": v(17.03, 47.86) * mm});
            skLineSegment(sketch, "E1013", {"start": v(17.03, 47.86) * mm, "end": v(16.93, 47.83) * mm});
            skLineSegment(sketch, "E1014", {"start": v(16.93, 47.83) * mm, "end": v(16.65, 47.8) * mm});
            skLineSegment(sketch, "E1015", {"start": v(16.65, 47.8) * mm, "end": v(16.61, 47.8) * mm});
            skLineSegment(sketch, "E1016", {"start": v(16.61, 47.8) * mm, "end": v(16.61, 47.8) * mm});
            skLineSegment(sketch, "E1017", {"start": v(16.61, 47.8) * mm, "end": v(16.6, 47.8) * mm});
            skLineSegment(sketch, "E1018", {"start": v(16.6, 47.8) * mm, "end": v(16.44, 47.78) * mm});
            skLineSegment(sketch, "E1019", {"start": v(16.44, 47.78) * mm, "end": v(16.44, 47.78) * mm});
            skLineSegment(sketch, "E1020", {"start": v(16.44, 47.78) * mm, "end": v(15.95, 47.83) * mm});
            skLineSegment(sketch, "E1021", {"start": v(15.95, 47.83) * mm, "end": v(15.47, 47.98) * mm});
            skLineSegment(sketch, "E1022", {"start": v(15.47, 47.98) * mm, "end": v(15.04, 48.21) * mm});
            skLineSegment(sketch, "E1023", {"start": v(15.04, 48.21) * mm, "end": v(14.66, 48.53) * mm});
            skLineSegment(sketch, "E1024", {"start": v(14.66, 48.53) * mm, "end": v(14.35, 48.91) * mm});
            skLineSegment(sketch, "E1025", {"start": v(14.35, 48.91) * mm, "end": v(14.26, 49.07) * mm});
            skLineSegment(sketch, "E1026", {"start": v(14.26, 49.07) * mm, "end": v(14.25, 49.1) * mm});
            skLineSegment(sketch, "E1027", {"start": v(14.25, 49.1) * mm, "end": v(14.2, 49.18) * mm});
            skLineSegment(sketch, "E1028", {"start": v(14.2, 49.18) * mm, "end": v(14.12, 49.35) * mm});
            skLineSegment(sketch, "E1029", {"start": v(14.12, 49.35) * mm, "end": v(14.1, 49.42) * mm});
            skLineSegment(sketch, "E1030", {"start": v(14.1, 49.42) * mm, "end": v(14.04, 49.55) * mm});
            skLineSegment(sketch, "E1031", {"start": v(14.04, 49.55) * mm, "end": v(13.92, 50.03) * mm});
            skLineSegment(sketch, "E1032", {"start": v(13.92, 50.03) * mm, "end": v(13.92, 50.13) * mm});
            skLineSegment(sketch, "E1033", {"start": v(13.92, 50.13) * mm, "end": v(13.89, 50.32) * mm});
            skLineSegment(sketch, "E1034", {"start": v(13.89, 50.32) * mm, "end": v(13.9, 50.54) * mm});
            skLineSegment(sketch, "E1035", {"start": v(13.9, 50.54) * mm, "end": v(13.87, 50.68) * mm});
            skLineSegment(sketch, "E1036", {"start": v(13.87, 50.68) * mm, "end": v(13.88, 50.87) * mm});
            skLineSegment(sketch, "E1037", {"start": v(13.88, 50.87) * mm, "end": v(13.84, 51) * mm});
            skLineSegment(sketch, "E1038", {"start": v(13.84, 51) * mm, "end": v(13.8, 51.13) * mm});
            skLineSegment(sketch, "E1039", {"start": v(13.8, 51.13) * mm, "end": v(13.53, 51.55) * mm});
            skLineSegment(sketch, "E1040", {"start": v(13.53, 51.55) * mm, "end": v(13.2, 51.91) * mm});
            skLineSegment(sketch, "E1041", {"start": v(13.2, 51.91) * mm, "end": v(12.8, 52.2) * mm});
            skLineSegment(sketch, "E1042", {"start": v(12.8, 52.2) * mm, "end": v(12.44, 52.36) * mm});
            skLineSegment(sketch, "E1043", {"start": v(12.44, 52.36) * mm, "end": v(12.3, 52.41) * mm});
            skLineSegment(sketch, "E1044", {"start": v(12.3, 52.41) * mm, "end": v(12.24, 52.43) * mm});
            skLineSegment(sketch, "E1045", {"start": v(12.24, 52.43) * mm, "end": v(12.1, 52.46) * mm});
            skLineSegment(sketch, "E1046", {"start": v(12.1, 52.46) * mm, "end": v(11.77, 52.52) * mm});
            skLineSegment(sketch, "E1047", {"start": v(11.77, 52.52) * mm, "end": v(11.74, 52.52) * mm});
            skLineSegment(sketch, "E1048", {"start": v(11.74, 52.52) * mm, "end": v(11.27, 52.5) * mm});
            skLineSegment(sketch, "E1049", {"start": v(11.27, 52.5) * mm, "end": v(11.26, 52.5) * mm});
            skLineSegment(sketch, "E1050", {"start": v(11.26, 52.5) * mm, "end": v(10.78, 52.4) * mm});
            skLineSegment(sketch, "E1051", {"start": v(10.78, 52.4) * mm, "end": v(10.33, 52.2) * mm});
            skLineSegment(sketch, "E1052", {"start": v(10.33, 52.2) * mm, "end": v(9.93, 51.91) * mm});
            skLineSegment(sketch, "E1053", {"start": v(9.93, 51.91) * mm, "end": v(9.59, 51.56) * mm});
            skLineSegment(sketch, "E1054", {"start": v(9.59, 51.56) * mm, "end": v(9.32, 51.14) * mm});
            skLineSegment(sketch, "E1055", {"start": v(9.32, 51.14) * mm, "end": v(9.26, 50.98) * mm});
            skLineSegment(sketch, "E1056", {"start": v(9.26, 50.98) * mm, "end": v(9.21, 50.85) * mm});
            skLineSegment(sketch, "E1057", {"start": v(9.21, 50.85) * mm, "end": v(9.14, 50.62) * mm});
            skLineSegment(sketch, "E1058", {"start": v(9.14, 50.62) * mm, "end": v(9.14, 50.6) * mm});
            skLineSegment(sketch, "E1059", {"start": v(9.14, 50.6) * mm, "end": v(9.16, 50.4) * mm});
            skLineSegment(sketch, "E1060", {"start": v(9.16, 50.4) * mm, "end": v(9.2, 50.23) * mm});
            skLineSegment(sketch, "E1061", {"start": v(9.2, 50.23) * mm, "end": v(9.21, 49.96) * mm});
            skLineSegment(sketch, "E1062", {"start": v(9.21, 49.96) * mm, "end": v(9.24, 49.82) * mm});
            skLineSegment(sketch, "E1063", {"start": v(9.24, 49.82) * mm, "end": v(9.24, 49.72) * mm});
            skLineSegment(sketch, "E1064", {"start": v(9.24, 49.72) * mm, "end": v(9.23, 49.56) * mm});
            skLineSegment(sketch, "E1065", {"start": v(9.23, 49.56) * mm, "end": v(9.24, 49.5) * mm});
            skLineSegment(sketch, "E1066", {"start": v(9.24, 49.5) * mm, "end": v(9.23, 49.38) * mm});
            skLineSegment(sketch, "E1067", {"start": v(9.23, 49.38) * mm, "end": v(9.23, 49.33) * mm});
            skLineSegment(sketch, "E1068", {"start": v(9.23, 49.33) * mm, "end": v(9.22, 49.3) * mm});
            skLineSegment(sketch, "E1069", {"start": v(9.22, 49.3) * mm, "end": v(9.2, 49.02) * mm});
            skLineSegment(sketch, "E1070", {"start": v(9.2, 49.02) * mm, "end": v(9.15, 48.83) * mm});
            skLineSegment(sketch, "E1071", {"start": v(9.15, 48.83) * mm, "end": v(9.14, 48.8) * mm});
            skLineSegment(sketch, "E1072", {"start": v(9.14, 48.8) * mm, "end": v(9.12, 48.75) * mm});
            skLineSegment(sketch, "E1073", {"start": v(9.12, 48.75) * mm, "end": v(9.07, 48.54) * mm});
            skLineSegment(sketch, "E1074", {"start": v(9.07, 48.54) * mm, "end": v(9.02, 48.46) * mm});
            skLineSegment(sketch, "E1075", {"start": v(9.02, 48.46) * mm, "end": v(8.98, 48.34) * mm});
            skLineSegment(sketch, "E1076", {"start": v(8.98, 48.34) * mm, "end": v(8.73, 47.91) * mm});
            skLineSegment(sketch, "E1077", {"start": v(8.73, 47.91) * mm, "end": v(8.4, 47.55) * mm});
            skLineSegment(sketch, "E1078", {"start": v(8.4, 47.55) * mm, "end": v(8, 47.25) * mm});
            skLineSegment(sketch, "E1079", {"start": v(8, 47.25) * mm, "end": v(7.57, 47.04) * mm});
            skLineSegment(sketch, "E1080", {"start": v(7.57, 47.04) * mm, "end": v(7.09, 46.91) * mm});
            skLineSegment(sketch, "E1081", {"start": v(7.09, 46.91) * mm, "end": v(7.09, 46.91) * mm});
            skLineSegment(sketch, "E1082", {"start": v(7.09, 46.91) * mm, "end": v(6.6, 46.88) * mm});
            skLineSegment(sketch, "E1083", {"start": v(6.6, 46.88) * mm, "end": v(6.1, 46.95) * mm});
            skLineSegment(sketch, "E1084", {"start": v(6.1, 46.95) * mm, "end": v(5.64, 47.11) * mm});
            skLineSegment(sketch, "E1085", {"start": v(5.64, 47.11) * mm, "end": v(5.52, 47.19) * mm});
            skLineSegment(sketch, "E1086", {"start": v(5.52, 47.19) * mm, "end": v(5.47, 47.2) * mm});
            skLineSegment(sketch, "E1087", {"start": v(5.47, 47.2) * mm, "end": v(5.36, 47.28) * mm});
            skLineSegment(sketch, "E1088", {"start": v(5.36, 47.28) * mm, "end": v(5.22, 47.36) * mm});
            skLineSegment(sketch, "E1089", {"start": v(5.22, 47.36) * mm, "end": v(5.16, 47.41) * mm});
            skLineSegment(sketch, "E1090", {"start": v(5.16, 47.41) * mm, "end": v(5.06, 47.48) * mm});
            skLineSegment(sketch, "E1091", {"start": v(5.06, 47.48) * mm, "end": v(4.86, 47.69) * mm});
            skLineSegment(sketch, "E1092", {"start": v(4.86, 47.69) * mm, "end": v(4.85, 47.7) * mm});
            skLineSegment(sketch, "E1093", {"start": v(4.85, 47.7) * mm, "end": v(4.85, 47.7) * mm});
            skLineSegment(sketch, "E1094", {"start": v(4.85, 47.7) * mm, "end": v(4.74, 47.8) * mm});
            skLineSegment(sketch, "E1095", {"start": v(4.74, 47.8) * mm, "end": v(4.71, 47.83) * mm});
            skLineSegment(sketch, "E1096", {"start": v(4.71, 47.83) * mm, "end": v(4.44, 48.24) * mm});
            skLineSegment(sketch, "E1097", {"start": v(4.44, 48.24) * mm, "end": v(4.36, 48.43) * mm});
            skLineSegment(sketch, "E1098", {"start": v(4.36, 48.43) * mm, "end": v(4.33, 48.5) * mm});
            skLineSegment(sketch, "E1099", {"start": v(4.33, 48.5) * mm, "end": v(4.27, 48.64) * mm});
            skLineSegment(sketch, "E1100", {"start": v(4.27, 48.64) * mm, "end": v(4.25, 48.7) * mm});
            skLineSegment(sketch, "E1101", {"start": v(4.25, 48.7) * mm, "end": v(4.25, 48.72) * mm});
            skLineSegment(sketch, "E1102", {"start": v(4.25, 48.72) * mm, "end": v(4.17, 48.96) * mm});
            skLineSegment(sketch, "E1103", {"start": v(4.17, 48.96) * mm, "end": v(4.15, 49.1) * mm});
            skLineSegment(sketch, "E1104", {"start": v(4.15, 49.1) * mm, "end": v(4.1, 49.23) * mm});
            skLineSegment(sketch, "E1105", {"start": v(4.1, 49.23) * mm, "end": v(4.09, 49.3) * mm});
            skLineSegment(sketch, "E1106", {"start": v(4.09, 49.3) * mm, "end": v(4.07, 49.53) * mm});
            skLineSegment(sketch, "E1107", {"start": v(4.07, 49.53) * mm, "end": v(4.02, 49.75) * mm});
            skLineSegment(sketch, "E1108", {"start": v(4.02, 49.75) * mm, "end": v(4.02, 49.97) * mm});
            skLineSegment(sketch, "E1109", {"start": v(4.02, 49.97) * mm, "end": v(3.83, 50.27) * mm});
            skLineSegment(sketch, "E1110", {"start": v(3.83, 50.27) * mm, "end": v(3.8, 50.32) * mm});
            skLineSegment(sketch, "E1111", {"start": v(3.8, 50.32) * mm, "end": v(3.63, 50.5) * mm});
            skLineSegment(sketch, "E1112", {"start": v(3.63, 50.5) * mm, "end": v(3.53, 50.6) * mm});
            skLineSegment(sketch, "E1113", {"start": v(3.53, 50.6) * mm, "end": v(3.4, 50.72) * mm});
            skLineSegment(sketch, "E1114", {"start": v(3.4, 50.72) * mm, "end": v(2.98, 50.99) * mm});
            skLineSegment(sketch, "E1115", {"start": v(2.98, 50.99) * mm, "end": v(2.52, 51.17) * mm});
            skLineSegment(sketch, "E1116", {"start": v(2.52, 51.17) * mm, "end": v(2.04, 51.25) * mm});
            skLineSegment(sketch, "E1117", {"start": v(2.04, 51.25) * mm, "end": v(1.54, 51.24) * mm});
            skLineSegment(sketch, "E1118", {"start": v(1.54, 51.24) * mm, "end": v(1.54, 51.24) * mm});
            skLineSegment(sketch, "E1119", {"start": v(1.54, 51.24) * mm, "end": v(1.06, 51.14) * mm});
            skLineSegment(sketch, "E1120", {"start": v(1.06, 51.14) * mm, "end": v(0.61, 50.94) * mm});
            skLineSegment(sketch, "E1121", {"start": v(0.61, 50.94) * mm, "end": v(0.2, 50.66) * mm});
            skLineSegment(sketch, "E1122", {"start": v(0.2, 50.66) * mm, "end": v(-0.13, 50.3) * mm});
            skLineSegment(sketch, "E1123", {"start": v(-0.13, 50.3) * mm, "end": v(-0.31, 50.02) * mm});
            skLineSegment(sketch, "E1124", {"start": v(-0.31, 50.02) * mm, "end": v(-0.42, 49.82) * mm});
            skLineSegment(sketch, "E1125", {"start": v(-0.42, 49.82) * mm, "end": v(-0.45, 49.75) * mm});
            skLineSegment(sketch, "E1126", {"start": v(-0.45, 49.75) * mm, "end": v(-0.48, 49.66) * mm});
            skLineSegment(sketch, "E1127", {"start": v(-0.48, 49.66) * mm, "end": v(-0.48, 49.37) * mm});
            skLineSegment(sketch, "E1128", {"start": v(-0.48, 49.37) * mm, "end": v(-0.46, 49.25) * mm});
            skLineSegment(sketch, "E1129", {"start": v(-0.46, 49.25) * mm, "end": v(-0.47, 48.94) * mm});
            skLineSegment(sketch, "E1130", {"start": v(-0.47, 48.94) * mm, "end": v(-0.46, 48.79) * mm});
            skLineSegment(sketch, "E1131", {"start": v(-0.46, 48.79) * mm, "end": v(-0.48, 48.55) * mm});
            skLineSegment(sketch, "E1132", {"start": v(-0.48, 48.55) * mm, "end": v(-0.48, 48.41) * mm});
            skLineSegment(sketch, "E1133", {"start": v(-0.48, 48.41) * mm, "end": v(-0.51, 48.2) * mm});
            skLineSegment(sketch, "E1134", {"start": v(-0.51, 48.2) * mm, "end": v(-0.51, 48.13) * mm});
            skLineSegment(sketch, "E1135", {"start": v(-0.51, 48.13) * mm, "end": v(-0.54, 48) * mm});
            skLineSegment(sketch, "E1136", {"start": v(-0.54, 48) * mm, "end": v(-0.56, 47.93) * mm});
            skLineSegment(sketch, "E1137", {"start": v(-0.56, 47.93) * mm, "end": v(-0.57, 47.9) * mm});
            skLineSegment(sketch, "E1138", {"start": v(-0.57, 47.9) * mm, "end": v(-0.62, 47.65) * mm});
            skLineSegment(sketch, "E1139", {"start": v(-0.62, 47.65) * mm, "end": v(-0.68, 47.53) * mm});
            skLineSegment(sketch, "E1140", {"start": v(-0.68, 47.53) * mm, "end": v(-0.68, 47.51) * mm});
            skLineSegment(sketch, "E1141", {"start": v(-0.68, 47.51) * mm, "end": v(-0.71, 47.46) * mm});
            skLineSegment(sketch, "E1142", {"start": v(-0.71, 47.46) * mm, "end": v(-0.82, 47.2) * mm});
            skLineSegment(sketch, "E1143", {"start": v(-0.82, 47.2) * mm, "end": v(-0.87, 47.14) * mm});
            skLineSegment(sketch, "E1144", {"start": v(-0.87, 47.14) * mm, "end": v(-0.9, 47.07) * mm});
            skLineSegment(sketch, "E1145", {"start": v(-0.9, 47.07) * mm, "end": v(-1.05, 46.89) * mm});
            skLineSegment(sketch, "E1146", {"start": v(-1.05, 46.89) * mm, "end": v(-1.1, 46.8) * mm});
            skLineSegment(sketch, "E1147", {"start": v(-1.1, 46.8) * mm, "end": v(-1.13, 46.78) * mm});
            skLineSegment(sketch, "E1148", {"start": v(-1.13, 46.78) * mm, "end": v(-1.2, 46.68) * mm});
            skLineSegment(sketch, "E1149", {"start": v(-1.2, 46.68) * mm, "end": v(-1.58, 46.36) * mm});
            skLineSegment(sketch, "E1150", {"start": v(-1.58, 46.36) * mm, "end": v(-2, 46.12) * mm});
            skLineSegment(sketch, "E1151", {"start": v(-2, 46.12) * mm, "end": v(-2.47, 45.97) * mm});
            skLineSegment(sketch, "E1152", {"start": v(-2.47, 45.97) * mm, "end": v(-2.96, 45.9) * mm});
            skLineSegment(sketch, "E1153", {"start": v(-2.96, 45.9) * mm, "end": v(-2.96, 45.9) * mm});
            skLineSegment(sketch, "E1154", {"start": v(-2.96, 45.9) * mm, "end": v(-3.45, 45.94) * mm});
            skLineSegment(sketch, "E1155", {"start": v(-3.45, 45.94) * mm, "end": v(-3.93, 46.07) * mm});
            skLineSegment(sketch, "E1156", {"start": v(-3.93, 46.07) * mm, "end": v(-4.05, 46.14) * mm});
            skLineSegment(sketch, "E1157", {"start": v(-4.05, 46.14) * mm, "end": v(-4.06, 46.14) * mm});
            skLineSegment(sketch, "E1158", {"start": v(-4.06, 46.14) * mm, "end": v(-4.08, 46.15) * mm});
            skLineSegment(sketch, "E1159", {"start": v(-4.08, 46.15) * mm, "end": v(-4.37, 46.3) * mm});
            skLineSegment(sketch, "E1160", {"start": v(-4.37, 46.3) * mm, "end": v(-4.44, 46.36) * mm});
            skLineSegment(sketch, "E1161", {"start": v(-4.44, 46.36) * mm, "end": v(-4.49, 46.38) * mm});
            skLineSegment(sketch, "E1162", {"start": v(-4.49, 46.38) * mm, "end": v(-4.6, 46.48) * mm});
            skLineSegment(sketch, "E1163", {"start": v(-4.6, 46.48) * mm, "end": v(-4.75, 46.6) * mm});
            skLineSegment(sketch, "E1164", {"start": v(-4.75, 46.6) * mm, "end": v(-4.8, 46.64) * mm});
            skLineSegment(sketch, "E1165", {"start": v(-4.8, 46.64) * mm, "end": v(-4.86, 46.7) * mm});
            skLineSegment(sketch, "E1166", {"start": v(-4.86, 46.7) * mm, "end": v(-5.03, 46.92) * mm});
            skLineSegment(sketch, "E1167", {"start": v(-5.03, 46.92) * mm, "end": v(-5.04, 46.93) * mm});
            skLineSegment(sketch, "E1168", {"start": v(-5.04, 46.93) * mm, "end": v(-5.07, 46.97) * mm});
            skLineSegment(sketch, "E1169", {"start": v(-5.07, 46.97) * mm, "end": v(-5.08, 46.99) * mm});
            skLineSegment(sketch, "E1170", {"start": v(-5.08, 46.99) * mm, "end": v(-5.16, 47.09) * mm});
            skLineSegment(sketch, "E1171", {"start": v(-5.16, 47.09) * mm, "end": v(-5.38, 47.53) * mm});
            skLineSegment(sketch, "E1172", {"start": v(-5.38, 47.53) * mm, "end": v(-5.42, 47.64) * mm});
            skLineSegment(sketch, "E1173", {"start": v(-5.42, 47.64) * mm, "end": v(-5.45, 47.7) * mm});
            skLineSegment(sketch, "E1174", {"start": v(-5.45, 47.7) * mm, "end": v(-5.5, 47.93) * mm});
            skLineSegment(sketch, "E1175", {"start": v(-5.5, 47.93) * mm, "end": v(-5.5, 47.94) * mm});
            skLineSegment(sketch, "E1176", {"start": v(-5.5, 47.94) * mm, "end": v(-5.51, 47.98) * mm});
            skLineSegment(sketch, "E1177", {"start": v(-5.51, 47.98) * mm, "end": v(-5.52, 48) * mm});
            skLineSegment(sketch, "E1178", {"start": v(-5.52, 48) * mm, "end": v(-5.52, 48.01) * mm});
            skLineSegment(sketch, "E1179", {"start": v(-5.52, 48.01) * mm, "end": v(-5.56, 48.19) * mm});
            skLineSegment(sketch, "E1180", {"start": v(-5.56, 48.19) * mm, "end": v(-5.56, 48.24) * mm});
            skLineSegment(sketch, "E1181", {"start": v(-5.56, 48.24) * mm, "end": v(-5.6, 48.43) * mm});
            skLineSegment(sketch, "E1182", {"start": v(-5.6, 48.43) * mm, "end": v(-5.6, 48.52) * mm});
            skLineSegment(sketch, "E1183", {"start": v(-5.6, 48.52) * mm, "end": v(-5.63, 48.83) * mm});
            skLineSegment(sketch, "E1184", {"start": v(-5.63, 48.83) * mm, "end": v(-5.63, 48.9) * mm});
            skLineSegment(sketch, "E1185", {"start": v(-5.63, 48.9) * mm, "end": v(-5.64, 49.17) * mm});
            skLineSegment(sketch, "E1186", {"start": v(-5.64, 49.17) * mm, "end": v(-5.65, 49.33) * mm});
            skLineSegment(sketch, "E1187", {"start": v(-5.65, 49.33) * mm, "end": v(-5.64, 49.38) * mm});
            skLineSegment(sketch, "E1188", {"start": v(-5.64, 49.38) * mm, "end": v(-5.65, 49.42) * mm});
            skLineSegment(sketch, "E1189", {"start": v(-5.65, 49.42) * mm, "end": v(-5.65, 49.56) * mm});
            skLineSegment(sketch, "E1190", {"start": v(-5.65, 49.56) * mm, "end": v(-5.73, 49.74) * mm});
            skLineSegment(sketch, "E1191", {"start": v(-5.73, 49.74) * mm, "end": v(-6.01, 50.15) * mm});
            skLineSegment(sketch, "E1192", {"start": v(-6.01, 50.15) * mm, "end": v(-6.37, 50.5) * mm});
            skLineSegment(sketch, "E1193", {"start": v(-6.37, 50.5) * mm, "end": v(-6.78, 50.76) * mm});
            skLineSegment(sketch, "E1194", {"start": v(-6.78, 50.76) * mm, "end": v(-7.24, 50.94) * mm});
            skLineSegment(sketch, "E1195", {"start": v(-7.24, 50.94) * mm, "end": v(-7.72, 51.03) * mm});
            skLineSegment(sketch, "E1196", {"start": v(-7.72, 51.03) * mm, "end": v(-7.72, 51.03) * mm});
            skLineSegment(sketch, "E1197", {"start": v(-7.72, 51.03) * mm, "end": v(-8.22, 51.02) * mm});
            skLineSegment(sketch, "E1198", {"start": v(-8.22, 51.02) * mm, "end": v(-8.63, 50.93) * mm});
            skLineSegment(sketch, "E1199", {"start": v(-8.63, 50.93) * mm, "end": v(-8.72, 50.9) * mm});
            skLineSegment(sketch, "E1200", {"start": v(-8.72, 50.9) * mm, "end": v(-8.92, 50.82) * mm});
            skLineSegment(sketch, "E1201", {"start": v(-8.92, 50.82) * mm, "end": v(-9, 50.79) * mm});
            skLineSegment(sketch, "E1202", {"start": v(-9, 50.79) * mm, "end": v(-9.2, 50.68) * mm});
            skLineSegment(sketch, "E1203", {"start": v(-9.2, 50.68) * mm, "end": v(-9.33, 50.6) * mm});
            skLineSegment(sketch, "E1204", {"start": v(-9.33, 50.6) * mm, "end": v(-9.64, 50.35) * mm});
            skLineSegment(sketch, "E1205", {"start": v(-9.64, 50.35) * mm, "end": v(-9.64, 50.35) * mm});
            skLineSegment(sketch, "E1206", {"start": v(-9.64, 50.35) * mm, "end": v(-9.96, 49.98) * mm});
            skLineSegment(sketch, "E1207", {"start": v(-9.96, 49.98) * mm, "end": v(-10.2, 49.55) * mm});
            skLineSegment(sketch, "E1208", {"start": v(-10.2, 49.55) * mm, "end": v(-10.21, 49.51) * mm});
            skLineSegment(sketch, "E1209", {"start": v(-10.21, 49.51) * mm, "end": v(-10.25, 49.4) * mm});
            skLineSegment(sketch, "E1210", {"start": v(-10.25, 49.4) * mm, "end": v(-10.25, 49.22) * mm});
            skLineSegment(sketch, "E1211", {"start": v(-10.25, 49.22) * mm, "end": v(-10.27, 49.1) * mm});
            skLineSegment(sketch, "E1212", {"start": v(-10.27, 49.1) * mm, "end": v(-10.28, 48.82) * mm});
            skLineSegment(sketch, "E1213", {"start": v(-10.28, 48.82) * mm, "end": v(-10.3, 48.69) * mm});
            skLineSegment(sketch, "E1214", {"start": v(-10.3, 48.69) * mm, "end": v(-10.32, 48.5) * mm});
            skLineSegment(sketch, "E1215", {"start": v(-10.32, 48.5) * mm, "end": v(-10.37, 48.33) * mm});
            skLineSegment(sketch, "E1216", {"start": v(-10.37, 48.33) * mm, "end": v(-10.38, 48.26) * mm});
            skLineSegment(sketch, "E1217", {"start": v(-10.38, 48.26) * mm, "end": v(-10.43, 48.12) * mm});
            skLineSegment(sketch, "E1218", {"start": v(-10.43, 48.12) * mm, "end": v(-10.46, 48.02) * mm});
            skLineSegment(sketch, "E1219", {"start": v(-10.46, 48.02) * mm, "end": v(-10.48, 47.99) * mm});
            skLineSegment(sketch, "E1220", {"start": v(-10.48, 47.99) * mm, "end": v(-10.55, 47.8) * mm});
            skLineSegment(sketch, "E1221", {"start": v(-10.55, 47.8) * mm, "end": v(-10.8, 47.38) * mm});
            skLineSegment(sketch, "E1222", {"start": v(-10.8, 47.38) * mm, "end": v(-11.13, 47) * mm});
            skLineSegment(sketch, "E1223", {"start": v(-11.13, 47) * mm, "end": v(-11.52, 46.71) * mm});
            skLineSegment(sketch, "E1224", {"start": v(-11.52, 46.71) * mm, "end": v(-11.97, 46.5) * mm});
            skLineSegment(sketch, "E1225", {"start": v(-11.97, 46.5) * mm, "end": v(-12.06, 46.48) * mm});
            skLineSegment(sketch, "E1226", {"start": v(-12.06, 46.48) * mm, "end": v(-12.11, 46.47) * mm});
            skLineSegment(sketch, "E1227", {"start": v(-12.11, 46.47) * mm, "end": v(-12.13, 46.46) * mm});
            skLineSegment(sketch, "E1228", {"start": v(-12.13, 46.46) * mm, "end": v(-12.18, 46.45) * mm});
            skLineSegment(sketch, "E1229", {"start": v(-12.18, 46.45) * mm, "end": v(-12.45, 46.38) * mm});
            skLineSegment(sketch, "E1230", {"start": v(-12.45, 46.38) * mm, "end": v(-12.56, 46.38) * mm});
            skLineSegment(sketch, "E1231", {"start": v(-12.56, 46.38) * mm, "end": v(-12.62, 46.37) * mm});
            skLineSegment(sketch, "E1232", {"start": v(-12.62, 46.37) * mm, "end": v(-12.75, 46.37) * mm});
            skLineSegment(sketch, "E1233", {"start": v(-12.75, 46.37) * mm, "end": v(-12.94, 46.36) * mm});
            skLineSegment(sketch, "E1234", {"start": v(-12.94, 46.36) * mm, "end": v(-12.94, 46.36) * mm});
            skLineSegment(sketch, "E1235", {"start": v(-12.94, 46.36) * mm, "end": v(-13.02, 46.37) * mm});
            skLineSegment(sketch, "E1236", {"start": v(-13.02, 46.37) * mm, "end": v(-13.1, 46.37) * mm});
            skLineSegment(sketch, "E1237", {"start": v(-13.1, 46.37) * mm, "end": v(-13.11, 46.37) * mm});
            skLineSegment(sketch, "E1238", {"start": v(-13.11, 46.37) * mm, "end": v(-13.32, 46.41) * mm});
            skLineSegment(sketch, "E1239", {"start": v(-13.32, 46.41) * mm, "end": v(-13.43, 46.43) * mm});
            skLineSegment(sketch, "E1240", {"start": v(-13.43, 46.43) * mm, "end": v(-13.47, 46.44) * mm});
            skLineSegment(sketch, "E1241", {"start": v(-13.47, 46.44) * mm, "end": v(-13.6, 46.47) * mm});
            skLineSegment(sketch, "E1242", {"start": v(-13.6, 46.47) * mm, "end": v(-13.87, 46.58) * mm});
            skLineSegment(sketch, "E1243", {"start": v(-13.87, 46.58) * mm, "end": v(-13.9, 46.6) * mm});
            skLineSegment(sketch, "E1244", {"start": v(-13.9, 46.6) * mm, "end": v(-13.9, 46.6) * mm});
            skLineSegment(sketch, "E1245", {"start": v(-13.9, 46.6) * mm, "end": v(-14.05, 46.66) * mm});
            skLineSegment(sketch, "E1246", {"start": v(-14.05, 46.66) * mm, "end": v(-14.46, 46.94) * mm});
            skLineSegment(sketch, "E1247", {"start": v(-14.46, 46.94) * mm, "end": v(-14.8, 47.29) * mm});
            skLineSegment(sketch, "E1248", {"start": v(-14.8, 47.29) * mm, "end": v(-15.07, 47.7) * mm});
            skLineSegment(sketch, "E1249", {"start": v(-15.07, 47.7) * mm, "end": v(-15.26, 48.16) * mm});
            skLineSegment(sketch, "E1250", {"start": v(-15.26, 48.16) * mm, "end": v(-15.3, 48.34) * mm});
            skLineSegment(sketch, "E1251", {"start": v(-15.3, 48.34) * mm, "end": v(-15.31, 48.4) * mm});
            skLineSegment(sketch, "E1252", {"start": v(-15.31, 48.4) * mm, "end": v(-15.33, 48.53) * mm});
            skLineSegment(sketch, "E1253", {"start": v(-15.33, 48.53) * mm, "end": v(-15.35, 48.64) * mm});
            skLineSegment(sketch, "E1254", {"start": v(-15.35, 48.64) * mm, "end": v(-15.35, 48.69) * mm});
            skLineSegment(sketch, "E1255", {"start": v(-15.35, 48.69) * mm, "end": v(-15.38, 48.88) * mm});
            skLineSegment(sketch, "E1256", {"start": v(-15.38, 48.88) * mm, "end": v(-15.37, 49.05) * mm});
            skLineSegment(sketch, "E1257", {"start": v(-15.37, 49.05) * mm, "end": v(-15.38, 49.22) * mm});
            skLineSegment(sketch, "E1258", {"start": v(-15.38, 49.22) * mm, "end": v(-15.35, 49.45) * mm});
            skLineSegment(sketch, "E1259", {"start": v(-15.35, 49.45) * mm, "end": v(-15.35, 49.66) * mm});
            skLineSegment(sketch, "E1260", {"start": v(-15.35, 49.66) * mm, "end": v(-15.34, 49.69) * mm});
            skLineSegment(sketch, "E1261", {"start": v(-15.34, 49.69) * mm, "end": v(-15.4, 49.94) * mm});
            skLineSegment(sketch, "E1262", {"start": v(-15.4, 49.94) * mm, "end": v(-15.6, 50.4) * mm});
            skLineSegment(sketch, "E1263", {"start": v(-15.6, 50.4) * mm, "end": v(-15.86, 50.76) * mm});
            skLineSegment(sketch, "E1264", {"start": v(-15.86, 50.76) * mm, "end": v(-15.9, 50.8) * mm});
            skLineSegment(sketch, "E1265", {"start": v(-15.9, 50.8) * mm, "end": v(-16.14, 51.04) * mm});
            skLineSegment(sketch, "E1266", {"start": v(-16.14, 51.04) * mm, "end": v(-16.3, 51.16) * mm});
            skLineSegment(sketch, "E1267", {"start": v(-16.3, 51.16) * mm, "end": v(-16.46, 51.27) * mm});
            skLineSegment(sketch, "E1268", {"start": v(-16.46, 51.27) * mm, "end": v(-16.75, 51.43) * mm});
            skLineSegment(sketch, "E1269", {"start": v(-16.75, 51.43) * mm, "end": v(-16.8, 51.45) * mm});
            skLineSegment(sketch, "E1270", {"start": v(-16.8, 51.45) * mm, "end": v(-16.82, 51.45) * mm});
            skLineSegment(sketch, "E1271", {"start": v(-16.82, 51.45) * mm, "end": v(-17.24, 51.6) * mm});
            skLineSegment(sketch, "E1272", {"start": v(-17.24, 51.6) * mm, "end": v(-17.73, 51.65) * mm});
            skLineSegment(sketch, "E1273", {"start": v(-17.73, 51.65) * mm, "end": v(-17.73, 51.65) * mm});
            skLineSegment(sketch, "E1274", {"start": v(-17.73, 51.65) * mm, "end": v(-18.22, 51.6) * mm});
            skLineSegment(sketch, "E1275", {"start": v(-18.22, 51.6) * mm, "end": v(-18.7, 51.47) * mm});
            skLineSegment(sketch, "E1276", {"start": v(-18.7, 51.47) * mm, "end": v(-19.14, 51.24) * mm});
            skLineSegment(sketch, "E1277", {"start": v(-19.14, 51.24) * mm, "end": v(-19.52, 50.94) * mm});
            skLineSegment(sketch, "E1278", {"start": v(-19.52, 50.94) * mm, "end": v(-19.84, 50.56) * mm});
            skLineSegment(sketch, "E1279", {"start": v(-19.84, 50.56) * mm, "end": v(-20.08, 50.13) * mm});
            skLineSegment(sketch, "E1280", {"start": v(-20.08, 50.13) * mm, "end": v(-20.15, 49.9) * mm});
            skLineSegment(sketch, "E1281", {"start": v(-20.15, 49.9) * mm, "end": v(-20.22, 49.64) * mm});
            skLineSegment(sketch, "E1282", {"start": v(-20.22, 49.64) * mm, "end": v(-20.2, 49.49) * mm});
            skLineSegment(sketch, "E1283", {"start": v(-20.2, 49.49) * mm, "end": v(-20.2, 49.4) * mm});
            skLineSegment(sketch, "E1284", {"start": v(-20.2, 49.4) * mm, "end": v(-20.19, 49.16) * mm});
            skLineSegment(sketch, "E1285", {"start": v(-20.19, 49.16) * mm, "end": v(-20.2, 49.03) * mm});
            skLineSegment(sketch, "E1286", {"start": v(-20.2, 49.03) * mm, "end": v(-20.2, 48.9) * mm});
            skLineSegment(sketch, "E1287", {"start": v(-20.2, 48.9) * mm, "end": v(-20.3, 48.42) * mm});
            skLineSegment(sketch, "E1288", {"start": v(-20.3, 48.42) * mm, "end": v(-20.33, 48.3) * mm});
            skLineSegment(sketch, "E1289", {"start": v(-20.33, 48.3) * mm, "end": v(-20.35, 48.24) * mm});
            skLineSegment(sketch, "E1290", {"start": v(-20.35, 48.24) * mm, "end": v(-20.42, 48.09) * mm});
            skLineSegment(sketch, "E1291", {"start": v(-20.42, 48.09) * mm, "end": v(-20.47, 47.96) * mm});
            skLineSegment(sketch, "E1292", {"start": v(-20.47, 47.96) * mm, "end": v(-20.5, 47.91) * mm});
            skLineSegment(sketch, "E1293", {"start": v(-20.5, 47.91) * mm, "end": v(-20.55, 47.8) * mm});
            skLineSegment(sketch, "E1294", {"start": v(-20.55, 47.8) * mm, "end": v(-20.84, 47.4) * mm});
            skLineSegment(sketch, "E1295", {"start": v(-20.84, 47.4) * mm, "end": v(-21.2, 47.06) * mm});
            skLineSegment(sketch, "E1296", {"start": v(-21.2, 47.06) * mm, "end": v(-21.62, 46.8) * mm});
            skLineSegment(sketch, "E1297", {"start": v(-21.62, 46.8) * mm, "end": v(-22.09, 46.63) * mm});
            skLineSegment(sketch, "E1298", {"start": v(-22.09, 46.63) * mm, "end": v(-22.57, 46.55) * mm});
            skLineSegment(sketch, "E1299", {"start": v(-22.57, 46.55) * mm, "end": v(-22.58, 46.55) * mm});
            skLineSegment(sketch, "E1300", {"start": v(-22.58, 46.55) * mm, "end": v(-23.07, 46.57) * mm});
            skLineSegment(sketch, "E1301", {"start": v(-23.07, 46.57) * mm, "end": v(-23.55, 46.68) * mm});
            skLineSegment(sketch, "E1302", {"start": v(-23.55, 46.68) * mm, "end": v(-24, 46.88) * mm});
            skLineSegment(sketch, "E1303", {"start": v(-24, 46.88) * mm, "end": v(-24.4, 47.17) * mm});
            skLineSegment(sketch, "E1304", {"start": v(-24.4, 47.17) * mm, "end": v(-24.5, 47.3) * mm});
            skLineSegment(sketch, "E1305", {"start": v(-24.5, 47.3) * mm, "end": v(-24.52, 47.3) * mm});
            skLineSegment(sketch, "E1306", {"start": v(-24.52, 47.3) * mm, "end": v(-24.55, 47.34) * mm});
            skLineSegment(sketch, "E1307", {"start": v(-24.55, 47.34) * mm, "end": v(-24.73, 47.54) * mm});
            skLineSegment(sketch, "E1308", {"start": v(-24.73, 47.54) * mm, "end": v(-24.79, 47.62) * mm});
            skLineSegment(sketch, "E1309", {"start": v(-24.79, 47.62) * mm, "end": v(-24.84, 47.68) * mm});
            skLineSegment(sketch, "E1310", {"start": v(-24.84, 47.68) * mm, "end": v(-24.94, 47.86) * mm});
            skLineSegment(sketch, "E1311", {"start": v(-24.94, 47.86) * mm, "end": v(-25, 47.96) * mm});
            skLineSegment(sketch, "E1312", {"start": v(-25, 47.96) * mm, "end": v(-25, 48) * mm});
            skLineSegment(sketch, "E1313", {"start": v(-25, 48) * mm, "end": v(-25.04, 48.05) * mm});
            skLineSegment(sketch, "E1314", {"start": v(-25.04, 48.05) * mm, "end": v(-25.07, 48.12) * mm});
            skLineSegment(sketch, "E1315", {"start": v(-25.07, 48.12) * mm, "end": v(-25.22, 48.59) * mm});
            skLineSegment(sketch, "E1316", {"start": v(-25.22, 48.59) * mm, "end": v(-25.23, 48.7) * mm});
            skLineSegment(sketch, "E1317", {"start": v(-25.23, 48.7) * mm, "end": v(-25.27, 48.84) * mm});
            skLineSegment(sketch, "E1318", {"start": v(-25.27, 48.84) * mm, "end": v(-25.28, 49.1) * mm});
            skLineSegment(sketch, "E1319", {"start": v(-25.28, 49.1) * mm, "end": v(-25.3, 49.2) * mm});
            skLineSegment(sketch, "E1320", {"start": v(-25.3, 49.2) * mm, "end": v(-25.3, 49.3) * mm});
            skLineSegment(sketch, "E1321", {"start": v(-25.3, 49.3) * mm, "end": v(-25.42, 49.59) * mm});
            skLineSegment(sketch, "E1322", {"start": v(-25.42, 49.59) * mm, "end": v(-25.53, 49.8) * mm});
            skLineSegment(sketch, "E1323", {"start": v(-25.53, 49.8) * mm, "end": v(-25.83, 50.18) * mm});
            skLineSegment(sketch, "E1324", {"start": v(-25.83, 50.18) * mm, "end": v(-26.2, 50.5) * mm});
            skLineSegment(sketch, "E1325", {"start": v(-26.2, 50.5) * mm, "end": v(-26.63, 50.75) * mm});
            skLineSegment(sketch, "E1326", {"start": v(-26.63, 50.75) * mm, "end": v(-27.1, 50.9) * mm});
            skLineSegment(sketch, "E1327", {"start": v(-27.1, 50.9) * mm, "end": v(-27.59, 50.97) * mm});
            skLineSegment(sketch, "E1328", {"start": v(-27.59, 50.97) * mm, "end": v(-28.08, 50.93) * mm});
            skLineSegment(sketch, "E1329", {"start": v(-28.08, 50.93) * mm, "end": v(-28.08, 50.93) * mm});
            skLineSegment(sketch, "E1330", {"start": v(-28.08, 50.93) * mm, "end": v(-28.56, 50.8) * mm});
            skLineSegment(sketch, "E1331", {"start": v(-28.56, 50.8) * mm, "end": v(-29, 50.58) * mm});
            skLineSegment(sketch, "E1332", {"start": v(-29, 50.58) * mm, "end": v(-29.35, 50.3) * mm});
            skLineSegment(sketch, "E1333", {"start": v(-29.35, 50.3) * mm, "end": v(-29.4, 50.26) * mm});
            skLineSegment(sketch, "E1334", {"start": v(-29.4, 50.26) * mm, "end": v(-29.6, 50.03) * mm});
            skLineSegment(sketch, "E1335", {"start": v(-29.6, 50.03) * mm, "end": v(-29.76, 49.83) * mm});
            skLineSegment(sketch, "E1336", {"start": v(-29.76, 49.83) * mm, "end": v(-29.82, 49.71) * mm});
            skLineSegment(sketch, "E1337", {"start": v(-29.82, 49.71) * mm, "end": v(-30, 49.35) * mm});
            skLineSegment(sketch, "E1338", {"start": v(-30, 49.35) * mm, "end": v(-30.12, 48.87) * mm});
            skLineSegment(sketch, "E1339", {"start": v(-30.12, 48.87) * mm, "end": v(-30.15, 48.4) * mm});
            skLineSegment(sketch, "E1340", {"start": v(-30.15, 48.4) * mm, "end": v(-30.15, 48.37) * mm});
            skLineSegment(sketch, "E1341", {"start": v(-30.15, 48.37) * mm, "end": v(-30.15, 48.35) * mm});
            skLineSegment(sketch, "E1342", {"start": v(-30.15, 48.35) * mm, "end": v(-30.14, 48.31) * mm});
            skLineSegment(sketch, "E1343", {"start": v(-30.14, 48.31) * mm, "end": v(-30.04, 48.06) * mm});
            skLineSegment(sketch, "E1344", {"start": v(-30.04, 48.06) * mm, "end": v(-30, 47.91) * mm});
            skLineSegment(sketch, "E1345", {"start": v(-30, 47.91) * mm, "end": v(-29.95, 47.74) * mm});
            skLineSegment(sketch, "E1346", {"start": v(-29.95, 47.74) * mm, "end": v(-29.89, 47.25) * mm});
            skLineSegment(sketch, "E1347", {"start": v(-29.89, 47.25) * mm, "end": v(-29.9, 47.07) * mm});
            skLineSegment(sketch, "E1348", {"start": v(-29.9, 47.07) * mm, "end": v(-29.9, 47.02) * mm});
            skLineSegment(sketch, "E1349", {"start": v(-29.9, 47.02) * mm, "end": v(-29.91, 46.9) * mm});
            skLineSegment(sketch, "E1350", {"start": v(-29.91, 46.9) * mm, "end": v(-29.92, 46.75) * mm});
            skLineSegment(sketch, "E1351", {"start": v(-29.92, 46.75) * mm, "end": v(-29.94, 46.68) * mm});
            skLineSegment(sketch, "E1352", {"start": v(-29.94, 46.68) * mm, "end": v(-29.97, 46.53) * mm});
            skLineSegment(sketch, "E1353", {"start": v(-29.97, 46.53) * mm, "end": v(-30.13, 46.06) * mm});
            skLineSegment(sketch, "E1354", {"start": v(-30.13, 46.06) * mm, "end": v(-30.38, 45.64) * mm});
            skLineSegment(sketch, "E1355", {"start": v(-30.38, 45.64) * mm, "end": v(-30.7, 45.27) * mm});
            skLineSegment(sketch, "E1356", {"start": v(-30.7, 45.27) * mm, "end": v(-31.1, 44.97) * mm});
            skLineSegment(sketch, "E1357", {"start": v(-31.1, 44.97) * mm, "end": v(-31.54, 44.76) * mm});
            skLineSegment(sketch, "E1358", {"start": v(-31.54, 44.76) * mm, "end": v(-31.54, 44.76) * mm});
            skLineSegment(sketch, "E1359", {"start": v(-31.54, 44.76) * mm, "end": v(-32.02, 44.63) * mm});
            skLineSegment(sketch, "E1360", {"start": v(-32.02, 44.63) * mm, "end": v(-32.51, 44.6) * mm});
            skLineSegment(sketch, "E1361", {"start": v(-32.51, 44.6) * mm, "end": v(-33, 44.67) * mm});
            skLineSegment(sketch, "E1362", {"start": v(-33, 44.67) * mm, "end": v(-33.47, 44.83) * mm});
            skLineSegment(sketch, "E1363", {"start": v(-33.47, 44.83) * mm, "end": v(-33.9, 45.08) * mm});
            skLineSegment(sketch, "E1364", {"start": v(-33.9, 45.08) * mm, "end": v(-34.04, 45.22) * mm});
            skLineSegment(sketch, "E1365", {"start": v(-34.04, 45.22) * mm, "end": v(-34.08, 45.24) * mm});
            skLineSegment(sketch, "E1366", {"start": v(-34.08, 45.24) * mm, "end": v(-34.13, 45.3) * mm});
            skLineSegment(sketch, "E1367", {"start": v(-34.13, 45.3) * mm, "end": v(-34.26, 45.41) * mm});
            skLineSegment(sketch, "E1368", {"start": v(-34.26, 45.41) * mm, "end": v(-34.32, 45.48) * mm});
            skLineSegment(sketch, "E1369", {"start": v(-34.32, 45.48) * mm, "end": v(-34.42, 45.6) * mm});
            skLineSegment(sketch, "E1370", {"start": v(-34.42, 45.6) * mm, "end": v(-34.7, 46) * mm});
            skLineSegment(sketch, "E1371", {"start": v(-34.7, 46) * mm, "end": v(-34.78, 46.22) * mm});
            skLineSegment(sketch, "E1372", {"start": v(-34.78, 46.22) * mm, "end": v(-34.84, 46.34) * mm});
            skLineSegment(sketch, "E1373", {"start": v(-34.84, 46.34) * mm, "end": v(-34.92, 46.56) * mm});
            skLineSegment(sketch, "E1374", {"start": v(-34.92, 46.56) * mm, "end": v(-34.93, 46.59) * mm});
            skLineSegment(sketch, "E1375", {"start": v(-34.93, 46.59) * mm, "end": v(-34.94, 46.6) * mm});
            skLineSegment(sketch, "E1376", {"start": v(-34.94, 46.6) * mm, "end": v(-35.27, 46.96) * mm});
            skLineSegment(sketch, "E1377", {"start": v(-35.27, 46.96) * mm, "end": v(-35.57, 47.17) * mm});
            skLineSegment(sketch, "E1378", {"start": v(-35.57, 47.17) * mm, "end": v(-35.74, 47.27) * mm});
            skLineSegment(sketch, "E1379", {"start": v(-35.74, 47.27) * mm, "end": v(-35.79, 47.3) * mm});
            skLineSegment(sketch, "E1380", {"start": v(-35.79, 47.3) * mm, "end": v(-35.85, 47.32) * mm});
            skLineSegment(sketch, "E1381", {"start": v(-35.85, 47.32) * mm, "end": v(-36.23, 47.47) * mm});
            skLineSegment(sketch, "E1382", {"start": v(-36.23, 47.47) * mm, "end": v(-36.72, 47.55) * mm});
            skLineSegment(sketch, "E1383", {"start": v(-36.72, 47.55) * mm, "end": v(-37.21, 47.53) * mm});
            skLineSegment(sketch, "E1384", {"start": v(-37.21, 47.53) * mm, "end": v(-37.7, 47.42) * mm});
            skLineSegment(sketch, "E1385", {"start": v(-37.7, 47.42) * mm, "end": v(-38.14, 47.22) * mm});
            skLineSegment(sketch, "E1386", {"start": v(-38.14, 47.22) * mm, "end": v(-38.14, 47.22) * mm});
            skLineSegment(sketch, "E1387", {"start": v(-38.14, 47.22) * mm, "end": v(-38.55, 46.93) * mm});
            skLineSegment(sketch, "E1388", {"start": v(-38.55, 46.93) * mm, "end": v(-38.88, 46.57) * mm});
            skLineSegment(sketch, "E1389", {"start": v(-38.88, 46.57) * mm, "end": v(-39.15, 46.16) * mm});
            skLineSegment(sketch, "E1390", {"start": v(-39.15, 46.16) * mm, "end": v(-39.32, 45.7) * mm});
            skLineSegment(sketch, "E1391", {"start": v(-39.32, 45.7) * mm, "end": v(-39.4, 45.2) * mm});
            skLineSegment(sketch, "E1392", {"start": v(-39.4, 45.2) * mm, "end": v(-39.4, 44.88) * mm});
            skLineSegment(sketch, "E1393", {"start": v(-39.4, 44.88) * mm, "end": v(-39.37, 44.63) * mm});
            skLineSegment(sketch, "E1394", {"start": v(-39.37, 44.63) * mm, "end": v(-39.36, 44.6) * mm});
            skLineSegment(sketch, "E1395", {"start": v(-39.36, 44.6) * mm, "end": v(-39.23, 44.16) * mm});
            skLineSegment(sketch, "E1396", {"start": v(-39.23, 44.16) * mm, "end": v(-39.01, 43.9) * mm});
            skLineSegment(sketch, "E1397", {"start": v(-39.01, 43.9) * mm, "end": v(-38.93, 43.76) * mm});
            skLineSegment(sketch, "E1398", {"start": v(-38.93, 43.76) * mm, "end": v(-38.84, 43.64) * mm});
            skLineSegment(sketch, "E1399", {"start": v(-38.84, 43.64) * mm, "end": v(-38.62, 43.2) * mm});
            skLineSegment(sketch, "E1400", {"start": v(-38.62, 43.2) * mm, "end": v(-38.58, 43.03) * mm});
            skLineSegment(sketch, "E1401", {"start": v(-38.58, 43.03) * mm, "end": v(-38.56, 42.97) * mm});
            skLineSegment(sketch, "E1402", {"start": v(-38.56, 42.97) * mm, "end": v(-38.54, 42.85) * mm});
            skLineSegment(sketch, "E1403", {"start": v(-38.54, 42.85) * mm, "end": v(-38.5, 42.71) * mm});
            skLineSegment(sketch, "E1404", {"start": v(-38.5, 42.71) * mm, "end": v(-38.5, 42.64) * mm});
            skLineSegment(sketch, "E1405", {"start": v(-38.5, 42.64) * mm, "end": v(-38.47, 42.49) * mm});
            skLineSegment(sketch, "E1406", {"start": v(-38.47, 42.49) * mm, "end": v(-38.47, 42) * mm});
            skLineSegment(sketch, "E1407", {"start": v(-38.47, 42) * mm, "end": v(-38.57, 41.51) * mm});
            skLineSegment(sketch, "E1408", {"start": v(-38.57, 41.51) * mm, "end": v(-38.77, 41.06) * mm});
            skLineSegment(sketch, "E1409", {"start": v(-38.77, 41.06) * mm, "end": v(-39.04, 40.65) * mm});
            skLineSegment(sketch, "E1410", {"start": v(-39.04, 40.65) * mm, "end": v(-39.4, 40.3) * mm});
            skLineSegment(sketch, "E1411", {"start": v(-39.4, 40.3) * mm, "end": v(-39.4, 40.3) * mm});
            skLineSegment(sketch, "E1412", {"start": v(-39.4, 40.3) * mm, "end": v(-39.8, 40.03) * mm});
            skLineSegment(sketch, "E1413", {"start": v(-39.8, 40.03) * mm, "end": v(-40.27, 39.85) * mm});
            skLineSegment(sketch, "E1414", {"start": v(-40.27, 39.85) * mm, "end": v(-40.75, 39.76) * mm});
            skLineSegment(sketch, "E1415", {"start": v(-40.75, 39.76) * mm, "end": v(-41.24, 39.76) * mm});
            skLineSegment(sketch, "E1416", {"start": v(-41.24, 39.76) * mm, "end": v(-41.44, 39.8) * mm});
            skLineSegment(sketch, "E1417", {"start": v(-41.44, 39.8) * mm, "end": v(-41.46, 39.8) * mm});
            skLineSegment(sketch, "E1418", {"start": v(-41.46, 39.8) * mm, "end": v(-41.49, 39.81) * mm});
            skLineSegment(sketch, "E1419", {"start": v(-41.49, 39.81) * mm, "end": v(-41.73, 39.86) * mm});
            skLineSegment(sketch, "E1420", {"start": v(-41.73, 39.86) * mm, "end": v(-41.84, 39.9) * mm});
            skLineSegment(sketch, "E1421", {"start": v(-41.84, 39.9) * mm, "end": v(-41.93, 39.93) * mm});
            skLineSegment(sketch, "E1422", {"start": v(-41.93, 39.93) * mm, "end": v(-42.12, 40.03) * mm});
            skLineSegment(sketch, "E1423", {"start": v(-42.12, 40.03) * mm, "end": v(-42.18, 40.05) * mm});
            skLineSegment(sketch, "E1424", {"start": v(-42.18, 40.05) * mm, "end": v(-42.2, 40.07) * mm});
            skLineSegment(sketch, "E1425", {"start": v(-42.2, 40.07) * mm, "end": v(-42.26, 40.1) * mm});
            skLineSegment(sketch, "E1426", {"start": v(-42.26, 40.1) * mm, "end": v(-42.37, 40.15) * mm});
            skLineSegment(sketch, "E1427", {"start": v(-42.37, 40.15) * mm, "end": v(-42.76, 40.46) * mm});
            skLineSegment(sketch, "E1428", {"start": v(-42.76, 40.46) * mm, "end": v(-42.86, 40.57) * mm});
            skLineSegment(sketch, "E1429", {"start": v(-42.86, 40.57) * mm, "end": v(-42.99, 40.69) * mm});
            skLineSegment(sketch, "E1430", {"start": v(-42.99, 40.69) * mm, "end": v(-43.2, 40.97) * mm});
            skLineSegment(sketch, "E1431", {"start": v(-43.2, 40.97) * mm, "end": v(-43.2, 40.97) * mm});
            skLineSegment(sketch, "E1432", {"start": v(-43.2, 40.97) * mm, "end": v(-43.48, 41.12) * mm});
            skLineSegment(sketch, "E1433", {"start": v(-43.48, 41.12) * mm, "end": v(-43.63, 41.2) * mm});
            skLineSegment(sketch, "E1434", {"start": v(-43.63, 41.2) * mm, "end": v(-43.92, 41.3) * mm});
            skLineSegment(sketch, "E1435", {"start": v(-43.92, 41.3) * mm, "end": v(-44.19, 41.37) * mm});
            skLineSegment(sketch, "E1436", {"start": v(-44.19, 41.37) * mm, "end": v(-44.2, 41.37) * mm});
            skLineSegment(sketch, "E1437", {"start": v(-44.2, 41.37) * mm, "end": v(-44.69, 41.4) * mm});
            skLineSegment(sketch, "E1438", {"start": v(-44.69, 41.4) * mm, "end": v(-45.17, 41.32) * mm});
            skLineSegment(sketch, "E1439", {"start": v(-45.17, 41.32) * mm, "end": v(-45.64, 41.16) * mm});
            skLineSegment(sketch, "E1440", {"start": v(-45.64, 41.16) * mm, "end": v(-46.06, 40.9) * mm});
            skLineSegment(sketch, "E1441", {"start": v(-46.06, 40.9) * mm, "end": v(-46.43, 40.58) * mm});
            skLineSegment(sketch, "E1442", {"start": v(-46.43, 40.58) * mm, "end": v(-46.43, 40.57) * mm});
            skLineSegment(sketch, "E1443", {"start": v(-46.43, 40.57) * mm, "end": v(-46.73, 40.18) * mm});
            skLineSegment(sketch, "E1444", {"start": v(-46.73, 40.18) * mm, "end": v(-46.94, 39.73) * mm});
            skLineSegment(sketch, "E1445", {"start": v(-46.94, 39.73) * mm, "end": v(-47.06, 39.25) * mm});
            skLineSegment(sketch, "E1446", {"start": v(-47.06, 39.25) * mm, "end": v(-47.09, 38.76) * mm});
            skLineSegment(sketch, "E1447", {"start": v(-47.09, 38.76) * mm, "end": v(-47.03, 38.4) * mm});
            skLineSegment(sketch, "E1448", {"start": v(-47.03, 38.4) * mm, "end": v(-47, 38.21) * mm});
            skLineSegment(sketch, "E1449", {"start": v(-47, 38.21) * mm, "end": v(-46.95, 38.1) * mm});
            skLineSegment(sketch, "E1450", {"start": v(-46.95, 38.1) * mm, "end": v(-46.79, 37.72) * mm});
            skLineSegment(sketch, "E1451", {"start": v(-46.79, 37.72) * mm, "end": v(-46.55, 37.37) * mm});
            skLineSegment(sketch, "E1452", {"start": v(-46.55, 37.37) * mm, "end": v(-46.54, 37.35) * mm});
            skLineSegment(sketch, "E1453", {"start": v(-46.54, 37.35) * mm, "end": v(-46.46, 37.3) * mm});
            skLineSegment(sketch, "E1454", {"start": v(-46.46, 37.3) * mm, "end": v(-46.36, 37.23) * mm});
            skLineSegment(sketch, "E1455", {"start": v(-46.36, 37.23) * mm, "end": v(-46.14, 37.09) * mm});
            skLineSegment(sketch, "E1456", {"start": v(-46.14, 37.09) * mm, "end": v(-45.99, 36.95) * mm});
            skLineSegment(sketch, "E1457", {"start": v(-45.99, 36.95) * mm, "end": v(-45.92, 36.9) * mm});
            skLineSegment(sketch, "E1458", {"start": v(-45.92, 36.9) * mm, "end": v(-45.8, 36.77) * mm});
            skLineSegment(sketch, "E1459", {"start": v(-45.8, 36.77) * mm, "end": v(-45.78, 36.75) * mm});
            skLineSegment(sketch, "E1460", {"start": v(-45.78, 36.75) * mm, "end": v(-45.77, 36.74) * mm});
            skLineSegment(sketch, "E1461", {"start": v(-45.77, 36.74) * mm, "end": v(-45.58, 36.54) * mm});
            skLineSegment(sketch, "E1462", {"start": v(-45.58, 36.54) * mm, "end": v(-45.32, 36.12) * mm});
            skLineSegment(sketch, "E1463", {"start": v(-45.32, 36.12) * mm, "end": v(-45.26, 35.94) * mm});
            skLineSegment(sketch, "E1464", {"start": v(-45.26, 35.94) * mm, "end": v(-45.25, 35.93) * mm});
            skLineSegment(sketch, "E1465", {"start": v(-45.25, 35.93) * mm, "end": v(-45.24, 35.9) * mm});
            skLineSegment(sketch, "E1466", {"start": v(-45.24, 35.9) * mm, "end": v(-45.15, 35.65) * mm});
            skLineSegment(sketch, "E1467", {"start": v(-45.15, 35.65) * mm, "end": v(-45.13, 35.53) * mm});
            skLineSegment(sketch, "E1468", {"start": v(-45.13, 35.53) * mm, "end": v(-45.1, 35.46) * mm});
            skLineSegment(sketch, "E1469", {"start": v(-45.1, 35.46) * mm, "end": v(-45.1, 35.3) * mm});
            skLineSegment(sketch, "E1470", {"start": v(-45.1, 35.3) * mm, "end": v(-45.07, 35.17) * mm});
            skLineSegment(sketch, "E1471", {"start": v(-45.07, 35.17) * mm, "end": v(-45.07, 35.1) * mm});
            skLineSegment(sketch, "E1472", {"start": v(-45.07, 35.1) * mm, "end": v(-45.06, 34.97) * mm});
            skLineSegment(sketch, "E1473", {"start": v(-45.06, 34.97) * mm, "end": v(-45.09, 34.68) * mm});
            skLineSegment(sketch, "E1474", {"start": v(-45.09, 34.68) * mm, "end": v(-45.09, 34.67) * mm});
            skLineSegment(sketch, "E1475", {"start": v(-45.09, 34.67) * mm, "end": v(-45.09, 34.67) * mm});
            skLineSegment(sketch, "E1476", {"start": v(-45.09, 34.67) * mm, "end": v(-45.1, 34.48) * mm});
            skLineSegment(sketch, "E1477", {"start": v(-45.1, 34.48) * mm, "end": v(-45.25, 34) * mm});
            skLineSegment(sketch, "E1478", {"start": v(-45.25, 34) * mm, "end": v(-45.48, 33.57) * mm});
            skLineSegment(sketch, "E1479", {"start": v(-45.48, 33.57) * mm, "end": v(-45.48, 33.57) * mm});
            skLineSegment(sketch, "E1480", {"start": v(-45.48, 33.57) * mm, "end": v(-45.8, 33.19) * mm});
            skLineSegment(sketch, "E1481", {"start": v(-45.8, 33.19) * mm, "end": v(-46.18, 32.87) * mm});
            skLineSegment(sketch, "E1482", {"start": v(-46.18, 32.87) * mm, "end": v(-46.61, 32.64) * mm});
            skLineSegment(sketch, "E1483", {"start": v(-46.61, 32.64) * mm, "end": v(-47.09, 32.5) * mm});
            skLineSegment(sketch, "E1484", {"start": v(-47.09, 32.5) * mm, "end": v(-47.58, 32.45) * mm});
            skLineSegment(sketch, "E1485", {"start": v(-47.58, 32.45) * mm, "end": v(-47.8, 32.47) * mm});
            skLineSegment(sketch, "E1486", {"start": v(-47.8, 32.47) * mm, "end": v(-47.81, 32.47) * mm});
            skLineSegment(sketch, "E1487", {"start": v(-47.81, 32.47) * mm, "end": v(-47.85, 32.48) * mm});
            skLineSegment(sketch, "E1488", {"start": v(-47.85, 32.48) * mm, "end": v(-48.07, 32.5) * mm});
            skLineSegment(sketch, "E1489", {"start": v(-48.07, 32.5) * mm, "end": v(-48.17, 32.53) * mm});
            skLineSegment(sketch, "E1490", {"start": v(-48.17, 32.53) * mm, "end": v(-48.3, 32.55) * mm});
            skLineSegment(sketch, "E1491", {"start": v(-48.3, 32.55) * mm, "end": v(-48.76, 32.72) * mm});
            skLineSegment(sketch, "E1492", {"start": v(-48.76, 32.72) * mm, "end": v(-48.9, 32.81) * mm});
            skLineSegment(sketch, "E1493", {"start": v(-48.9, 32.81) * mm, "end": v(-49.06, 32.88) * mm});
            skLineSegment(sketch, "E1494", {"start": v(-49.06, 32.88) * mm, "end": v(-49.3, 33.05) * mm});
            skLineSegment(sketch, "E1495", {"start": v(-49.3, 33.05) * mm, "end": v(-49.62, 33.12) * mm});
            skLineSegment(sketch, "E1496", {"start": v(-49.62, 33.12) * mm, "end": v(-49.8, 33.14) * mm});
            skLineSegment(sketch, "E1497", {"start": v(-49.8, 33.14) * mm, "end": v(-49.8, 33.14) * mm});
            skLineSegment(sketch, "E1498", {"start": v(-49.8, 33.14) * mm, "end": v(-49.82, 33.14) * mm});
            skLineSegment(sketch, "E1499", {"start": v(-49.82, 33.14) * mm, "end": v(-50.3, 33.12) * mm});
            skLineSegment(sketch, "E1500", {"start": v(-50.3, 33.12) * mm, "end": v(-50.77, 33) * mm});
            skLineSegment(sketch, "E1501", {"start": v(-50.77, 33) * mm, "end": v(-51.22, 32.8) * mm});
            skLineSegment(sketch, "E1502", {"start": v(-51.22, 32.8) * mm, "end": v(-51.62, 32.5) * mm});
            skLineSegment(sketch, "E1503", {"start": v(-51.62, 32.5) * mm, "end": v(-51.95, 32.13) * mm});
            skLineSegment(sketch, "E1504", {"start": v(-51.95, 32.13) * mm, "end": v(-52.2, 31.7) * mm});
            skLineSegment(sketch, "E1505", {"start": v(-52.2, 31.7) * mm, "end": v(-52.2, 31.7) * mm});
            skLineSegment(sketch, "E1506", {"start": v(-52.2, 31.7) * mm, "end": v(-52.34, 31.3) * mm});
            skLineSegment(sketch, "E1507", {"start": v(-52.34, 31.3) * mm, "end": v(-52.37, 31.2) * mm});
            skLineSegment(sketch, "E1508", {"start": v(-52.37, 31.2) * mm, "end": v(-52.41, 30.93) * mm});
            skLineSegment(sketch, "E1509", {"start": v(-52.41, 30.93) * mm, "end": v(-52.44, 30.67) * mm});
            skLineSegment(sketch, "E1510", {"start": v(-52.44, 30.67) * mm, "end": v(-52.44, 30.64) * mm});
            skLineSegment(sketch, "E1511", {"start": v(-52.44, 30.64) * mm, "end": v(-52.43, 30.55) * mm});
            skLineSegment(sketch, "E1512", {"start": v(-52.43, 30.55) * mm, "end": v(-52.38, 30.14) * mm});
            skLineSegment(sketch, "E1513", {"start": v(-52.38, 30.14) * mm, "end": v(-52.24, 29.67) * mm});
            skLineSegment(sketch, "E1514", {"start": v(-52.24, 29.67) * mm, "end": v(-52, 29.24) * mm});
            skLineSegment(sketch, "E1515", {"start": v(-52, 29.24) * mm, "end": v(-51.68, 28.86) * mm});
            skLineSegment(sketch, "E1516", {"start": v(-51.68, 28.86) * mm, "end": v(-51.48, 28.7) * mm});
            skLineSegment(sketch, "E1517", {"start": v(-51.48, 28.7) * mm, "end": v(-51.31, 28.59) * mm});
            skLineSegment(sketch, "E1518", {"start": v(-51.31, 28.59) * mm, "end": v(-51.1, 28.54) * mm});
            skLineSegment(sketch, "E1519", {"start": v(-51.1, 28.54) * mm, "end": v(-50.94, 28.48) * mm});
            skLineSegment(sketch, "E1520", {"start": v(-50.94, 28.48) * mm, "end": v(-50.75, 28.42) * mm});
            skLineSegment(sketch, "E1521", {"start": v(-50.75, 28.42) * mm, "end": v(-50.52, 28.31) * mm});
            skLineSegment(sketch, "E1522", {"start": v(-50.52, 28.31) * mm, "end": v(-50.51, 28.3) * mm});
            skLineSegment(sketch, "E1523", {"start": v(-50.51, 28.3) * mm, "end": v(-50.49, 28.3) * mm});
            skLineSegment(sketch, "E1524", {"start": v(-50.49, 28.3) * mm, "end": v(-50.3, 28.2) * mm});
            skLineSegment(sketch, "E1525", {"start": v(-50.3, 28.2) * mm, "end": v(-50.23, 28.14) * mm});
            skLineSegment(sketch, "E1526", {"start": v(-50.23, 28.14) * mm, "end": v(-50.09, 28.06) * mm});
            skLineSegment(sketch, "E1527", {"start": v(-50.09, 28.06) * mm, "end": v(-49.72, 27.73) * mm});
            skLineSegment(sketch, "E1528", {"start": v(-49.72, 27.73) * mm, "end": v(-49.42, 27.34) * mm});
            skLineSegment(sketch, "E1529", {"start": v(-49.42, 27.34) * mm, "end": v(-49.2, 26.9) * mm});
            skLineSegment(sketch, "E1530", {"start": v(-49.2, 26.9) * mm, "end": v(-49.07, 26.42) * mm});
            skLineSegment(sketch, "E1531", {"start": v(-49.07, 26.42) * mm, "end": v(-49.04, 25.93) * mm});
            skLineSegment(sketch, "E1532", {"start": v(-49.04, 25.93) * mm, "end": v(-49.07, 25.75) * mm});
            skLineSegment(sketch, "E1533", {"start": v(-49.07, 25.75) * mm, "end": v(-49.07, 25.73) * mm});
            skLineSegment(sketch, "E1534", {"start": v(-49.07, 25.73) * mm, "end": v(-49.07, 25.7) * mm});
            skLineSegment(sketch, "E1535", {"start": v(-49.07, 25.7) * mm, "end": v(-49.11, 25.44) * mm});
            skLineSegment(sketch, "E1536", {"start": v(-49.11, 25.44) * mm, "end": v(-49.11, 25.44) * mm});
            skLineSegment(sketch, "E1537", {"start": v(-49.11, 25.44) * mm, "end": v(-49.15, 25.31) * mm});
            skLineSegment(sketch, "E1538", {"start": v(-49.15, 25.31) * mm, "end": v(-49.17, 25.25) * mm});
            skLineSegment(sketch, "E1539", {"start": v(-49.17, 25.25) * mm, "end": v(-49.17, 25.25) * mm});
            skLineSegment(sketch, "E1540", {"start": v(-49.17, 25.25) * mm, "end": v(-49.22, 25.12) * mm});
            skLineSegment(sketch, "E1541", {"start": v(-49.22, 25.12) * mm, "end": v(-49.27, 24.97) * mm});
            skLineSegment(sketch, "E1542", {"start": v(-49.27, 24.97) * mm, "end": v(-49.31, 24.9) * mm});
            skLineSegment(sketch, "E1543", {"start": v(-49.31, 24.9) * mm, "end": v(-49.36, 24.8) * mm});
            skLineSegment(sketch, "E1544", {"start": v(-49.36, 24.8) * mm, "end": v(-49.5, 24.59) * mm});
            skLineSegment(sketch, "E1545", {"start": v(-49.5, 24.59) * mm, "end": v(-49.52, 24.54) * mm});
            skLineSegment(sketch, "E1546", {"start": v(-49.52, 24.54) * mm, "end": v(-49.54, 24.52) * mm});
            skLineSegment(sketch, "E1547", {"start": v(-49.54, 24.52) * mm, "end": v(-49.63, 24.38) * mm});
            skLineSegment(sketch, "E1548", {"start": v(-49.63, 24.38) * mm, "end": v(-49.98, 24.04) * mm});
            skLineSegment(sketch, "E1549", {"start": v(-49.98, 24.04) * mm, "end": v(-50.4, 23.76) * mm});
            skLineSegment(sketch, "E1550", {"start": v(-50.4, 23.76) * mm, "end": v(-50.85, 23.57) * mm});
            skLineSegment(sketch, "E1551", {"start": v(-50.85, 23.57) * mm, "end": v(-51.33, 23.48) * mm});
            skLineSegment(sketch, "E1552", {"start": v(-51.33, 23.48) * mm, "end": v(-51.53, 23.48) * mm});
            skLineSegment(sketch, "E1553", {"start": v(-51.53, 23.48) * mm, "end": v(-51.6, 23.47) * mm});
            skLineSegment(sketch, "E1554", {"start": v(-51.6, 23.47) * mm, "end": v(-51.76, 23.48) * mm});
            skLineSegment(sketch, "E1555", {"start": v(-51.76, 23.48) * mm, "end": v(-51.83, 23.48) * mm});
            skLineSegment(sketch, "E1556", {"start": v(-51.83, 23.48) * mm, "end": v(-51.86, 23.49) * mm});
            skLineSegment(sketch, "E1557", {"start": v(-51.86, 23.49) * mm, "end": v(-52.1, 23.5) * mm});
            skLineSegment(sketch, "E1558", {"start": v(-52.1, 23.5) * mm, "end": v(-52.3, 23.56) * mm});
            skLineSegment(sketch, "E1559", {"start": v(-52.3, 23.56) * mm, "end": v(-52.46, 23.58) * mm});
            skLineSegment(sketch, "E1560", {"start": v(-52.46, 23.58) * mm, "end": v(-52.65, 23.64) * mm});
            skLineSegment(sketch, "E1561", {"start": v(-52.65, 23.64) * mm, "end": v(-52.84, 23.63) * mm});
            skLineSegment(sketch, "E1562", {"start": v(-52.84, 23.63) * mm, "end": v(-53.1, 23.6) * mm});
            skLineSegment(sketch, "E1563", {"start": v(-53.1, 23.6) * mm, "end": v(-53.56, 23.43) * mm});
            skLineSegment(sketch, "E1564", {"start": v(-53.56, 23.43) * mm, "end": v(-53.98, 23.18) * mm});
            skLineSegment(sketch, "E1565", {"start": v(-53.98, 23.18) * mm, "end": v(-54.35, 22.85) * mm});
            skLineSegment(sketch, "E1566", {"start": v(-54.35, 22.85) * mm, "end": v(-54.58, 22.54) * mm});
            skLineSegment(sketch, "E1567", {"start": v(-54.58, 22.54) * mm, "end": v(-54.67, 22.4) * mm});
            skLineSegment(sketch, "E1568", {"start": v(-54.67, 22.4) * mm, "end": v(-54.76, 22.2) * mm});
            skLineSegment(sketch, "E1569", {"start": v(-54.76, 22.2) * mm, "end": v(-54.89, 21.9) * mm});
            skLineSegment(sketch, "E1570", {"start": v(-54.89, 21.9) * mm, "end": v(-54.9, 21.86) * mm});
            skLineSegment(sketch, "E1571", {"start": v(-54.9, 21.86) * mm, "end": v(-54.98, 21.4) * mm});
            skLineSegment(sketch, "E1572", {"start": v(-54.98, 21.4) * mm, "end": v(-54.98, 21.4) * mm});
            skLineSegment(sketch, "E1573", {"start": v(-54.98, 21.4) * mm, "end": v(-54.98, 20.9) * mm});
            skLineSegment(sketch, "E1574", {"start": v(-54.98, 20.9) * mm, "end": v(-54.88, 20.43) * mm});
            skLineSegment(sketch, "E1575", {"start": v(-54.88, 20.43) * mm, "end": v(-54.69, 19.97) * mm});
            skLineSegment(sketch, "E1576", {"start": v(-54.69, 19.97) * mm, "end": v(-54.4, 19.56) * mm});
            skLineSegment(sketch, "E1577", {"start": v(-54.4, 19.56) * mm, "end": v(-54.06, 19.22) * mm});
            skLineSegment(sketch, "E1578", {"start": v(-54.06, 19.22) * mm, "end": v(-53.68, 18.97) * mm});
            skLineSegment(sketch, "E1579", {"start": v(-53.68, 18.97) * mm, "end": v(-53.62, 18.94) * mm});
            skLineSegment(sketch, "E1580", {"start": v(-53.62, 18.94) * mm, "end": v(-53.51, 18.9) * mm});
            skLineSegment(sketch, "E1581", {"start": v(-53.51, 18.9) * mm, "end": v(-53.4, 18.86) * mm});
            skLineSegment(sketch, "E1582", {"start": v(-53.4, 18.86) * mm, "end": v(-53.24, 18.8) * mm});
            skLineSegment(sketch, "E1583", {"start": v(-53.24, 18.8) * mm, "end": v(-53.18, 18.81) * mm});
            skLineSegment(sketch, "E1584", {"start": v(-53.18, 18.81) * mm, "end": v(-53.06, 18.8) * mm});
            skLineSegment(sketch, "E1585", {"start": v(-53.06, 18.8) * mm, "end": v(-52.86, 18.81) * mm});
            skLineSegment(sketch, "E1586", {"start": v(-52.86, 18.81) * mm, "end": v(-52.74, 18.82) * mm});
            skLineSegment(sketch, "E1587", {"start": v(-52.74, 18.82) * mm, "end": v(-52.67, 18.8) * mm});
            skLineSegment(sketch, "E1588", {"start": v(-52.67, 18.8) * mm, "end": v(-52.6, 18.8) * mm});
            skLineSegment(sketch, "E1589", {"start": v(-52.6, 18.8) * mm, "end": v(-52.1, 18.72) * mm});
            skLineSegment(sketch, "E1590", {"start": v(-52.1, 18.72) * mm, "end": v(-51.98, 18.68) * mm});
            skLineSegment(sketch, "E1591", {"start": v(-51.98, 18.68) * mm, "end": v(-51.85, 18.64) * mm});
            skLineSegment(sketch, "E1592", {"start": v(-51.85, 18.64) * mm, "end": v(-51.4, 18.43) * mm});
            skLineSegment(sketch, "E1593", {"start": v(-51.4, 18.43) * mm, "end": v(-51, 18.14) * mm});
            skLineSegment(sketch, "E1594", {"start": v(-51, 18.14) * mm, "end": v(-50.67, 17.78) * mm});
            skLineSegment(sketch, "E1595", {"start": v(-50.67, 17.78) * mm, "end": v(-50.4, 17.35) * mm});
            skLineSegment(sketch, "E1596", {"start": v(-50.4, 17.35) * mm, "end": v(-50.24, 16.9) * mm});
            skLineSegment(sketch, "E1597", {"start": v(-50.24, 16.9) * mm, "end": v(-50.17, 16.4) * mm});
            skLineSegment(sketch, "E1598", {"start": v(-50.17, 16.4) * mm, "end": v(-50.17, 16.4) * mm});
            skLineSegment(sketch, "E1599", {"start": v(-50.17, 16.4) * mm, "end": v(-50.19, 15.9) * mm});
            skLineSegment(sketch, "E1600", {"start": v(-50.19, 15.9) * mm, "end": v(-50.22, 15.76) * mm});
            skLineSegment(sketch, "E1601", {"start": v(-50.22, 15.76) * mm, "end": v(-50.23, 15.7) * mm});
            skLineSegment(sketch, "E1602", {"start": v(-50.23, 15.7) * mm, "end": v(-50.26, 15.6) * mm});
            skLineSegment(sketch, "E1603", {"start": v(-50.26, 15.6) * mm, "end": v(-50.3, 15.43) * mm});
            skLineSegment(sketch, "E1604", {"start": v(-50.3, 15.43) * mm, "end": v(-50.34, 15.35) * mm});
            skLineSegment(sketch, "E1605", {"start": v(-50.34, 15.35) * mm, "end": v(-50.38, 15.24) * mm});
            skLineSegment(sketch, "E1606", {"start": v(-50.38, 15.24) * mm, "end": v(-50.49, 15.04) * mm});
            skLineSegment(sketch, "E1607", {"start": v(-50.49, 15.04) * mm, "end": v(-50.51, 14.98) * mm});
            skLineSegment(sketch, "E1608", {"start": v(-50.51, 14.98) * mm, "end": v(-50.53, 14.96) * mm});
            skLineSegment(sketch, "E1609", {"start": v(-50.53, 14.96) * mm, "end": v(-50.61, 14.8) * mm});
            skLineSegment(sketch, "E1610", {"start": v(-50.61, 14.8) * mm, "end": v(-50.93, 14.43) * mm});
            skLineSegment(sketch, "E1611", {"start": v(-50.93, 14.43) * mm, "end": v(-51.32, 14.12) * mm});
            skLineSegment(sketch, "E1612", {"start": v(-51.32, 14.12) * mm, "end": v(-51.75, 13.89) * mm});
            skLineSegment(sketch, "E1613", {"start": v(-51.75, 13.89) * mm, "end": v(-51.98, 13.82) * mm});
            skLineSegment(sketch, "E1614", {"start": v(-51.98, 13.82) * mm, "end": v(-52.03, 13.8) * mm});
            skLineSegment(sketch, "E1615", {"start": v(-52.03, 13.8) * mm, "end": v(-52.15, 13.77) * mm});
            skLineSegment(sketch, "E1616", {"start": v(-52.15, 13.77) * mm, "end": v(-52.23, 13.75) * mm});
            skLineSegment(sketch, "E1617", {"start": v(-52.23, 13.75) * mm, "end": v(-52.27, 13.75) * mm});
            skLineSegment(sketch, "E1618", {"start": v(-52.27, 13.75) * mm, "end": v(-52.52, 13.7) * mm});
            skLineSegment(sketch, "E1619", {"start": v(-52.52, 13.7) * mm, "end": v(-52.75, 13.69) * mm});
            skLineSegment(sketch, "E1620", {"start": v(-52.75, 13.69) * mm, "end": v(-52.91, 13.66) * mm});
            skLineSegment(sketch, "E1621", {"start": v(-52.91, 13.66) * mm, "end": v(-53.08, 13.67) * mm});
            skLineSegment(sketch, "E1622", {"start": v(-53.08, 13.67) * mm, "end": v(-53.43, 13.52) * mm});
            skLineSegment(sketch, "E1623", {"start": v(-53.43, 13.52) * mm, "end": v(-53.66, 13.37) * mm});
            skLineSegment(sketch, "E1624", {"start": v(-53.66, 13.37) * mm, "end": v(-53.9, 13.18) * mm});
            skLineSegment(sketch, "E1625", {"start": v(-53.9, 13.18) * mm, "end": v(-54.23, 12.81) * mm});
            skLineSegment(sketch, "E1626", {"start": v(-54.23, 12.81) * mm, "end": v(-54.48, 12.39) * mm});
            skLineSegment(sketch, "E1627", {"start": v(-54.48, 12.39) * mm, "end": v(-54.64, 11.92) * mm});
            skLineSegment(sketch, "E1628", {"start": v(-54.64, 11.92) * mm, "end": v(-54.7, 11.43) * mm});
            skLineSegment(sketch, "E1629", {"start": v(-54.7, 11.43) * mm, "end": v(-54.67, 10.94) * mm});
            skLineSegment(sketch, "E1630", {"start": v(-54.67, 10.94) * mm, "end": v(-54.67, 10.94) * mm});
            skLineSegment(sketch, "E1631", {"start": v(-54.67, 10.94) * mm, "end": v(-54.54, 10.46) * mm});
            skLineSegment(sketch, "E1632", {"start": v(-54.54, 10.46) * mm, "end": v(-54.33, 10.02) * mm});
            skLineSegment(sketch, "E1633", {"start": v(-54.33, 10.02) * mm, "end": v(-54.03, 9.63) * mm});
            skLineSegment(sketch, "E1634", {"start": v(-54.03, 9.63) * mm, "end": v(-53.66, 9.3) * mm});
            skLineSegment(sketch, "E1635", {"start": v(-53.66, 9.3) * mm, "end": v(-53.34, 9.11) * mm});
            skLineSegment(sketch, "E1636", {"start": v(-53.34, 9.11) * mm, "end": v(-53.17, 9.03) * mm});
            skLineSegment(sketch, "E1637", {"start": v(-53.17, 9.03) * mm, "end": v(-53.05, 9) * mm});
            skLineSegment(sketch, "E1638", {"start": v(-53.05, 9) * mm, "end": v(-52.65, 8.88) * mm});
            skLineSegment(sketch, "E1639", {"start": v(-52.65, 8.88) * mm, "end": v(-52.27, 8.86) * mm});
            skLineSegment(sketch, "E1640", {"start": v(-52.27, 8.86) * mm, "end": v(-52.22, 8.88) * mm});
            skLineSegment(sketch, "E1641", {"start": v(-52.22, 8.88) * mm, "end": v(-52.1, 8.9) * mm});
            skLineSegment(sketch, "E1642", {"start": v(-52.1, 8.9) * mm, "end": v(-51.91, 8.97) * mm});
            skLineSegment(sketch, "E1643", {"start": v(-51.91, 8.97) * mm, "end": v(-51.87, 8.98) * mm});
            skLineSegment(sketch, "E1644", {"start": v(-51.87, 8.98) * mm, "end": v(-51.72, 9) * mm});
            skLineSegment(sketch, "E1645", {"start": v(-51.72, 9) * mm, "end": v(-51.6, 9.04) * mm});
            skLineSegment(sketch, "E1646", {"start": v(-51.6, 9.04) * mm, "end": v(-51.1, 9.08) * mm});
            skLineSegment(sketch, "E1647", {"start": v(-51.1, 9.08) * mm, "end": v(-50.95, 9.06) * mm});
            skLineSegment(sketch, "E1648", {"start": v(-50.95, 9.06) * mm, "end": v(-50.84, 9.06) * mm});
            skLineSegment(sketch, "E1649", {"start": v(-50.84, 9.06) * mm, "end": v(-50.64, 9.02) * mm});
            skLineSegment(sketch, "E1650", {"start": v(-50.64, 9.02) * mm, "end": v(-50.61, 9.02) * mm});
            skLineSegment(sketch, "E1651", {"start": v(-50.61, 9.02) * mm, "end": v(-50.6, 9.01) * mm});
            skLineSegment(sketch, "E1652", {"start": v(-50.6, 9.01) * mm, "end": v(-50.36, 8.97) * mm});
            skLineSegment(sketch, "E1653", {"start": v(-50.36, 8.97) * mm, "end": v(-49.9, 8.78) * mm});
            skLineSegment(sketch, "E1654", {"start": v(-49.9, 8.78) * mm, "end": v(-49.48, 8.51) * mm});
            skLineSegment(sketch, "E1655", {"start": v(-49.48, 8.51) * mm, "end": v(-49.13, 8.17) * mm});
            skLineSegment(sketch, "E1656", {"start": v(-49.13, 8.17) * mm, "end": v(-48.85, 7.76) * mm});
            skLineSegment(sketch, "E1657", {"start": v(-48.85, 7.76) * mm, "end": v(-48.66, 7.3) * mm});
            skLineSegment(sketch, "E1658", {"start": v(-48.66, 7.3) * mm, "end": v(-48.66, 7.3) * mm});
            skLineSegment(sketch, "E1659", {"start": v(-48.66, 7.3) * mm, "end": v(-48.56, 6.82) * mm});
            skLineSegment(sketch, "E1660", {"start": v(-48.56, 6.82) * mm, "end": v(-48.55, 6.33) * mm});
            skLineSegment(sketch, "E1661", {"start": v(-48.55, 6.33) * mm, "end": v(-48.65, 5.84) * mm});
            skLineSegment(sketch, "E1662", {"start": v(-48.65, 5.84) * mm, "end": v(-48.83, 5.39) * mm});
            skLineSegment(sketch, "E1663", {"start": v(-48.83, 5.39) * mm, "end": v(-48.92, 5.25) * mm});
            skLineSegment(sketch, "E1664", {"start": v(-48.92, 5.25) * mm, "end": v(-48.95, 5.2) * mm});
            skLineSegment(sketch, "E1665", {"start": v(-48.95, 5.2) * mm, "end": v(-49.03, 5.09) * mm});
            skLineSegment(sketch, "E1666", {"start": v(-49.03, 5.09) * mm, "end": v(-49.1, 4.97) * mm});
            skLineSegment(sketch, "E1667", {"start": v(-49.1, 4.97) * mm, "end": v(-49.15, 4.92) * mm});
            skLineSegment(sketch, "E1668", {"start": v(-49.15, 4.92) * mm, "end": v(-49.25, 4.8) * mm});
            skLineSegment(sketch, "E1669", {"start": v(-49.25, 4.8) * mm, "end": v(-49.62, 4.47) * mm});
            skLineSegment(sketch, "E1670", {"start": v(-49.62, 4.47) * mm, "end": v(-50.04, 4.22) * mm});
            skLineSegment(sketch, "E1671", {"start": v(-50.04, 4.22) * mm, "end": v(-50.17, 4.18) * mm});
            skLineSegment(sketch, "E1672", {"start": v(-50.17, 4.18) * mm, "end": v(-50.35, 4.08) * mm});
            skLineSegment(sketch, "E1673", {"start": v(-50.35, 4.08) * mm, "end": v(-50.68, 4) * mm});
            skLineSegment(sketch, "E1674", {"start": v(-50.68, 4) * mm, "end": v(-50.75, 3.96) * mm});
            skLineSegment(sketch, "E1675", {"start": v(-50.75, 3.96) * mm, "end": v(-50.79, 3.95) * mm});
            skLineSegment(sketch, "E1676", {"start": v(-50.79, 3.95) * mm, "end": v(-50.82, 3.93) * mm});
            skLineSegment(sketch, "E1677", {"start": v(-50.82, 3.93) * mm, "end": v(-51.1, 3.72) * mm});
            skLineSegment(sketch, "E1678", {"start": v(-51.1, 3.72) * mm, "end": v(-51.36, 3.4) * mm});
            skLineSegment(sketch, "E1679", {"start": v(-51.36, 3.4) * mm, "end": v(-51.43, 3.32) * mm});
            skLineSegment(sketch, "E1680", {"start": v(-51.43, 3.32) * mm, "end": v(-51.53, 3.14) * mm});
            skLineSegment(sketch, "E1681", {"start": v(-51.53, 3.14) * mm, "end": v(-51.68, 2.83) * mm});
            skLineSegment(sketch, "E1682", {"start": v(-51.68, 2.83) * mm, "end": v(-51.82, 2.36) * mm});
            skLineSegment(sketch, "E1683", {"start": v(-51.82, 2.36) * mm, "end": v(-51.85, 1.87) * mm});
            skLineSegment(sketch, "E1684", {"start": v(-51.85, 1.87) * mm, "end": v(-51.8, 1.38) * mm});
            skLineSegment(sketch, "E1685", {"start": v(-51.8, 1.38) * mm, "end": v(-51.64, 0.9) * mm});
            skLineSegment(sketch, "E1686", {"start": v(-51.64, 0.9) * mm, "end": v(-51.64, 0.9) * mm});
            skLineSegment(sketch, "E1687", {"start": v(-51.64, 0.9) * mm, "end": v(-51.4, 0.48) * mm});
            skLineSegment(sketch, "E1688", {"start": v(-51.4, 0.48) * mm, "end": v(-51.07, 0.1) * mm});
            skLineSegment(sketch, "E1689", {"start": v(-51.07, 0.1) * mm, "end": v(-50.68, -0.2) * mm});
            skLineSegment(sketch, "E1690", {"start": v(-50.68, -0.2) * mm, "end": v(-50.57, -0.25) * mm});
            skLineSegment(sketch, "E1691", {"start": v(-50.57, -0.25) * mm, "end": v(-50.27, -0.4) * mm});
            skLineSegment(sketch, "E1692", {"start": v(-50.27, -0.4) * mm, "end": v(-50.23, -0.42) * mm});
            skLineSegment(sketch, "E1693", {"start": v(-50.23, -0.42) * mm, "end": v(-50.07, -0.47) * mm});
            skLineSegment(sketch, "E1694", {"start": v(-50.07, -0.47) * mm, "end": v(-49.96, -0.5) * mm});
            skLineSegment(sketch, "E1695", {"start": v(-49.96, -0.5) * mm, "end": v(-49.69, -0.56) * mm});
            skLineSegment(sketch, "E1696", {"start": v(-49.69, -0.56) * mm, "end": v(-49.65, -0.56) * mm});
            skLineSegment(sketch, "E1697", {"start": v(-49.65, -0.56) * mm, "end": v(-49.64, -0.56) * mm});
            skLineSegment(sketch, "E1698", {"start": v(-49.64, -0.56) * mm, "end": v(-49.18, -0.57) * mm});
            skLineSegment(sketch, "E1699", {"start": v(-49.18, -0.57) * mm, "end": v(-48.87, -0.51) * mm});
            skLineSegment(sketch, "E1700", {"start": v(-48.87, -0.51) * mm, "end": v(-48.84, -0.5) * mm});
            skLineSegment(sketch, "E1701", {"start": v(-48.84, -0.5) * mm, "end": v(-48.74, -0.46) * mm});
            skLineSegment(sketch, "E1702", {"start": v(-48.74, -0.46) * mm, "end": v(-48.51, -0.3) * mm});
            skLineSegment(sketch, "E1703", {"start": v(-48.51, -0.3) * mm, "end": v(-48.35, -0.24) * mm});
            skLineSegment(sketch, "E1704", {"start": v(-48.35, -0.24) * mm, "end": v(-48.22, -0.17) * mm});
            skLineSegment(sketch, "E1705", {"start": v(-48.22, -0.17) * mm, "end": v(-48.02, -0.1) * mm});
            skLineSegment(sketch, "E1706", {"start": v(-48.02, -0.1) * mm, "end": v(-48, -0.09) * mm});
            skLineSegment(sketch, "E1707", {"start": v(-48, -0.09) * mm, "end": v(-47.96, -0.08) * mm});
            skLineSegment(sketch, "E1708", {"start": v(-47.96, -0.08) * mm, "end": v(-47.76, 0) * mm});
            skLineSegment(sketch, "E1709", {"start": v(-47.76, 0) * mm, "end": v(-47.67, 0) * mm});
            skLineSegment(sketch, "E1710", {"start": v(-47.67, 0) * mm, "end": v(-47.53, 0.04) * mm});
            skLineSegment(sketch, "E1711", {"start": v(-47.53, 0.04) * mm, "end": v(-47.03, 0.08) * mm});
            skLineSegment(sketch, "E1712", {"start": v(-47.03, 0.08) * mm, "end": v(-46.54, 0.03) * mm});
            skLineSegment(sketch, "E1713", {"start": v(-46.54, 0.03) * mm, "end": v(-46.07, -0.13) * mm});
            skLineSegment(sketch, "E1714", {"start": v(-46.07, -0.13) * mm, "end": v(-45.64, -0.37) * mm});
            skLineSegment(sketch, "E1715", {"start": v(-45.64, -0.37) * mm, "end": v(-45.54, -0.46) * mm});
            skLineSegment(sketch, "E1716", {"start": v(-45.54, -0.46) * mm, "end": v(-45.51, -0.48) * mm});
            skLineSegment(sketch, "E1717", {"start": v(-45.51, -0.48) * mm, "end": v(-45.45, -0.53) * mm});
            skLineSegment(sketch, "E1718", {"start": v(-45.45, -0.53) * mm, "end": v(-45.27, -0.69) * mm});
            skLineSegment(sketch, "E1719", {"start": v(-45.27, -0.69) * mm, "end": v(-45.21, -0.76) * mm});
            skLineSegment(sketch, "E1720", {"start": v(-45.21, -0.76) * mm, "end": v(-45.15, -0.82) * mm});
            skLineSegment(sketch, "E1721", {"start": v(-45.15, -0.82) * mm, "end": v(-45.04, -0.98) * mm});
            skLineSegment(sketch, "E1722", {"start": v(-45.04, -0.98) * mm, "end": v(-44.96, -1.08) * mm});
            skLineSegment(sketch, "E1723", {"start": v(-44.96, -1.08) * mm, "end": v(-44.96, -1.08) * mm});
            skLineSegment(sketch, "E1724", {"start": v(-44.96, -1.08) * mm, "end": v(-44.94, -1.12) * mm});
            skLineSegment(sketch, "E1725", {"start": v(-44.94, -1.12) * mm, "end": v(-44.87, -1.22) * mm});
            skLineSegment(sketch, "E1726", {"start": v(-44.87, -1.22) * mm, "end": v(-44.87, -1.22) * mm});
            skLineSegment(sketch, "E1727", {"start": v(-44.87, -1.22) * mm, "end": v(-44.83, -1.32) * mm});
            skLineSegment(sketch, "E1728", {"start": v(-44.83, -1.32) * mm, "end": v(-44.75, -1.5) * mm});
            skLineSegment(sketch, "E1729", {"start": v(-44.75, -1.5) * mm, "end": v(-44.74, -1.52) * mm});
            skLineSegment(sketch, "E1730", {"start": v(-44.74, -1.52) * mm, "end": v(-44.74, -1.53) * mm});
            skLineSegment(sketch, "E1731", {"start": v(-44.74, -1.53) * mm, "end": v(-44.67, -1.67) * mm});
            skLineSegment(sketch, "E1732", {"start": v(-44.67, -1.67) * mm, "end": v(-44.56, -2.15) * mm});
            skLineSegment(sketch, "E1733", {"start": v(-44.56, -2.15) * mm, "end": v(-44.55, -2.65) * mm});
            skLineSegment(sketch, "E1734", {"start": v(-44.55, -2.65) * mm, "end": v(-44.64, -3.13) * mm});
            skLineSegment(sketch, "E1735", {"start": v(-44.64, -3.13) * mm, "end": v(-44.82, -3.6) * mm});
            skLineSegment(sketch, "E1736", {"start": v(-44.82, -3.6) * mm, "end": v(-45.08, -4.01) * mm});
            skLineSegment(sketch, "E1737", {"start": v(-45.08, -4.01) * mm, "end": v(-45.16, -4.1) * mm});
            skLineSegment(sketch, "E1738", {"start": v(-45.16, -4.1) * mm, "end": v(-45.22, -4.18) * mm});
            skLineSegment(sketch, "E1739", {"start": v(-45.22, -4.18) * mm, "end": v(-45.42, -4.37) * mm});
            skLineSegment(sketch, "E1740", {"start": v(-45.42, -4.37) * mm, "end": v(-45.42, -4.37) * mm});
            skLineSegment(sketch, "E1741", {"start": v(-45.42, -4.37) * mm, "end": v(-45.58, -4.52) * mm});
            skLineSegment(sketch, "E1742", {"start": v(-45.58, -4.52) * mm, "end": v(-45.7, -4.59) * mm});
            skLineSegment(sketch, "E1743", {"start": v(-45.7, -4.59) * mm, "end": v(-45.82, -4.7) * mm});
            skLineSegment(sketch, "E1744", {"start": v(-45.82, -4.7) * mm, "end": v(-46.04, -4.82) * mm});
            skLineSegment(sketch, "E1745", {"start": v(-46.04, -4.82) * mm, "end": v(-46.13, -4.89) * mm});
            skLineSegment(sketch, "E1746", {"start": v(-46.13, -4.89) * mm, "end": v(-46.23, -4.93) * mm});
            skLineSegment(sketch, "E1747", {"start": v(-46.23, -4.93) * mm, "end": v(-46.29, -5) * mm});
            skLineSegment(sketch, "E1748", {"start": v(-46.29, -5) * mm, "end": v(-46.45, -5.18) * mm});
            skLineSegment(sketch, "E1749", {"start": v(-46.45, -5.18) * mm, "end": v(-46.68, -5.62) * mm});
            skLineSegment(sketch, "E1750", {"start": v(-46.68, -5.62) * mm, "end": v(-46.82, -6.1) * mm});
            skLineSegment(sketch, "E1751", {"start": v(-46.82, -6.1) * mm, "end": v(-46.83, -6.14) * mm});
            skLineSegment(sketch, "E1752", {"start": v(-46.83, -6.14) * mm, "end": v(-46.86, -6.48) * mm});
            skLineSegment(sketch, "E1753", {"start": v(-46.86, -6.48) * mm, "end": v(-46.87, -6.62) * mm});
            skLineSegment(sketch, "E1754", {"start": v(-46.87, -6.62) * mm, "end": v(-46.85, -6.84) * mm});
            skLineSegment(sketch, "E1755", {"start": v(-46.85, -6.84) * mm, "end": v(-46.8, -7.11) * mm});
            skLineSegment(sketch, "E1756", {"start": v(-46.8, -7.11) * mm, "end": v(-46.8, -7.16) * mm});
            skLineSegment(sketch, "E1757", {"start": v(-46.8, -7.16) * mm, "end": v(-46.79, -7.2) * mm});
            skLineSegment(sketch, "E1758", {"start": v(-46.79, -7.2) * mm, "end": v(-46.63, -7.64) * mm});
            skLineSegment(sketch, "E1759", {"start": v(-46.63, -7.64) * mm, "end": v(-46.37, -8.06) * mm});
            skLineSegment(sketch, "E1760", {"start": v(-46.37, -8.06) * mm, "end": v(-46.37, -8.06) * mm});
            skLineSegment(sketch, "E1761", {"start": v(-46.37, -8.06) * mm, "end": v(-46.04, -8.43) * mm});
            skLineSegment(sketch, "E1762", {"start": v(-46.04, -8.43) * mm, "end": v(-45.64, -8.72) * mm});
            skLineSegment(sketch, "E1763", {"start": v(-45.64, -8.72) * mm, "end": v(-45.2, -8.93) * mm});
            skLineSegment(sketch, "E1764", {"start": v(-45.2, -8.93) * mm, "end": v(-44.72, -9.04) * mm});
            skLineSegment(sketch, "E1765", {"start": v(-44.72, -9.04) * mm, "end": v(-44.22, -9.07) * mm});
            skLineSegment(sketch, "E1766", {"start": v(-44.22, -9.07) * mm, "end": v(-43.89, -9.01) * mm});
            skLineSegment(sketch, "E1767", {"start": v(-43.89, -9.01) * mm, "end": v(-43.83, -9) * mm});
            skLineSegment(sketch, "E1768", {"start": v(-43.83, -9) * mm, "end": v(-43.68, -8.97) * mm});
            skLineSegment(sketch, "E1769", {"start": v(-43.68, -8.97) * mm, "end": v(-43.66, -8.96) * mm});
            skLineSegment(sketch, "E1770", {"start": v(-43.66, -8.96) * mm, "end": v(-43.58, -8.93) * mm});
            skLineSegment(sketch, "E1771", {"start": v(-43.58, -8.93) * mm, "end": v(-43.47, -8.85) * mm});
            skLineSegment(sketch, "E1772", {"start": v(-43.47, -8.85) * mm, "end": v(-43.32, -8.71) * mm});
            skLineSegment(sketch, "E1773", {"start": v(-43.32, -8.71) * mm, "end": v(-43.12, -8.59) * mm});
            skLineSegment(sketch, "E1774", {"start": v(-43.12, -8.59) * mm, "end": v(-43, -8.49) * mm});
            skLineSegment(sketch, "E1775", {"start": v(-43, -8.49) * mm, "end": v(-43, -8.48) * mm});
            skLineSegment(sketch, "E1776", {"start": v(-43, -8.48) * mm, "end": v(-42.8, -8.37) * mm});
            skLineSegment(sketch, "E1777", {"start": v(-42.8, -8.37) * mm, "end": v(-42.74, -8.33) * mm});
            skLineSegment(sketch, "E1778", {"start": v(-42.74, -8.33) * mm, "end": v(-42.59, -8.26) * mm});
            skLineSegment(sketch, "E1779", {"start": v(-42.59, -8.26) * mm, "end": v(-42.57, -8.25) * mm});
            skLineSegment(sketch, "E1780", {"start": v(-42.57, -8.25) * mm, "end": v(-42.56, -8.24) * mm});
            skLineSegment(sketch, "E1781", {"start": v(-42.56, -8.24) * mm, "end": v(-42.3, -8.12) * mm});
            skLineSegment(sketch, "E1782", {"start": v(-42.3, -8.12) * mm, "end": v(-42.11, -8.07) * mm});
            skLineSegment(sketch, "E1783", {"start": v(-42.11, -8.07) * mm, "end": v(-42.09, -8.06) * mm});
            skLineSegment(sketch, "E1784", {"start": v(-42.09, -8.06) * mm, "end": v(-42.02, -8.05) * mm});
            skLineSegment(sketch, "E1785", {"start": v(-42.02, -8.05) * mm, "end": v(-41.81, -8) * mm});
            skLineSegment(sketch, "E1786", {"start": v(-41.81, -8) * mm, "end": v(-41.72, -8) * mm});
            skLineSegment(sketch, "E1787", {"start": v(-41.72, -8) * mm, "end": v(-41.6, -7.97) * mm});
            skLineSegment(sketch, "E1788", {"start": v(-41.6, -7.97) * mm, "end": v(-41.32, -7.97) * mm});
            skLineSegment(sketch, "E1789", {"start": v(-41.32, -7.97) * mm, "end": v(-41.32, -7.97) * mm});
            skLineSegment(sketch, "E1790", {"start": v(-41.32, -7.97) * mm, "end": v(-41.1, -7.98) * mm});
            skLineSegment(sketch, "E1791", {"start": v(-41.1, -7.98) * mm, "end": v(-40.63, -8.08) * mm});
            skLineSegment(sketch, "E1792", {"start": v(-40.63, -8.08) * mm, "end": v(-40.17, -8.27) * mm});
            skLineSegment(sketch, "E1793", {"start": v(-40.17, -8.27) * mm, "end": v(-39.77, -8.55) * mm});
            skLineSegment(sketch, "E1794", {"start": v(-39.77, -8.55) * mm, "end": v(-39.42, -8.9) * mm});
            skLineSegment(sketch, "E1795", {"start": v(-39.42, -8.9) * mm, "end": v(-39.42, -8.9) * mm});
            skLineSegment(sketch, "E1796", {"start": v(-39.42, -8.9) * mm, "end": v(-39.15, -9.32) * mm});
            skLineSegment(sketch, "E1797", {"start": v(-39.15, -9.32) * mm, "end": v(-38.97, -9.78) * mm});
            skLineSegment(sketch, "E1798", {"start": v(-38.97, -9.78) * mm, "end": v(-38.88, -10.26) * mm});
            skLineSegment(sketch, "E1799", {"start": v(-38.88, -10.26) * mm, "end": v(-38.88, -10.75) * mm});
            skLineSegment(sketch, "E1800", {"start": v(-38.88, -10.75) * mm, "end": v(-38.91, -10.88) * mm});
            skLineSegment(sketch, "E1801", {"start": v(-38.91, -10.88) * mm, "end": v(-38.92, -10.95) * mm});
            skLineSegment(sketch, "E1802", {"start": v(-38.92, -10.95) * mm, "end": v(-38.96, -11.1) * mm});
            skLineSegment(sketch, "E1803", {"start": v(-38.96, -11.1) * mm, "end": v(-38.99, -11.23) * mm});
            skLineSegment(sketch, "E1804", {"start": v(-38.99, -11.23) * mm, "end": v(-39, -11.29) * mm});
            skLineSegment(sketch, "E1805", {"start": v(-39, -11.29) * mm, "end": v(-39.05, -11.42) * mm});
            skLineSegment(sketch, "E1806", {"start": v(-39.05, -11.42) * mm, "end": v(-39.27, -11.86) * mm});
            skLineSegment(sketch, "E1807", {"start": v(-39.27, -11.86) * mm, "end": v(-39.4, -12.04) * mm});
            skLineSegment(sketch, "E1808", {"start": v(-39.4, -12.04) * mm, "end": v(-39.42, -12.06) * mm});
            skLineSegment(sketch, "E1809", {"start": v(-39.42, -12.06) * mm, "end": v(-39.44, -12.09) * mm});
            skLineSegment(sketch, "E1810", {"start": v(-39.44, -12.09) * mm, "end": v(-39.48, -12.13) * mm});
            skLineSegment(sketch, "E1811", {"start": v(-39.48, -12.13) * mm, "end": v(-39.57, -12.25) * mm});
            skLineSegment(sketch, "E1812", {"start": v(-39.57, -12.25) * mm, "end": v(-39.62, -12.3) * mm});
            skLineSegment(sketch, "E1813", {"start": v(-39.62, -12.3) * mm, "end": v(-39.76, -12.46) * mm});
            skLineSegment(sketch, "E1814", {"start": v(-39.76, -12.46) * mm, "end": v(-39.9, -12.57) * mm});
            skLineSegment(sketch, "E1815", {"start": v(-39.9, -12.57) * mm, "end": v(-40.03, -12.7) * mm});
            skLineSegment(sketch, "E1816", {"start": v(-40.03, -12.7) * mm, "end": v(-40.25, -12.85) * mm});
            skLineSegment(sketch, "E1817", {"start": v(-40.25, -12.85) * mm, "end": v(-40.39, -12.98) * mm});
            skLineSegment(sketch, "E1818", {"start": v(-40.39, -12.98) * mm, "end": v(-40.51, -13.05) * mm});
            skLineSegment(sketch, "E1819", {"start": v(-40.51, -13.05) * mm, "end": v(-40.66, -13.31) * mm});
            skLineSegment(sketch, "E1820", {"start": v(-40.66, -13.31) * mm, "end": v(-40.74, -13.5) * mm});
            skLineSegment(sketch, "E1821", {"start": v(-40.74, -13.5) * mm, "end": v(-40.77, -13.58) * mm});
            skLineSegment(sketch, "E1822", {"start": v(-40.77, -13.58) * mm, "end": v(-40.87, -14) * mm});
            skLineSegment(sketch, "E1823", {"start": v(-40.87, -14) * mm, "end": v(-40.9, -14.5) * mm});
            skLineSegment(sketch, "E1824", {"start": v(-40.9, -14.5) * mm, "end": v(-40.82, -14.98) * mm});
            skLineSegment(sketch, "E1825", {"start": v(-40.82, -14.98) * mm, "end": v(-40.66, -15.44) * mm});
            skLineSegment(sketch, "E1826", {"start": v(-40.66, -15.44) * mm, "end": v(-40.4, -15.86) * mm});
            skLineSegment(sketch, "E1827", {"start": v(-40.4, -15.86) * mm, "end": v(-40.4, -15.86) * mm});
            skLineSegment(sketch, "E1828", {"start": v(-40.4, -15.86) * mm, "end": v(-40.07, -16.23) * mm});
            skLineSegment(sketch, "E1829", {"start": v(-40.07, -16.23) * mm, "end": v(-39.67, -16.52) * mm});
            skLineSegment(sketch, "E1830", {"start": v(-39.67, -16.52) * mm, "end": v(-39.23, -16.73) * mm});
            skLineSegment(sketch, "E1831", {"start": v(-39.23, -16.73) * mm, "end": v(-38.79, -16.84) * mm});
            skLineSegment(sketch, "E1832", {"start": v(-38.79, -16.84) * mm, "end": v(-38.73, -16.85) * mm});
            skLineSegment(sketch, "E1833", {"start": v(-38.73, -16.85) * mm, "end": v(-38.5, -16.86) * mm});
            skLineSegment(sketch, "E1834", {"start": v(-38.5, -16.86) * mm, "end": v(-38.46, -16.86) * mm});
            skLineSegment(sketch, "E1835", {"start": v(-38.46, -16.86) * mm, "end": v(-38.39, -16.86) * mm});
            skLineSegment(sketch, "E1836", {"start": v(-38.39, -16.86) * mm, "end": v(-38.17, -16.86) * mm});
            skLineSegment(sketch, "E1837", {"start": v(-38.17, -16.86) * mm, "end": v(-38.15, -16.86) * mm});
            skLineSegment(sketch, "E1838", {"start": v(-38.15, -16.86) * mm, "end": v(-38.13, -16.85) * mm});
            skLineSegment(sketch, "E1839", {"start": v(-38.13, -16.85) * mm, "end": v(-38.02, -16.83) * mm});
            skLineSegment(sketch, "E1840", {"start": v(-38.02, -16.83) * mm, "end": v(-37.97, -16.79) * mm});
            skLineSegment(sketch, "E1841", {"start": v(-37.97, -16.79) * mm, "end": v(-37.62, -16.58) * mm});
            skLineSegment(sketch, "E1842", {"start": v(-37.62, -16.58) * mm, "end": v(-37.53, -16.51) * mm});
            skLineSegment(sketch, "E1843", {"start": v(-37.53, -16.51) * mm, "end": v(-37.26, -16.38) * mm});
            skLineSegment(sketch, "E1844", {"start": v(-37.26, -16.38) * mm, "end": v(-37.15, -16.3) * mm});
            skLineSegment(sketch, "E1845", {"start": v(-37.15, -16.3) * mm, "end": v(-36.92, -16.2) * mm});
            skLineSegment(sketch, "E1846", {"start": v(-36.92, -16.2) * mm, "end": v(-36.84, -16.16) * mm});
            skLineSegment(sketch, "E1847", {"start": v(-36.84, -16.16) * mm, "end": v(-36.67, -16.1) * mm});
            skLineSegment(sketch, "E1848", {"start": v(-36.67, -16.1) * mm, "end": v(-36.65, -16.09) * mm});
            skLineSegment(sketch, "E1849", {"start": v(-36.65, -16.09) * mm, "end": v(-36.57, -16.06) * mm});
            skLineSegment(sketch, "E1850", {"start": v(-36.57, -16.06) * mm, "end": v(-36.37, -16) * mm});
            skLineSegment(sketch, "E1851", {"start": v(-36.37, -16) * mm, "end": v(-36.3, -15.98) * mm});
            skLineSegment(sketch, "E1852", {"start": v(-36.3, -15.98) * mm, "end": v(-36.18, -15.94) * mm});
            skLineSegment(sketch, "E1853", {"start": v(-36.18, -15.94) * mm, "end": v(-35.7, -15.9) * mm});
            skLineSegment(sketch, "E1854", {"start": v(-35.7, -15.9) * mm, "end": v(-35.59, -15.9) * mm});
            skLineSegment(sketch, "E1855", {"start": v(-35.59, -15.9) * mm, "end": v(-35.54, -15.9) * mm});
            skLineSegment(sketch, "E1856", {"start": v(-35.54, -15.9) * mm, "end": v(-35.4, -15.92) * mm});
            skLineSegment(sketch, "E1857", {"start": v(-35.4, -15.92) * mm, "end": v(-35.2, -15.94) * mm});
            skLineSegment(sketch, "E1858", {"start": v(-35.2, -15.94) * mm, "end": v(-35.14, -15.96) * mm});
            skLineSegment(sketch, "E1859", {"start": v(-35.14, -15.96) * mm, "end": v(-35.06, -15.97) * mm});
            skLineSegment(sketch, "E1860", {"start": v(-35.06, -15.97) * mm, "end": v(-34.78, -16.07) * mm});
            skLineSegment(sketch, "E1861", {"start": v(-34.78, -16.07) * mm, "end": v(-34.73, -16.08) * mm});
            skLineSegment(sketch, "E1862", {"start": v(-34.73, -16.08) * mm, "end": v(-34.72, -16.1) * mm});
            skLineSegment(sketch, "E1863", {"start": v(-34.72, -16.1) * mm, "end": v(-34.6, -16.14) * mm});
            skLineSegment(sketch, "E1864", {"start": v(-34.6, -16.14) * mm, "end": v(-34.17, -16.39) * mm});
            skLineSegment(sketch, "E1865", {"start": v(-34.17, -16.39) * mm, "end": v(-33.8, -16.72) * mm});
            skLineSegment(sketch, "E1866", {"start": v(-33.8, -16.72) * mm, "end": v(-33.5, -17.1) * mm});
            skLineSegment(sketch, "E1867", {"start": v(-33.5, -17.1) * mm, "end": v(-33.5, -17.1) * mm});
            skLineSegment(sketch, "E1868", {"start": v(-33.5, -17.1) * mm, "end": v(-33.3, -17.55) * mm});
            skLineSegment(sketch, "E1869", {"start": v(-33.3, -17.55) * mm, "end": v(-33.17, -18.03) * mm});
            skLineSegment(sketch, "E1870", {"start": v(-33.17, -18.03) * mm, "end": v(-33.15, -18.52) * mm});
            skLineSegment(sketch, "E1871", {"start": v(-33.15, -18.52) * mm, "end": v(-33.17, -18.65) * mm});
            skLineSegment(sketch, "E1872", {"start": v(-33.17, -18.65) * mm, "end": v(-33.17, -18.67) * mm});
            skLineSegment(sketch, "E1873", {"start": v(-33.17, -18.67) * mm, "end": v(-33.18, -18.73) * mm});
            skLineSegment(sketch, "E1874", {"start": v(-33.18, -18.73) * mm, "end": v(-33.22, -19) * mm});
            skLineSegment(sketch, "E1875", {"start": v(-33.22, -19) * mm, "end": v(-33.25, -19.09) * mm});
            skLineSegment(sketch, "E1876", {"start": v(-33.25, -19.09) * mm, "end": v(-33.26, -19.15) * mm});
            skLineSegment(sketch, "E1877", {"start": v(-33.26, -19.15) * mm, "end": v(-33.34, -19.34) * mm});
            skLineSegment(sketch, "E1878", {"start": v(-33.34, -19.34) * mm, "end": v(-33.38, -19.47) * mm});
            skLineSegment(sketch, "E1879", {"start": v(-33.38, -19.47) * mm, "end": v(-33.4, -19.5) * mm});
            skLineSegment(sketch, "E1880", {"start": v(-33.4, -19.5) * mm, "end": v(-33.44, -19.6) * mm});
            skLineSegment(sketch, "E1881", {"start": v(-33.44, -19.6) * mm, "end": v(-33.71, -20.02) * mm});
            skLineSegment(sketch, "E1882", {"start": v(-33.71, -20.02) * mm, "end": v(-33.8, -20.11) * mm});
            skLineSegment(sketch, "E1883", {"start": v(-33.8, -20.11) * mm, "end": v(-33.85, -20.17) * mm});
            skLineSegment(sketch, "E1884", {"start": v(-33.85, -20.17) * mm, "end": v(-34, -20.32) * mm});
            skLineSegment(sketch, "E1885", {"start": v(-34, -20.32) * mm, "end": v(-34.03, -20.34) * mm});
            skLineSegment(sketch, "E1886", {"start": v(-34.03, -20.34) * mm, "end": v(-34.03, -20.34) * mm});
            skLineSegment(sketch, "E1887", {"start": v(-34.03, -20.34) * mm, "end": v(-34.06, -20.37) * mm});
            skLineSegment(sketch, "E1888", {"start": v(-34.06, -20.37) * mm, "end": v(-34.08, -20.38) * mm});
            skLineSegment(sketch, "E1889", {"start": v(-34.08, -20.38) * mm, "end": v(-34.2, -20.5) * mm});
            skLineSegment(sketch, "E1890", {"start": v(-34.2, -20.5) * mm, "end": v(-34.26, -20.53) * mm});
            skLineSegment(sketch, "E1891", {"start": v(-34.26, -20.53) * mm, "end": v(-34.4, -20.65) * mm});
            skLineSegment(sketch, "E1892", {"start": v(-34.4, -20.65) * mm, "end": v(-34.5, -20.7) * mm});
            skLineSegment(sketch, "E1893", {"start": v(-34.5, -20.7) * mm, "end": v(-34.74, -20.89) * mm});
            skLineSegment(sketch, "E1894", {"start": v(-34.74, -20.89) * mm, "end": v(-34.81, -20.92) * mm});
            skLineSegment(sketch, "E1895", {"start": v(-34.81, -20.92) * mm, "end": v(-35.17, -21.16) * mm});
            skLineSegment(sketch, "E1896", {"start": v(-35.17, -21.16) * mm, "end": v(-35.23, -21.18) * mm});
            skLineSegment(sketch, "E1897", {"start": v(-35.23, -21.18) * mm, "end": v(-35.26, -21.2) * mm});
            skLineSegment(sketch, "E1898", {"start": v(-35.26, -21.2) * mm, "end": v(-35.32, -21.24) * mm});
            skLineSegment(sketch, "E1899", {"start": v(-35.32, -21.24) * mm, "end": v(-35.43, -21.39) * mm});
            skLineSegment(sketch, "E1900", {"start": v(-35.43, -21.39) * mm, "end": v(-35.65, -21.83) * mm});
            skLineSegment(sketch, "E1901", {"start": v(-35.65, -21.83) * mm, "end": v(-35.77, -22.25) * mm});
            skLineSegment(sketch, "E1902", {"start": v(-35.77, -22.25) * mm, "end": v(-35.78, -22.32) * mm});
            skLineSegment(sketch, "E1903", {"start": v(-35.78, -22.32) * mm, "end": v(-35.8, -22.63) * mm});
            skLineSegment(sketch, "E1904", {"start": v(-35.8, -22.63) * mm, "end": v(-35.8, -22.86) * mm});
            skLineSegment(sketch, "E1905", {"start": v(-35.8, -22.86) * mm, "end": v(-35.8, -22.94) * mm});
            skLineSegment(sketch, "E1906", {"start": v(-35.8, -22.94) * mm, "end": v(-35.78, -23.01) * mm});
            skLineSegment(sketch, "E1907", {"start": v(-35.78, -23.01) * mm, "end": v(-35.71, -23.4) * mm});
            skLineSegment(sketch, "E1908", {"start": v(-35.71, -23.4) * mm, "end": v(-35.53, -23.85) * mm});
            skLineSegment(sketch, "E1909", {"start": v(-35.53, -23.85) * mm, "end": v(-35.53, -23.85) * mm});
            skLineSegment(sketch, "E1910", {"start": v(-35.53, -23.85) * mm, "end": v(-35.26, -24.26) * mm});
            skLineSegment(sketch, "E1911", {"start": v(-35.26, -24.26) * mm, "end": v(-34.91, -24.61) * mm});
            skLineSegment(sketch, "E1912", {"start": v(-34.91, -24.61) * mm, "end": v(-34.5, -24.89) * mm});
            skLineSegment(sketch, "E1913", {"start": v(-34.5, -24.89) * mm, "end": v(-34.05, -25.08) * mm});
            skLineSegment(sketch, "E1914", {"start": v(-34.05, -25.08) * mm, "end": v(-33.57, -25.18) * mm});
            skLineSegment(sketch, "E1915", {"start": v(-33.57, -25.18) * mm, "end": v(-33.15, -25.18) * mm});
            skLineSegment(sketch, "E1916", {"start": v(-33.15, -25.18) * mm, "end": v(-33.05, -25.18) * mm});
            skLineSegment(sketch, "E1917", {"start": v(-33.05, -25.18) * mm, "end": v(-33, -25.17) * mm});
            skLineSegment(sketch, "E1918", {"start": v(-33, -25.17) * mm, "end": v(-32.89, -25.12) * mm});
            skLineSegment(sketch, "E1919", {"start": v(-32.89, -25.12) * mm, "end": v(-32.63, -24.97) * mm});
            skLineSegment(sketch, "E1920", {"start": v(-32.63, -24.97) * mm, "end": v(-32.48, -24.92) * mm});
            skLineSegment(sketch, "E1921", {"start": v(-32.48, -24.92) * mm, "end": v(-32.28, -24.81) * mm});
            skLineSegment(sketch, "E1922", {"start": v(-32.28, -24.81) * mm, "end": v(-32.1, -24.76) * mm});
            skLineSegment(sketch, "E1923", {"start": v(-32.1, -24.76) * mm, "end": v(-32, -24.71) * mm});
            skLineSegment(sketch, "E1924", {"start": v(-32, -24.71) * mm, "end": v(-31.52, -24.6) * mm});
            skLineSegment(sketch, "E1925", {"start": v(-31.52, -24.6) * mm, "end": v(-31.38, -24.6) * mm});
            skLineSegment(sketch, "E1926", {"start": v(-31.38, -24.6) * mm, "end": v(-31.3, -24.59) * mm});
            skLineSegment(sketch, "E1927", {"start": v(-31.3, -24.59) * mm, "end": v(-31.1, -24.6) * mm});
            skLineSegment(sketch, "E1928", {"start": v(-31.1, -24.6) * mm, "end": v(-31.02, -24.6) * mm});
            skLineSegment(sketch, "E1929", {"start": v(-31.02, -24.6) * mm, "end": v(-30.99, -24.6) * mm});
            skLineSegment(sketch, "E1930", {"start": v(-30.99, -24.6) * mm, "end": v(-30.8, -24.6) * mm});
            skLineSegment(sketch, "E1931", {"start": v(-30.8, -24.6) * mm, "end": v(-30.33, -24.72) * mm});
            skLineSegment(sketch, "E1932", {"start": v(-30.33, -24.72) * mm, "end": v(-29.88, -24.92) * mm});
            skLineSegment(sketch, "E1933", {"start": v(-29.88, -24.92) * mm, "end": v(-29.48, -25.2) * mm});
            skLineSegment(sketch, "E1934", {"start": v(-29.48, -25.2) * mm, "end": v(-29.14, -25.57) * mm});
            skLineSegment(sketch, "E1935", {"start": v(-29.14, -25.57) * mm, "end": v(-28.88, -25.98) * mm});
            skLineSegment(sketch, "E1936", {"start": v(-28.88, -25.98) * mm, "end": v(-28.88, -25.98) * mm});
            skLineSegment(sketch, "E1937", {"start": v(-28.88, -25.98) * mm, "end": v(-28.7, -26.45) * mm});
            skLineSegment(sketch, "E1938", {"start": v(-28.7, -26.45) * mm, "end": v(-28.63, -26.93) * mm});
            skLineSegment(sketch, "E1939", {"start": v(-28.63, -26.93) * mm, "end": v(-28.64, -27.42) * mm});
            skLineSegment(sketch, "E1940", {"start": v(-28.64, -27.42) * mm, "end": v(-28.67, -27.56) * mm});
            skLineSegment(sketch, "E1941", {"start": v(-28.67, -27.56) * mm, "end": v(-28.68, -27.6) * mm});
            skLineSegment(sketch, "E1942", {"start": v(-28.68, -27.6) * mm, "end": v(-28.7, -27.71) * mm});
            skLineSegment(sketch, "E1943", {"start": v(-28.7, -27.71) * mm, "end": v(-28.75, -27.9) * mm});
            skLineSegment(sketch, "E1944", {"start": v(-28.75, -27.9) * mm, "end": v(-28.79, -27.98) * mm});
            skLineSegment(sketch, "E1945", {"start": v(-28.79, -27.98) * mm, "end": v(-28.82, -28.08) * mm});
            skLineSegment(sketch, "E1946", {"start": v(-28.82, -28.08) * mm, "end": v(-28.9, -28.25) * mm});
            skLineSegment(sketch, "E1947", {"start": v(-28.9, -28.25) * mm, "end": v(-28.93, -28.3) * mm});
            skLineSegment(sketch, "E1948", {"start": v(-28.93, -28.3) * mm, "end": v(-28.96, -28.35) * mm});
            skLineSegment(sketch, "E1949", {"start": v(-28.96, -28.35) * mm, "end": v(-28.96, -28.36) * mm});
            skLineSegment(sketch, "E1950", {"start": v(-28.96, -28.36) * mm, "end": v(-28.97, -28.38) * mm});
            skLineSegment(sketch, "E1951", {"start": v(-28.97, -28.38) * mm, "end": v(-29.05, -28.52) * mm});
            skLineSegment(sketch, "E1952", {"start": v(-29.05, -28.52) * mm, "end": v(-29.36, -28.9) * mm});
            skLineSegment(sketch, "E1953", {"start": v(-29.36, -28.9) * mm, "end": v(-29.54, -29.05) * mm});
            skLineSegment(sketch, "E1954", {"start": v(-29.54, -29.05) * mm, "end": v(-29.56, -29.08) * mm});
            skLineSegment(sketch, "E1955", {"start": v(-29.56, -29.08) * mm, "end": v(-29.63, -29.13) * mm});
            skLineSegment(sketch, "E1956", {"start": v(-29.63, -29.13) * mm, "end": v(-29.74, -29.22) * mm});
            skLineSegment(sketch, "E1957", {"start": v(-29.74, -29.22) * mm, "end": v(-29.79, -29.25) * mm});
            skLineSegment(sketch, "E1958", {"start": v(-29.79, -29.25) * mm, "end": v(-29.96, -29.37) * mm});
            skLineSegment(sketch, "E1959", {"start": v(-29.96, -29.37) * mm, "end": v(-30.1, -29.44) * mm});
            skLineSegment(sketch, "E1960", {"start": v(-30.1, -29.44) * mm, "end": v(-30.28, -29.56) * mm});
            skLineSegment(sketch, "E1961", {"start": v(-30.28, -29.56) * mm, "end": v(-30.49, -29.64) * mm});
            skLineSegment(sketch, "E1962", {"start": v(-30.49, -29.64) * mm, "end": v(-30.66, -29.74) * mm});
            skLineSegment(sketch, "E1963", {"start": v(-30.66, -29.74) * mm, "end": v(-30.78, -29.84) * mm});
            skLineSegment(sketch, "E1964", {"start": v(-30.78, -29.84) * mm, "end": v(-31.01, -30.15) * mm});
            skLineSegment(sketch, "E1965", {"start": v(-31.01, -30.15) * mm, "end": v(-31.05, -30.2) * mm});
            skLineSegment(sketch, "E1966", {"start": v(-31.05, -30.2) * mm, "end": v(-31.1, -30.28) * mm});
            skLineSegment(sketch, "E1967", {"start": v(-31.1, -30.28) * mm, "end": v(-31.17, -30.43) * mm});
            skLineSegment(sketch, "E1968", {"start": v(-31.17, -30.43) * mm, "end": v(-31.3, -30.77) * mm});
            skLineSegment(sketch, "E1969", {"start": v(-31.3, -30.77) * mm, "end": v(-31.4, -31.26) * mm});
            skLineSegment(sketch, "E1970", {"start": v(-31.4, -31.26) * mm, "end": v(-31.4, -31.75) * mm});
            skLineSegment(sketch, "E1971", {"start": v(-31.4, -31.75) * mm, "end": v(-31.3, -32.23) * mm});
            skLineSegment(sketch, "E1972", {"start": v(-31.3, -32.23) * mm, "end": v(-31.12, -32.69) * mm});
            skLineSegment(sketch, "E1973", {"start": v(-31.12, -32.69) * mm, "end": v(-31.12, -32.69) * mm});
            skLineSegment(sketch, "E1974", {"start": v(-31.12, -32.69) * mm, "end": v(-30.85, -33.1) * mm});
            skLineSegment(sketch, "E1975", {"start": v(-30.85, -33.1) * mm, "end": v(-30.5, -33.45) * mm});
            skLineSegment(sketch, "E1976", {"start": v(-30.5, -33.45) * mm, "end": v(-30.09, -33.72) * mm});
            skLineSegment(sketch, "E1977", {"start": v(-30.09, -33.72) * mm, "end": v(-29.63, -33.91) * mm});
            skLineSegment(sketch, "E1978", {"start": v(-29.63, -33.91) * mm, "end": v(-29.23, -34) * mm});
            skLineSegment(sketch, "E1979", {"start": v(-29.23, -34) * mm, "end": v(-29.14, -34) * mm});
            skLineSegment(sketch, "E1980", {"start": v(-29.14, -34) * mm, "end": v(-29.11, -34) * mm});
            skLineSegment(sketch, "E1981", {"start": v(-29.11, -34) * mm, "end": v(-29.04, -34) * mm});
            skLineSegment(sketch, "E1982", {"start": v(-29.04, -34) * mm, "end": v(-28.92, -34) * mm});
            skLineSegment(sketch, "E1983", {"start": v(-28.92, -34) * mm, "end": v(-28.57, -33.99) * mm});
            skLineSegment(sketch, "E1984", {"start": v(-28.57, -33.99) * mm, "end": v(-28.2, -33.9) * mm});
            skLineSegment(sketch, "E1985", {"start": v(-28.2, -33.9) * mm, "end": v(-27.93, -33.7) * mm});
            skLineSegment(sketch, "E1986", {"start": v(-27.93, -33.7) * mm, "end": v(-27.81, -33.65) * mm});
            skLineSegment(sketch, "E1987", {"start": v(-27.81, -33.65) * mm, "end": v(-27.66, -33.55) * mm});
            skLineSegment(sketch, "E1988", {"start": v(-27.66, -33.55) * mm, "end": v(-27.5, -33.48) * mm});
            skLineSegment(sketch, "E1989", {"start": v(-27.5, -33.48) * mm, "end": v(-27.44, -33.45) * mm});
            skLineSegment(sketch, "E1990", {"start": v(-27.44, -33.45) * mm, "end": v(-27.3, -33.4) * mm});
            skLineSegment(sketch, "E1991", {"start": v(-27.3, -33.4) * mm, "end": v(-27.27, -33.4) * mm});
            skLineSegment(sketch, "E1992", {"start": v(-27.27, -33.4) * mm, "end": v(-27.2, -33.36) * mm});
            skLineSegment(sketch, "E1993", {"start": v(-27.2, -33.36) * mm, "end": v(-27.17, -33.36) * mm});
            skLineSegment(sketch, "E1994", {"start": v(-27.17, -33.36) * mm, "end": v(-26.98, -33.3) * mm});
            skLineSegment(sketch, "E1995", {"start": v(-26.98, -33.3) * mm, "end": v(-26.49, -33.23) * mm});
            skLineSegment(sketch, "E1996", {"start": v(-26.49, -33.23) * mm, "end": v(-26.32, -33.24) * mm});
            skLineSegment(sketch, "E1997", {"start": v(-26.32, -33.24) * mm, "end": v(-26.32, -33.24) * mm});
            skLineSegment(sketch, "E1998", {"start": v(-26.32, -33.24) * mm, "end": v(-26, -33.26) * mm});
            skLineSegment(sketch, "E1999", {"start": v(-26, -33.26) * mm, "end": v(-25.88, -33.3) * mm});
            skLineSegment(sketch, "E2000", {"start": v(-25.88, -33.3) * mm, "end": v(-25.83, -33.3) * mm});
            skLineSegment(sketch, "E2001", {"start": v(-25.83, -33.3) * mm, "end": v(-25.72, -33.33) * mm});
            skLineSegment(sketch, "E2002", {"start": v(-25.72, -33.33) * mm, "end": v(-25.52, -33.39) * mm});
            skLineSegment(sketch, "E2003", {"start": v(-25.52, -33.39) * mm, "end": v(-25.45, -33.42) * mm});
            skLineSegment(sketch, "E2004", {"start": v(-25.45, -33.42) * mm, "end": v(-25.36, -33.45) * mm});
            skLineSegment(sketch, "E2005", {"start": v(-25.36, -33.45) * mm, "end": v(-25.15, -33.57) * mm});
            skLineSegment(sketch, "E2006", {"start": v(-25.15, -33.57) * mm, "end": v(-25.08, -33.6) * mm});
            skLineSegment(sketch, "E2007", {"start": v(-25.08, -33.6) * mm, "end": v(-25.05, -33.63) * mm});
            skLineSegment(sketch, "E2008", {"start": v(-25.05, -33.63) * mm, "end": v(-24.93, -33.7) * mm});
            skLineSegment(sketch, "E2009", {"start": v(-24.93, -33.7) * mm, "end": v(-24.56, -34.01) * mm});
            skLineSegment(sketch, "E2010", {"start": v(-24.56, -34.01) * mm, "end": v(-24.25, -34.4) * mm});
            skLineSegment(sketch, "E2011", {"start": v(-24.25, -34.4) * mm, "end": v(-24.25, -34.4) * mm});
            skLineSegment(sketch, "E2012", {"start": v(-24.25, -34.4) * mm, "end": v(-24.03, -34.84) * mm});
            skLineSegment(sketch, "E2013", {"start": v(-24.03, -34.84) * mm, "end": v(-23.9, -35.32) * mm});
            skLineSegment(sketch, "E2014", {"start": v(-23.9, -35.32) * mm, "end": v(-23.86, -35.8) * mm});
            skLineSegment(sketch, "E2015", {"start": v(-23.86, -35.8) * mm, "end": v(-23.92, -36.3) * mm});
            skLineSegment(sketch, "E2016", {"start": v(-23.92, -36.3) * mm, "end": v(-24.07, -36.77) * mm});
            skLineSegment(sketch, "E2017", {"start": v(-24.07, -36.77) * mm, "end": v(-24.16, -36.92) * mm});
            skLineSegment(sketch, "E2018", {"start": v(-24.16, -36.92) * mm, "end": v(-24.17, -36.95) * mm});
            skLineSegment(sketch, "E2019", {"start": v(-24.17, -36.95) * mm, "end": v(-24.2, -37) * mm});
            skLineSegment(sketch, "E2020", {"start": v(-24.2, -37) * mm, "end": v(-24.31, -37.2) * mm});
            skLineSegment(sketch, "E2021", {"start": v(-24.31, -37.2) * mm, "end": v(-24.35, -37.24) * mm});
            skLineSegment(sketch, "E2022", {"start": v(-24.35, -37.24) * mm, "end": v(-24.37, -37.26) * mm});
            skLineSegment(sketch, "E2023", {"start": v(-24.37, -37.26) * mm, "end": v(-24.43, -37.36) * mm});
            skLineSegment(sketch, "E2024", {"start": v(-24.43, -37.36) * mm, "end": v(-24.77, -37.72) * mm});
            skLineSegment(sketch, "E2025", {"start": v(-24.77, -37.72) * mm, "end": v(-24.88, -37.8) * mm});
            skLineSegment(sketch, "E2026", {"start": v(-24.88, -37.8) * mm, "end": v(-25, -37.9) * mm});
            skLineSegment(sketch, "E2027", {"start": v(-25, -37.9) * mm, "end": v(-25.07, -37.95) * mm});
            skLineSegment(sketch, "E2028", {"start": v(-25.07, -37.95) * mm, "end": v(-25.21, -38.04) * mm});
            skLineSegment(sketch, "E2029", {"start": v(-25.21, -38.04) * mm, "end": v(-25.3, -38.12) * mm});
            skLineSegment(sketch, "E2030", {"start": v(-25.3, -38.12) * mm, "end": v(-25.35, -38.14) * mm});
            skLineSegment(sketch, "E2031", {"start": v(-25.35, -38.14) * mm, "end": v(-25.46, -38.28) * mm});
            skLineSegment(sketch, "E2032", {"start": v(-25.46, -38.28) * mm, "end": v(-25.6, -38.5) * mm});
            skLineSegment(sketch, "E2033", {"start": v(-25.6, -38.5) * mm, "end": v(-25.8, -38.96) * mm});
            skLineSegment(sketch, "E2034", {"start": v(-25.8, -38.96) * mm, "end": v(-25.9, -39.44) * mm});
            skLineSegment(sketch, "E2035", {"start": v(-25.9, -39.44) * mm, "end": v(-25.91, -39.93) * mm});
            skLineSegment(sketch, "E2036", {"start": v(-25.91, -39.93) * mm, "end": v(-25.82, -40.42) * mm});
            skLineSegment(sketch, "E2037", {"start": v(-25.82, -40.42) * mm, "end": v(-25.67, -40.8) * mm});
            skLineSegment(sketch, "E2038", {"start": v(-25.67, -40.8) * mm, "end": v(-25.61, -40.91) * mm});
            skLineSegment(sketch, "E2039", {"start": v(-25.61, -40.91) * mm, "end": v(-25.49, -41.1) * mm});
            skLineSegment(sketch, "E2040", {"start": v(-25.49, -41.1) * mm, "end": v(-25.47, -41.14) * mm});
            skLineSegment(sketch, "E2041", {"start": v(-25.47, -41.14) * mm, "end": v(-25.32, -41.33) * mm});
            skLineSegment(sketch, "E2042", {"start": v(-25.32, -41.33) * mm, "end": v(-25.3, -41.36) * mm});
            skLineSegment(sketch, "E2043", {"start": v(-25.3, -41.36) * mm, "end": v(-25.25, -41.4) * mm});
            skLineSegment(sketch, "E2044", {"start": v(-25.25, -41.4) * mm, "end": v(-25.22, -41.44) * mm});
            skLineSegment(sketch, "E2045", {"start": v(-25.22, -41.44) * mm, "end": v(-24.9, -41.72) * mm});
            skLineSegment(sketch, "E2046", {"start": v(-24.9, -41.72) * mm, "end": v(-24.48, -41.97) * mm});
            skLineSegment(sketch, "E2047", {"start": v(-24.48, -41.97) * mm, "end": v(-24.01, -42.13) * mm});
            skLineSegment(sketch, "E2048", {"start": v(-24.01, -42.13) * mm, "end": v(-23.52, -42.2) * mm});
            skLineSegment(sketch, "E2049", {"start": v(-23.52, -42.2) * mm, "end": v(-23.03, -42.17) * mm});
            skLineSegment(sketch, "E2050", {"start": v(-23.03, -42.17) * mm, "end": v(-22.55, -42.05) * mm});
            skLineSegment(sketch, "E2051", {"start": v(-22.55, -42.05) * mm, "end": v(-22.29, -41.92) * mm});
            skLineSegment(sketch, "E2052", {"start": v(-22.29, -41.92) * mm, "end": v(-22.11, -41.82) * mm});
            skLineSegment(sketch, "E2053", {"start": v(-22.11, -41.82) * mm, "end": v(-22.1, -41.8) * mm});
            skLineSegment(sketch, "E2054", {"start": v(-22.1, -41.8) * mm, "end": v(-22.03, -41.73) * mm});
            skLineSegment(sketch, "E2055", {"start": v(-22.03, -41.73) * mm, "end": v(-21.83, -41.49) * mm});
            skLineSegment(sketch, "E2056", {"start": v(-21.83, -41.49) * mm, "end": v(-21.67, -41.35) * mm});
            skLineSegment(sketch, "E2057", {"start": v(-21.67, -41.35) * mm, "end": v(-21.6, -41.28) * mm});
            skLineSegment(sketch, "E2058", {"start": v(-21.6, -41.28) * mm, "end": v(-21.2, -40.99) * mm});
            skLineSegment(sketch, "E2059", {"start": v(-21.2, -40.99) * mm, "end": v(-20.75, -40.78) * mm});
            skLineSegment(sketch, "E2060", {"start": v(-20.75, -40.78) * mm, "end": v(-20.27, -40.66) * mm});
            skLineSegment(sketch, "E2061", {"start": v(-20.27, -40.66) * mm, "end": v(-20.12, -40.65) * mm});
            skLineSegment(sketch, "E2062", {"start": v(-20.12, -40.65) * mm, "end": v(-20.06, -40.64) * mm});
            skLineSegment(sketch, "E2063", {"start": v(-20.06, -40.64) * mm, "end": v(-19.95, -40.65) * mm});
            skLineSegment(sketch, "E2064", {"start": v(-19.95, -40.65) * mm, "end": v(-19.78, -40.64) * mm});
            skLineSegment(sketch, "E2065", {"start": v(-19.78, -40.64) * mm, "end": v(-19.7, -40.65) * mm});
            skLineSegment(sketch, "E2066", {"start": v(-19.7, -40.65) * mm, "end": v(-19.57, -40.66) * mm});
            skLineSegment(sketch, "E2067", {"start": v(-19.57, -40.66) * mm, "end": v(-19.33, -40.7) * mm});
            skLineSegment(sketch, "E2068", {"start": v(-19.33, -40.7) * mm, "end": v(-19.3, -40.72) * mm});
            skLineSegment(sketch, "E2069", {"start": v(-19.3, -40.72) * mm, "end": v(-19.27, -40.72) * mm});
            skLineSegment(sketch, "E2070", {"start": v(-19.27, -40.72) * mm, "end": v(-19.09, -40.76) * mm});
            skLineSegment(sketch, "E2071", {"start": v(-19.09, -40.76) * mm, "end": v(-18.64, -40.96) * mm});
            skLineSegment(sketch, "E2072", {"start": v(-18.64, -40.96) * mm, "end": v(-18.23, -41.25) * mm});
            skLineSegment(sketch, "E2073", {"start": v(-18.23, -41.25) * mm, "end": v(-18.23, -41.25) * mm});
            skLineSegment(sketch, "E2074", {"start": v(-18.23, -41.25) * mm, "end": v(-17.9, -41.6) * mm});
            skLineSegment(sketch, "E2075", {"start": v(-17.9, -41.6) * mm, "end": v(-17.63, -42.02) * mm});
            skLineSegment(sketch, "E2076", {"start": v(-17.63, -42.02) * mm, "end": v(-17.45, -42.48) * mm});
            skLineSegment(sketch, "E2077", {"start": v(-17.45, -42.48) * mm, "end": v(-17.37, -42.97) * mm});
            skLineSegment(sketch, "E2078", {"start": v(-17.37, -42.97) * mm, "end": v(-17.38, -43.46) * mm});
            skLineSegment(sketch, "E2079", {"start": v(-17.38, -43.46) * mm, "end": v(-17.49, -43.94) * mm});
            skLineSegment(sketch, "E2080", {"start": v(-17.49, -43.94) * mm, "end": v(-17.55, -44.09) * mm});
            skLineSegment(sketch, "E2081", {"start": v(-17.55, -44.09) * mm, "end": v(-17.58, -44.2) * mm});
            skLineSegment(sketch, "E2082", {"start": v(-17.58, -44.2) * mm, "end": v(-17.68, -44.38) * mm});
            skLineSegment(sketch, "E2083", {"start": v(-17.68, -44.38) * mm, "end": v(-17.69, -44.4) * mm});
            skLineSegment(sketch, "E2084", {"start": v(-17.69, -44.4) * mm, "end": v(-17.69, -44.4) * mm});
            skLineSegment(sketch, "E2085", {"start": v(-17.69, -44.4) * mm, "end": v(-17.81, -44.63) * mm});
            skLineSegment(sketch, "E2086", {"start": v(-17.81, -44.63) * mm, "end": v(-17.94, -44.8) * mm});
            skLineSegment(sketch, "E2087", {"start": v(-17.94, -44.8) * mm, "end": v(-17.97, -44.83) * mm});
            skLineSegment(sketch, "E2088", {"start": v(-17.97, -44.83) * mm, "end": v(-18.04, -44.95) * mm});
            skLineSegment(sketch, "E2089", {"start": v(-18.04, -44.95) * mm, "end": v(-18.17, -45.09) * mm});
            skLineSegment(sketch, "E2090", {"start": v(-18.17, -45.09) * mm, "end": v(-18.21, -45.22) * mm});
            skLineSegment(sketch, "E2091", {"start": v(-18.21, -45.22) * mm, "end": v(-18.3, -45.48) * mm});
            skLineSegment(sketch, "E2092", {"start": v(-18.3, -45.48) * mm, "end": v(-18.32, -45.55) * mm});
            skLineSegment(sketch, "E2093", {"start": v(-18.32, -45.55) * mm, "end": v(-18.34, -45.7) * mm});
            skLineSegment(sketch, "E2094", {"start": v(-18.34, -45.7) * mm, "end": v(-18.34, -45.72) * mm});
            skLineSegment(sketch, "E2095", {"start": v(-18.34, -45.72) * mm, "end": v(-18.36, -46.1) * mm});
            skLineSegment(sketch, "E2096", {"start": v(-18.36, -46.1) * mm, "end": v(-18.29, -46.59) * mm});
            skLineSegment(sketch, "E2097", {"start": v(-18.29, -46.59) * mm, "end": v(-18.12, -47.05) * mm});
            skLineSegment(sketch, "E2098", {"start": v(-18.12, -47.05) * mm, "end": v(-17.87, -47.48) * mm});
            skLineSegment(sketch, "E2099", {"start": v(-17.87, -47.48) * mm, "end": v(-17.54, -47.85) * mm});
            skLineSegment(sketch, "E2100", {"start": v(-17.54, -47.85) * mm, "end": v(-17.14, -48.14) * mm});
            skLineSegment(sketch, "E2101", {"start": v(-17.14, -48.14) * mm, "end": v(-17.14, -48.14) * mm});
            skLineSegment(sketch, "E2102", {"start": v(-17.14, -48.14) * mm, "end": v(-16.7, -48.35) * mm});
            skLineSegment(sketch, "E2103", {"start": v(-16.7, -48.35) * mm, "end": v(-16.22, -48.47) * mm});
            skLineSegment(sketch, "E2104", {"start": v(-16.22, -48.47) * mm, "end": v(-15.72, -48.5) * mm});
            skLineSegment(sketch, "E2105", {"start": v(-15.72, -48.5) * mm, "end": v(-15.33, -48.44) * mm});
            skLineSegment(sketch, "E2106", {"start": v(-15.33, -48.44) * mm, "end": v(-15.19, -48.41) * mm});
            skLineSegment(sketch, "E2107", {"start": v(-15.19, -48.41) * mm, "end": v(-15, -48.34) * mm});
            skLineSegment(sketch, "E2108", {"start": v(-15, -48.34) * mm, "end": v(-14.82, -48.27) * mm});
            skLineSegment(sketch, "E2109", {"start": v(-14.82, -48.27) * mm, "end": v(-14.67, -48.2) * mm});
            skLineSegment(sketch, "E2110", {"start": v(-14.67, -48.2) * mm, "end": v(-14.26, -47.92) * mm});
            skLineSegment(sketch, "E2111", {"start": v(-14.26, -47.92) * mm, "end": v(-13.99, -47.64) * mm});
            skLineSegment(sketch, "E2112", {"start": v(-13.99, -47.64) * mm, "end": v(-13.95, -47.6) * mm});
            skLineSegment(sketch, "E2113", {"start": v(-13.95, -47.6) * mm, "end": v(-13.93, -47.54) * mm});
            skLineSegment(sketch, "E2114", {"start": v(-13.93, -47.54) * mm, "end": v(-13.88, -47.43) * mm});
            skLineSegment(sketch, "E2115", {"start": v(-13.88, -47.43) * mm, "end": v(-13.78, -47.17) * mm});
            skLineSegment(sketch, "E2116", {"start": v(-13.78, -47.17) * mm, "end": v(-13.67, -47) * mm});
            skLineSegment(sketch, "E2117", {"start": v(-13.67, -47) * mm, "end": v(-13.63, -46.9) * mm});
            skLineSegment(sketch, "E2118", {"start": v(-13.63, -46.9) * mm, "end": v(-13.35, -46.5) * mm});
            skLineSegment(sketch, "E2119", {"start": v(-13.35, -46.5) * mm, "end": v(-13, -46.16) * mm});
            skLineSegment(sketch, "E2120", {"start": v(-13, -46.16) * mm, "end": v(-12.84, -46.07) * mm});
            skLineSegment(sketch, "E2121", {"start": v(-12.84, -46.07) * mm, "end": v(-12.82, -46.05) * mm});
            skLineSegment(sketch, "E2122", {"start": v(-12.82, -46.05) * mm, "end": v(-12.77, -46.02) * mm});
            skLineSegment(sketch, "E2123", {"start": v(-12.77, -46.02) * mm, "end": v(-12.57, -45.9) * mm});
            skLineSegment(sketch, "E2124", {"start": v(-12.57, -45.9) * mm, "end": v(-12.47, -45.86) * mm});
            skLineSegment(sketch, "E2125", {"start": v(-12.47, -45.86) * mm, "end": v(-12.39, -45.82) * mm});
            skLineSegment(sketch, "E2126", {"start": v(-12.39, -45.82) * mm, "end": v(-12.2, -45.76) * mm});
            skLineSegment(sketch, "E2127", {"start": v(-12.2, -45.76) * mm, "end": v(-12.11, -45.72) * mm});
            skLineSegment(sketch, "E2128", {"start": v(-12.11, -45.72) * mm, "end": v(-12.07, -45.72) * mm});
            skLineSegment(sketch, "E2129", {"start": v(-12.07, -45.72) * mm, "end": v(-11.92, -45.67) * mm});
            skLineSegment(sketch, "E2130", {"start": v(-11.92, -45.67) * mm, "end": v(-11.42, -45.62) * mm});
            skLineSegment(sketch, "E2131", {"start": v(-11.42, -45.62) * mm, "end": v(-10.93, -45.66) * mm});
            skLineSegment(sketch, "E2132", {"start": v(-10.93, -45.66) * mm, "end": v(-10.46, -45.8) * mm});
            skLineSegment(sketch, "E2133", {"start": v(-10.46, -45.8) * mm, "end": v(-10.46, -45.8) * mm});
            skLineSegment(sketch, "E2134", {"start": v(-10.46, -45.8) * mm, "end": v(-10.02, -46.03) * mm});
            skLineSegment(sketch, "E2135", {"start": v(-10.02, -46.03) * mm, "end": v(-9.64, -46.34) * mm});
            skLineSegment(sketch, "E2136", {"start": v(-9.64, -46.34) * mm, "end": v(-9.32, -46.72) * mm});
            skLineSegment(sketch, "E2137", {"start": v(-9.32, -46.72) * mm, "end": v(-9.09, -47.15) * mm});
            skLineSegment(sketch, "E2138", {"start": v(-9.09, -47.15) * mm, "end": v(-8.94, -47.62) * mm});
            skLineSegment(sketch, "E2139", {"start": v(-8.94, -47.62) * mm, "end": v(-8.91, -47.85) * mm});
            skLineSegment(sketch, "E2140", {"start": v(-8.91, -47.85) * mm, "end": v(-8.91, -47.86) * mm});
            skLineSegment(sketch, "E2141", {"start": v(-8.91, -47.86) * mm, "end": v(-8.9, -47.9) * mm});
            skLineSegment(sketch, "E2142", {"start": v(-8.9, -47.9) * mm, "end": v(-8.89, -48.11) * mm});
            skLineSegment(sketch, "E2143", {"start": v(-8.89, -48.11) * mm, "end": v(-8.9, -48.17) * mm});
            skLineSegment(sketch, "E2144", {"start": v(-8.9, -48.17) * mm, "end": v(-8.9, -48.22) * mm});
            skLineSegment(sketch, "E2145", {"start": v(-8.9, -48.22) * mm, "end": v(-8.89, -48.36) * mm});
            skLineSegment(sketch, "E2146", {"start": v(-8.89, -48.36) * mm, "end": v(-8.97, -48.84) * mm});
            skLineSegment(sketch, "E2147", {"start": v(-8.97, -48.84) * mm, "end": v(-9.01, -48.97) * mm});
            skLineSegment(sketch, "E2148", {"start": v(-9.01, -48.97) * mm, "end": v(-9.03, -49.02) * mm});
            skLineSegment(sketch, "E2149", {"start": v(-9.03, -49.02) * mm, "end": v(-9.06, -49.18) * mm});
            skLineSegment(sketch, "E2150", {"start": v(-9.06, -49.18) * mm, "end": v(-9.15, -49.38) * mm});
            skLineSegment(sketch, "E2151", {"start": v(-9.15, -49.38) * mm, "end": v(-9.18, -49.43) * mm});
            skLineSegment(sketch, "E2152", {"start": v(-9.18, -49.43) * mm, "end": v(-9.18, -49.76) * mm});
            skLineSegment(sketch, "E2153", {"start": v(-9.18, -49.76) * mm, "end": v(-9.18, -49.8) * mm});
            skLineSegment(sketch, "E2154", {"start": v(-9.18, -49.8) * mm, "end": v(-9.17, -49.93) * mm});
            skLineSegment(sketch, "E2155", {"start": v(-9.17, -49.93) * mm, "end": v(-9.15, -50.01) * mm});
            skLineSegment(sketch, "E2156", {"start": v(-9.15, -50.01) * mm, "end": v(-9.04, -50.44) * mm});
            skLineSegment(sketch, "E2157", {"start": v(-9.04, -50.44) * mm, "end": v(-8.82, -50.88) * mm});
            skLineSegment(sketch, "E2158", {"start": v(-8.82, -50.88) * mm, "end": v(-8.52, -51.27) * mm});
            skLineSegment(sketch, "E2159", {"start": v(-8.52, -51.27) * mm, "end": v(-8.15, -51.6) * mm});
            skLineSegment(sketch, "E2160", {"start": v(-8.15, -51.6) * mm, "end": v(-7.73, -51.85) * mm});
            skLineSegment(sketch, "E2161", {"start": v(-7.73, -51.85) * mm, "end": v(-7.26, -52) * mm});
            skLineSegment(sketch, "E2162", {"start": v(-7.26, -52) * mm, "end": v(-7.26, -52) * mm});
            skSolve(sketch);
        }
        {
            var Q0;
            Q0 = qSketchRegion(id + "F0", true);
            extrude(context, id + "F1", {"entities" : qUnion([Q0]), "depth" : 12.7 * mm});
        }
    });
